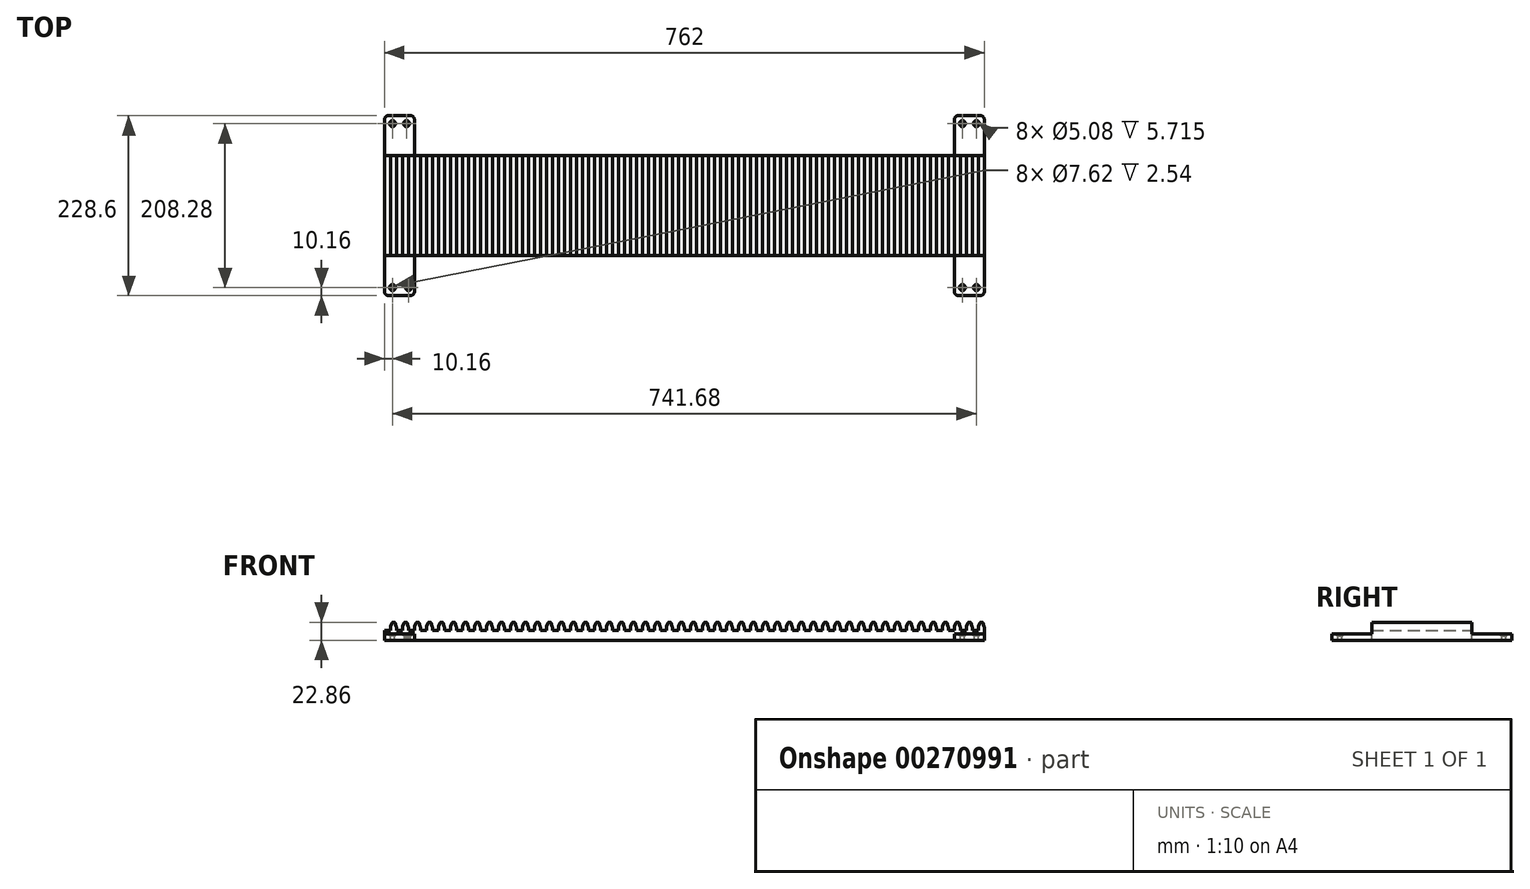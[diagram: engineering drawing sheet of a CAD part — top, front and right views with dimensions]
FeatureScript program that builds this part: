
annotation { "Feature Type Name" : "Feature", "Feature Type Description" : "" }
export const myFeature = defineFeature(function(context is Context, id is Id, definition is map)
    precondition{}
    {
        {
            var Q0;
            Q0=qCreatedBy(makeId("Front.planeOp"),FACE);
            var sketch = newSketch(context, id + "F0", { "sketchPlane" : qUnion([Q0])});
            skLineSegment(sketch, "E0.bottom", {"start": v(0, 0) * mm, "end": v(762, 0) * mm});
            skLineSegment(sketch, "E0.top", {"start": v(0, 12.7) * mm, "end": v(762, 12.7) * mm});
            skLineSegment(sketch, "E0.left", {"start": v(0, 0) * mm, "end": v(0, 12.7) * mm});
            skLineSegment(sketch, "E0.right", {"start": v(762, 0) * mm, "end": v(762, 12.7) * mm});
            skLineSegment(sketch, "E1", {"start": v(7.62, 12.7) * mm, "end": v(7.62, 15.54) * mm});
            skLineSegment(sketch, "E2", {"start": v(8, 17.71) * mm, "end": v(9.69, 22.34) * mm});
            skLineSegment(sketch, "E3", {"start": v(11.43, 25.84) * mm, "end": v(11.43, 12.7) * mm, "construction": true});
            skLineSegment(sketch, "E4", {"start": v(10.43, 22.86) * mm, "end": v(11.43, 22.86) * mm});
            skLineSegment(sketch, "E5.MirrorCS", {"start": v(12.43, 22.86) * mm, "end": v(11.43, 22.86) * mm});
            skLineSegment(sketch, "E6.MirrorCS", {"start": v(14.86, 17.71) * mm, "end": v(13.17, 22.34) * mm});
            skLineSegment(sketch, "E7.MirrorCS", {"start": v(15.24, 12.7) * mm, "end": v(15.24, 15.54) * mm});
            skPoint(sketch, "E8.visualSharp", {"position": v(12.98, 22.86) * mm});
            skArc(sketch, "E8.filletArc", {"start": v(13.17, 22.34) * mm, "mid": v(12.88, 22.72) * mm, "end": v(12.43, 22.86) * mm});
            skPoint(sketch, "E9.visualSharp", {"position": v(9.88, 22.86) * mm});
            skArc(sketch, "E9.filletArc", {"start": v(10.43, 22.86) * mm, "mid": v(9.98, 22.72) * mm, "end": v(9.69, 22.34) * mm});
            skPoint(sketch, "E10.visualSharp", {"position": v(15.24, 16.66) * mm});
            skArc(sketch, "E10.filletArc", {"start": v(15.24, 15.54) * mm, "mid": v(15.14, 16.65) * mm, "end": v(14.86, 17.71) * mm});
            skPoint(sketch, "E11.visualSharp", {"position": v(7.62, 16.66) * mm});
            skArc(sketch, "E11.filletArc", {"start": v(8, 17.71) * mm, "mid": v(7.72, 16.65) * mm, "end": v(7.62, 15.54) * mm});
            skLineSegment(sketch, "E12.1.0.0", {"start": v(22.86, 12.7) * mm, "end": v(22.86, 15.54) * mm});
            skArc(sketch, "E12.1.0.1", {"start": v(23.24, 17.71) * mm, "mid": v(22.96, 16.65) * mm, "end": v(22.86, 15.54) * mm});
            skLineSegment(sketch, "E12.1.0.2", {"start": v(23.24, 17.71) * mm, "end": v(24.93, 22.34) * mm});
            skPoint(sketch, "E12.1.0.3", {"position": v(25.12, 22.86) * mm});
            skArc(sketch, "E12.1.0.4", {"start": v(25.67, 22.86) * mm, "mid": v(25.22, 22.72) * mm, "end": v(24.93, 22.34) * mm});
            skLineSegment(sketch, "E12.1.0.5", {"start": v(25.67, 22.86) * mm, "end": v(26.67, 22.86) * mm});
            skLineSegment(sketch, "E12.1.0.6", {"start": v(27.67, 22.86) * mm, "end": v(26.67, 22.86) * mm});
            skArc(sketch, "E12.1.0.7", {"start": v(28.41, 22.34) * mm, "mid": v(28.12, 22.72) * mm, "end": v(27.67, 22.86) * mm});
            skLineSegment(sketch, "E12.1.0.8", {"start": v(30.1, 17.71) * mm, "end": v(28.41, 22.34) * mm});
            skArc(sketch, "E12.1.0.9", {"start": v(30.48, 15.54) * mm, "mid": v(30.38, 16.65) * mm, "end": v(30.1, 17.71) * mm});
            skLineSegment(sketch, "E12.1.0.10", {"start": v(30.48, 12.7) * mm, "end": v(30.48, 15.54) * mm});
            skLineSegment(sketch, "E12.2.0.0", {"start": v(38.1, 12.7) * mm, "end": v(38.1, 15.54) * mm});
            skArc(sketch, "E12.2.0.1", {"start": v(38.48, 17.71) * mm, "mid": v(38.2, 16.65) * mm, "end": v(38.1, 15.54) * mm});
            skLineSegment(sketch, "E12.2.0.2", {"start": v(38.48, 17.71) * mm, "end": v(40.17, 22.34) * mm});
            skPoint(sketch, "E12.2.0.3", {"position": v(40.36, 22.86) * mm});
            skArc(sketch, "E12.2.0.4", {"start": v(40.91, 22.86) * mm, "mid": v(40.46, 22.72) * mm, "end": v(40.17, 22.34) * mm});
            skLineSegment(sketch, "E12.2.0.5", {"start": v(40.91, 22.86) * mm, "end": v(41.91, 22.86) * mm});
            skLineSegment(sketch, "E12.2.0.6", {"start": v(42.9, 22.86) * mm, "end": v(41.91, 22.86) * mm});
            skArc(sketch, "E12.2.0.7", {"start": v(43.65, 22.34) * mm, "mid": v(43.36, 22.72) * mm, "end": v(42.9, 22.86) * mm});
            skLineSegment(sketch, "E12.2.0.8", {"start": v(45.34, 17.71) * mm, "end": v(43.65, 22.34) * mm});
            skArc(sketch, "E12.2.0.9", {"start": v(45.72, 15.54) * mm, "mid": v(45.62, 16.65) * mm, "end": v(45.34, 17.71) * mm});
            skLineSegment(sketch, "E12.2.0.10", {"start": v(45.72, 12.7) * mm, "end": v(45.72, 15.54) * mm});
            skLineSegment(sketch, "E12.3.0.0", {"start": v(53.34, 12.7) * mm, "end": v(53.34, 15.54) * mm});
            skArc(sketch, "E12.3.0.1", {"start": v(53.72, 17.71) * mm, "mid": v(53.44, 16.65) * mm, "end": v(53.34, 15.54) * mm});
            skLineSegment(sketch, "E12.3.0.2", {"start": v(53.72, 17.71) * mm, "end": v(55.4, 22.34) * mm});
            skPoint(sketch, "E12.3.0.3", {"position": v(55.6, 22.86) * mm});
            skArc(sketch, "E12.3.0.4", {"start": v(56.15, 22.86) * mm, "mid": v(55.7, 22.72) * mm, "end": v(55.4, 22.34) * mm});
            skLineSegment(sketch, "E12.3.0.5", {"start": v(56.15, 22.86) * mm, "end": v(57.15, 22.86) * mm});
            skLineSegment(sketch, "E12.3.0.6", {"start": v(58.15, 22.86) * mm, "end": v(57.15, 22.86) * mm});
            skArc(sketch, "E12.3.0.7", {"start": v(58.9, 22.34) * mm, "mid": v(58.6, 22.72) * mm, "end": v(58.15, 22.86) * mm});
            skLineSegment(sketch, "E12.3.0.8", {"start": v(60.58, 17.71) * mm, "end": v(58.9, 22.34) * mm});
            skArc(sketch, "E12.3.0.9", {"start": v(60.96, 15.54) * mm, "mid": v(60.86, 16.65) * mm, "end": v(60.58, 17.71) * mm});
            skLineSegment(sketch, "E12.3.0.10", {"start": v(60.96, 12.7) * mm, "end": v(60.96, 15.54) * mm});
            skLineSegment(sketch, "E12.4.0.0", {"start": v(68.58, 12.7) * mm, "end": v(68.58, 15.54) * mm});
            skArc(sketch, "E12.4.0.1", {"start": v(68.96, 17.71) * mm, "mid": v(68.68, 16.65) * mm, "end": v(68.58, 15.54) * mm});
            skLineSegment(sketch, "E12.4.0.2", {"start": v(68.96, 17.71) * mm, "end": v(70.65, 22.34) * mm});
            skPoint(sketch, "E12.4.0.3", {"position": v(70.84, 22.86) * mm});
            skArc(sketch, "E12.4.0.4", {"start": v(71.4, 22.86) * mm, "mid": v(70.94, 22.72) * mm, "end": v(70.65, 22.34) * mm});
            skLineSegment(sketch, "E12.4.0.5", {"start": v(71.4, 22.86) * mm, "end": v(72.4, 22.86) * mm});
            skLineSegment(sketch, "E12.4.0.6", {"start": v(73.39, 22.86) * mm, "end": v(72.4, 22.86) * mm});
            skArc(sketch, "E12.4.0.7", {"start": v(74.13, 22.34) * mm, "mid": v(73.84, 22.72) * mm, "end": v(73.39, 22.86) * mm});
            skLineSegment(sketch, "E12.4.0.8", {"start": v(75.82, 17.71) * mm, "end": v(74.13, 22.34) * mm});
            skArc(sketch, "E12.4.0.9", {"start": v(76.2, 15.54) * mm, "mid": v(76.1, 16.65) * mm, "end": v(75.82, 17.71) * mm});
            skLineSegment(sketch, "E12.4.0.10", {"start": v(76.2, 12.7) * mm, "end": v(76.2, 15.54) * mm});
            skLineSegment(sketch, "E12.5.0.0", {"start": v(83.82, 12.7) * mm, "end": v(83.82, 15.54) * mm});
            skArc(sketch, "E12.5.0.1", {"start": v(84.2, 17.71) * mm, "mid": v(83.92, 16.65) * mm, "end": v(83.82, 15.54) * mm});
            skLineSegment(sketch, "E12.5.0.2", {"start": v(84.2, 17.71) * mm, "end": v(85.89, 22.34) * mm});
            skPoint(sketch, "E12.5.0.3", {"position": v(86.08, 22.86) * mm});
            skArc(sketch, "E12.5.0.4", {"start": v(86.63, 22.86) * mm, "mid": v(86.18, 22.72) * mm, "end": v(85.89, 22.34) * mm});
            skLineSegment(sketch, "E12.5.0.5", {"start": v(86.63, 22.86) * mm, "end": v(87.63, 22.86) * mm});
            skLineSegment(sketch, "E12.5.0.6", {"start": v(88.63, 22.86) * mm, "end": v(87.63, 22.86) * mm});
            skArc(sketch, "E12.5.0.7", {"start": v(89.37, 22.34) * mm, "mid": v(89.08, 22.72) * mm, "end": v(88.63, 22.86) * mm});
            skLineSegment(sketch, "E12.5.0.8", {"start": v(91.06, 17.71) * mm, "end": v(89.37, 22.34) * mm});
            skArc(sketch, "E12.5.0.9", {"start": v(91.44, 15.54) * mm, "mid": v(91.34, 16.65) * mm, "end": v(91.06, 17.71) * mm});
            skLineSegment(sketch, "E12.5.0.10", {"start": v(91.44, 12.7) * mm, "end": v(91.44, 15.54) * mm});
            skLineSegment(sketch, "E12.6.0.0", {"start": v(99.06, 12.7) * mm, "end": v(99.06, 15.54) * mm});
            skArc(sketch, "E12.6.0.1", {"start": v(99.44, 17.71) * mm, "mid": v(99.16, 16.65) * mm, "end": v(99.06, 15.54) * mm});
            skLineSegment(sketch, "E12.6.0.2", {"start": v(99.44, 17.71) * mm, "end": v(101.13, 22.34) * mm});
            skPoint(sketch, "E12.6.0.3", {"position": v(101.32, 22.86) * mm});
            skArc(sketch, "E12.6.0.4", {"start": v(101.87, 22.86) * mm, "mid": v(101.42, 22.72) * mm, "end": v(101.13, 22.34) * mm});
            skLineSegment(sketch, "E12.6.0.5", {"start": v(101.87, 22.86) * mm, "end": v(102.87, 22.86) * mm});
            skLineSegment(sketch, "E12.6.0.6", {"start": v(103.87, 22.86) * mm, "end": v(102.87, 22.86) * mm});
            skArc(sketch, "E12.6.0.7", {"start": v(104.61, 22.34) * mm, "mid": v(104.32, 22.72) * mm, "end": v(103.87, 22.86) * mm});
            skLineSegment(sketch, "E12.6.0.8", {"start": v(106.3, 17.71) * mm, "end": v(104.61, 22.34) * mm});
            skArc(sketch, "E12.6.0.9", {"start": v(106.68, 15.54) * mm, "mid": v(106.58, 16.65) * mm, "end": v(106.3, 17.71) * mm});
            skLineSegment(sketch, "E12.6.0.10", {"start": v(106.68, 12.7) * mm, "end": v(106.68, 15.54) * mm});
            skLineSegment(sketch, "E12.7.0.0", {"start": v(114.3, 12.7) * mm, "end": v(114.3, 15.54) * mm});
            skArc(sketch, "E12.7.0.1", {"start": v(114.68, 17.71) * mm, "mid": v(114.4, 16.65) * mm, "end": v(114.3, 15.54) * mm});
            skLineSegment(sketch, "E12.7.0.2", {"start": v(114.68, 17.71) * mm, "end": v(116.37, 22.34) * mm});
            skPoint(sketch, "E12.7.0.3", {"position": v(116.56, 22.86) * mm});
            skArc(sketch, "E12.7.0.4", {"start": v(117.11, 22.86) * mm, "mid": v(116.66, 22.72) * mm, "end": v(116.37, 22.34) * mm});
            skLineSegment(sketch, "E12.7.0.5", {"start": v(117.11, 22.86) * mm, "end": v(118.11, 22.86) * mm});
            skLineSegment(sketch, "E12.7.0.6", {"start": v(119.1, 22.86) * mm, "end": v(118.11, 22.86) * mm});
            skArc(sketch, "E12.7.0.7", {"start": v(119.85, 22.34) * mm, "mid": v(119.56, 22.72) * mm, "end": v(119.1, 22.86) * mm});
            skLineSegment(sketch, "E12.7.0.8", {"start": v(121.54, 17.71) * mm, "end": v(119.85, 22.34) * mm});
            skArc(sketch, "E12.7.0.9", {"start": v(121.92, 15.54) * mm, "mid": v(121.82, 16.65) * mm, "end": v(121.54, 17.71) * mm});
            skLineSegment(sketch, "E12.7.0.10", {"start": v(121.92, 12.7) * mm, "end": v(121.92, 15.54) * mm});
            skLineSegment(sketch, "E12.8.0.0", {"start": v(129.54, 12.7) * mm, "end": v(129.54, 15.54) * mm});
            skArc(sketch, "E12.8.0.1", {"start": v(129.92, 17.71) * mm, "mid": v(129.64, 16.65) * mm, "end": v(129.54, 15.54) * mm});
            skLineSegment(sketch, "E12.8.0.2", {"start": v(129.92, 17.71) * mm, "end": v(131.6, 22.34) * mm});
            skPoint(sketch, "E12.8.0.3", {"position": v(131.8, 22.86) * mm});
            skArc(sketch, "E12.8.0.4", {"start": v(132.35, 22.86) * mm, "mid": v(131.9, 22.72) * mm, "end": v(131.6, 22.34) * mm});
            skLineSegment(sketch, "E12.8.0.5", {"start": v(132.35, 22.86) * mm, "end": v(133.35, 22.86) * mm});
            skLineSegment(sketch, "E12.8.0.6", {"start": v(134.35, 22.86) * mm, "end": v(133.35, 22.86) * mm});
            skArc(sketch, "E12.8.0.7", {"start": v(135.1, 22.34) * mm, "mid": v(134.8, 22.72) * mm, "end": v(134.35, 22.86) * mm});
            skLineSegment(sketch, "E12.8.0.8", {"start": v(136.78, 17.71) * mm, "end": v(135.1, 22.34) * mm});
            skArc(sketch, "E12.8.0.9", {"start": v(137.16, 15.54) * mm, "mid": v(137.06, 16.65) * mm, "end": v(136.78, 17.71) * mm});
            skLineSegment(sketch, "E12.8.0.10", {"start": v(137.16, 12.7) * mm, "end": v(137.16, 15.54) * mm});
            skLineSegment(sketch, "E12.9.0.0", {"start": v(144.78, 12.7) * mm, "end": v(144.78, 15.54) * mm});
            skArc(sketch, "E12.9.0.1", {"start": v(145.16, 17.71) * mm, "mid": v(144.88, 16.65) * mm, "end": v(144.78, 15.54) * mm});
            skLineSegment(sketch, "E12.9.0.2", {"start": v(145.16, 17.71) * mm, "end": v(146.85, 22.34) * mm});
            skPoint(sketch, "E12.9.0.3", {"position": v(147.04, 22.86) * mm});
            skArc(sketch, "E12.9.0.4", {"start": v(147.6, 22.86) * mm, "mid": v(147.14, 22.72) * mm, "end": v(146.85, 22.34) * mm});
            skLineSegment(sketch, "E12.9.0.5", {"start": v(147.6, 22.86) * mm, "end": v(148.6, 22.86) * mm});
            skLineSegment(sketch, "E12.9.0.6", {"start": v(149.59, 22.86) * mm, "end": v(148.6, 22.86) * mm});
            skArc(sketch, "E12.9.0.7", {"start": v(150.33, 22.34) * mm, "mid": v(150.04, 22.72) * mm, "end": v(149.59, 22.86) * mm});
            skLineSegment(sketch, "E12.9.0.8", {"start": v(152.02, 17.71) * mm, "end": v(150.33, 22.34) * mm});
            skArc(sketch, "E12.9.0.9", {"start": v(152.4, 15.54) * mm, "mid": v(152.3, 16.65) * mm, "end": v(152.02, 17.71) * mm});
            skLineSegment(sketch, "E12.9.0.10", {"start": v(152.4, 12.7) * mm, "end": v(152.4, 15.54) * mm});
            skLineSegment(sketch, "E12.10.0.0", {"start": v(160.02, 12.7) * mm, "end": v(160.02, 15.54) * mm});
            skArc(sketch, "E12.10.0.1", {"start": v(160.4, 17.71) * mm, "mid": v(160.12, 16.65) * mm, "end": v(160.02, 15.54) * mm});
            skLineSegment(sketch, "E12.10.0.2", {"start": v(160.4, 17.71) * mm, "end": v(162.09, 22.34) * mm});
            skPoint(sketch, "E12.10.0.3", {"position": v(162.28, 22.86) * mm});
            skArc(sketch, "E12.10.0.4", {"start": v(162.83, 22.86) * mm, "mid": v(162.38, 22.72) * mm, "end": v(162.09, 22.34) * mm});
            skLineSegment(sketch, "E12.10.0.5", {"start": v(162.83, 22.86) * mm, "end": v(163.83, 22.86) * mm});
            skLineSegment(sketch, "E12.10.0.6", {"start": v(164.83, 22.86) * mm, "end": v(163.83, 22.86) * mm});
            skArc(sketch, "E12.10.0.7", {"start": v(165.57, 22.34) * mm, "mid": v(165.28, 22.72) * mm, "end": v(164.83, 22.86) * mm});
            skLineSegment(sketch, "E12.10.0.8", {"start": v(167.26, 17.71) * mm, "end": v(165.57, 22.34) * mm});
            skArc(sketch, "E12.10.0.9", {"start": v(167.64, 15.54) * mm, "mid": v(167.54, 16.65) * mm, "end": v(167.26, 17.71) * mm});
            skLineSegment(sketch, "E12.10.0.10", {"start": v(167.64, 12.7) * mm, "end": v(167.64, 15.54) * mm});
            skLineSegment(sketch, "E12.11.0.0", {"start": v(175.26, 12.7) * mm, "end": v(175.26, 15.54) * mm});
            skArc(sketch, "E12.11.0.1", {"start": v(175.64, 17.71) * mm, "mid": v(175.36, 16.65) * mm, "end": v(175.26, 15.54) * mm});
            skLineSegment(sketch, "E12.11.0.2", {"start": v(175.64, 17.71) * mm, "end": v(177.33, 22.34) * mm});
            skPoint(sketch, "E12.11.0.3", {"position": v(177.52, 22.86) * mm});
            skArc(sketch, "E12.11.0.4", {"start": v(178.07, 22.86) * mm, "mid": v(177.62, 22.72) * mm, "end": v(177.33, 22.34) * mm});
            skLineSegment(sketch, "E12.11.0.5", {"start": v(178.07, 22.86) * mm, "end": v(179.07, 22.86) * mm});
            skLineSegment(sketch, "E12.11.0.6", {"start": v(180.07, 22.86) * mm, "end": v(179.07, 22.86) * mm});
            skArc(sketch, "E12.11.0.7", {"start": v(180.81, 22.34) * mm, "mid": v(180.52, 22.72) * mm, "end": v(180.07, 22.86) * mm});
            skLineSegment(sketch, "E12.11.0.8", {"start": v(182.5, 17.71) * mm, "end": v(180.81, 22.34) * mm});
            skArc(sketch, "E12.11.0.9", {"start": v(182.88, 15.54) * mm, "mid": v(182.78, 16.65) * mm, "end": v(182.5, 17.71) * mm});
            skLineSegment(sketch, "E12.11.0.10", {"start": v(182.88, 12.7) * mm, "end": v(182.88, 15.54) * mm});
            skLineSegment(sketch, "E12.12.0.0", {"start": v(190.5, 12.7) * mm, "end": v(190.5, 15.54) * mm});
            skArc(sketch, "E12.12.0.1", {"start": v(190.88, 17.71) * mm, "mid": v(190.6, 16.65) * mm, "end": v(190.5, 15.54) * mm});
            skLineSegment(sketch, "E12.12.0.2", {"start": v(190.88, 17.71) * mm, "end": v(192.57, 22.34) * mm});
            skPoint(sketch, "E12.12.0.3", {"position": v(192.76, 22.86) * mm});
            skArc(sketch, "E12.12.0.4", {"start": v(193.31, 22.86) * mm, "mid": v(192.86, 22.72) * mm, "end": v(192.57, 22.34) * mm});
            skLineSegment(sketch, "E12.12.0.5", {"start": v(193.31, 22.86) * mm, "end": v(194.31, 22.86) * mm});
            skLineSegment(sketch, "E12.12.0.6", {"start": v(195.3, 22.86) * mm, "end": v(194.31, 22.86) * mm});
            skArc(sketch, "E12.12.0.7", {"start": v(196.05, 22.34) * mm, "mid": v(195.76, 22.72) * mm, "end": v(195.3, 22.86) * mm});
            skLineSegment(sketch, "E12.12.0.8", {"start": v(197.74, 17.71) * mm, "end": v(196.05, 22.34) * mm});
            skArc(sketch, "E12.12.0.9", {"start": v(198.12, 15.54) * mm, "mid": v(198.02, 16.65) * mm, "end": v(197.74, 17.71) * mm});
            skLineSegment(sketch, "E12.12.0.10", {"start": v(198.12, 12.7) * mm, "end": v(198.12, 15.54) * mm});
            skLineSegment(sketch, "E12.13.0.0", {"start": v(205.74, 12.7) * mm, "end": v(205.74, 15.54) * mm});
            skArc(sketch, "E12.13.0.1", {"start": v(206.12, 17.71) * mm, "mid": v(205.84, 16.65) * mm, "end": v(205.74, 15.54) * mm});
            skLineSegment(sketch, "E12.13.0.2", {"start": v(206.12, 17.71) * mm, "end": v(207.8, 22.34) * mm});
            skPoint(sketch, "E12.13.0.3", {"position": v(208, 22.86) * mm});
            skArc(sketch, "E12.13.0.4", {"start": v(208.55, 22.86) * mm, "mid": v(208.1, 22.72) * mm, "end": v(207.8, 22.34) * mm});
            skLineSegment(sketch, "E12.13.0.5", {"start": v(208.55, 22.86) * mm, "end": v(209.55, 22.86) * mm});
            skLineSegment(sketch, "E12.13.0.6", {"start": v(210.55, 22.86) * mm, "end": v(209.55, 22.86) * mm});
            skArc(sketch, "E12.13.0.7", {"start": v(211.3, 22.34) * mm, "mid": v(211, 22.72) * mm, "end": v(210.55, 22.86) * mm});
            skLineSegment(sketch, "E12.13.0.8", {"start": v(212.98, 17.71) * mm, "end": v(211.3, 22.34) * mm});
            skArc(sketch, "E12.13.0.9", {"start": v(213.36, 15.54) * mm, "mid": v(213.26, 16.65) * mm, "end": v(212.98, 17.71) * mm});
            skLineSegment(sketch, "E12.13.0.10", {"start": v(213.36, 12.7) * mm, "end": v(213.36, 15.54) * mm});
            skLineSegment(sketch, "E12.14.0.0", {"start": v(220.98, 12.7) * mm, "end": v(220.98, 15.54) * mm});
            skArc(sketch, "E12.14.0.1", {"start": v(221.36, 17.71) * mm, "mid": v(221.08, 16.65) * mm, "end": v(220.98, 15.54) * mm});
            skLineSegment(sketch, "E12.14.0.2", {"start": v(221.36, 17.71) * mm, "end": v(223.05, 22.34) * mm});
            skPoint(sketch, "E12.14.0.3", {"position": v(223.24, 22.86) * mm});
            skArc(sketch, "E12.14.0.4", {"start": v(223.8, 22.86) * mm, "mid": v(223.34, 22.72) * mm, "end": v(223.05, 22.34) * mm});
            skLineSegment(sketch, "E12.14.0.5", {"start": v(223.8, 22.86) * mm, "end": v(224.8, 22.86) * mm});
            skLineSegment(sketch, "E12.14.0.6", {"start": v(225.79, 22.86) * mm, "end": v(224.8, 22.86) * mm});
            skArc(sketch, "E12.14.0.7", {"start": v(226.53, 22.34) * mm, "mid": v(226.24, 22.72) * mm, "end": v(225.79, 22.86) * mm});
            skLineSegment(sketch, "E12.14.0.8", {"start": v(228.22, 17.71) * mm, "end": v(226.53, 22.34) * mm});
            skArc(sketch, "E12.14.0.9", {"start": v(228.6, 15.54) * mm, "mid": v(228.5, 16.65) * mm, "end": v(228.22, 17.71) * mm});
            skLineSegment(sketch, "E12.14.0.10", {"start": v(228.6, 12.7) * mm, "end": v(228.6, 15.54) * mm});
            skLineSegment(sketch, "E12.15.0.0", {"start": v(236.22, 12.7) * mm, "end": v(236.22, 15.54) * mm});
            skArc(sketch, "E12.15.0.1", {"start": v(236.6, 17.71) * mm, "mid": v(236.32, 16.65) * mm, "end": v(236.22, 15.54) * mm});
            skLineSegment(sketch, "E12.15.0.2", {"start": v(236.6, 17.71) * mm, "end": v(238.29, 22.34) * mm});
            skPoint(sketch, "E12.15.0.3", {"position": v(238.48, 22.86) * mm});
            skArc(sketch, "E12.15.0.4", {"start": v(239.03, 22.86) * mm, "mid": v(238.58, 22.72) * mm, "end": v(238.29, 22.34) * mm});
            skLineSegment(sketch, "E12.15.0.5", {"start": v(239.03, 22.86) * mm, "end": v(240.03, 22.86) * mm});
            skLineSegment(sketch, "E12.15.0.6", {"start": v(241.03, 22.86) * mm, "end": v(240.03, 22.86) * mm});
            skArc(sketch, "E12.15.0.7", {"start": v(241.77, 22.34) * mm, "mid": v(241.48, 22.72) * mm, "end": v(241.03, 22.86) * mm});
            skLineSegment(sketch, "E12.15.0.8", {"start": v(243.46, 17.71) * mm, "end": v(241.77, 22.34) * mm});
            skArc(sketch, "E12.15.0.9", {"start": v(243.84, 15.54) * mm, "mid": v(243.74, 16.65) * mm, "end": v(243.46, 17.71) * mm});
            skLineSegment(sketch, "E12.15.0.10", {"start": v(243.84, 12.7) * mm, "end": v(243.84, 15.54) * mm});
            skLineSegment(sketch, "E12.16.0.0", {"start": v(251.46, 12.7) * mm, "end": v(251.46, 15.54) * mm});
            skArc(sketch, "E12.16.0.1", {"start": v(251.84, 17.71) * mm, "mid": v(251.56, 16.65) * mm, "end": v(251.46, 15.54) * mm});
            skLineSegment(sketch, "E12.16.0.2", {"start": v(251.84, 17.71) * mm, "end": v(253.53, 22.34) * mm});
            skPoint(sketch, "E12.16.0.3", {"position": v(253.72, 22.86) * mm});
            skArc(sketch, "E12.16.0.4", {"start": v(254.27, 22.86) * mm, "mid": v(253.82, 22.72) * mm, "end": v(253.53, 22.34) * mm});
            skLineSegment(sketch, "E12.16.0.5", {"start": v(254.27, 22.86) * mm, "end": v(255.27, 22.86) * mm});
            skLineSegment(sketch, "E12.16.0.6", {"start": v(256.27, 22.86) * mm, "end": v(255.27, 22.86) * mm});
            skArc(sketch, "E12.16.0.7", {"start": v(257.01, 22.34) * mm, "mid": v(256.72, 22.72) * mm, "end": v(256.27, 22.86) * mm});
            skLineSegment(sketch, "E12.16.0.8", {"start": v(258.7, 17.71) * mm, "end": v(257.01, 22.34) * mm});
            skArc(sketch, "E12.16.0.9", {"start": v(259.08, 15.54) * mm, "mid": v(258.98, 16.65) * mm, "end": v(258.7, 17.71) * mm});
            skLineSegment(sketch, "E12.16.0.10", {"start": v(259.08, 12.7) * mm, "end": v(259.08, 15.54) * mm});
            skLineSegment(sketch, "E12.17.0.0", {"start": v(266.7, 12.7) * mm, "end": v(266.7, 15.54) * mm});
            skArc(sketch, "E12.17.0.1", {"start": v(267.08, 17.71) * mm, "mid": v(266.8, 16.65) * mm, "end": v(266.7, 15.54) * mm});
            skLineSegment(sketch, "E12.17.0.2", {"start": v(267.08, 17.71) * mm, "end": v(268.77, 22.34) * mm});
            skPoint(sketch, "E12.17.0.3", {"position": v(268.96, 22.86) * mm});
            skArc(sketch, "E12.17.0.4", {"start": v(269.51, 22.86) * mm, "mid": v(269.06, 22.72) * mm, "end": v(268.77, 22.34) * mm});
            skLineSegment(sketch, "E12.17.0.5", {"start": v(269.51, 22.86) * mm, "end": v(270.51, 22.86) * mm});
            skLineSegment(sketch, "E12.17.0.6", {"start": v(271.5, 22.86) * mm, "end": v(270.51, 22.86) * mm});
            skArc(sketch, "E12.17.0.7", {"start": v(272.25, 22.34) * mm, "mid": v(271.96, 22.72) * mm, "end": v(271.5, 22.86) * mm});
            skLineSegment(sketch, "E12.17.0.8", {"start": v(273.94, 17.71) * mm, "end": v(272.25, 22.34) * mm});
            skArc(sketch, "E12.17.0.9", {"start": v(274.32, 15.54) * mm, "mid": v(274.22, 16.65) * mm, "end": v(273.94, 17.71) * mm});
            skLineSegment(sketch, "E12.17.0.10", {"start": v(274.32, 12.7) * mm, "end": v(274.32, 15.54) * mm});
            skLineSegment(sketch, "E12.18.0.0", {"start": v(281.94, 12.7) * mm, "end": v(281.94, 15.54) * mm});
            skArc(sketch, "E12.18.0.1", {"start": v(282.32, 17.71) * mm, "mid": v(282.04, 16.65) * mm, "end": v(281.94, 15.54) * mm});
            skLineSegment(sketch, "E12.18.0.2", {"start": v(282.32, 17.71) * mm, "end": v(284, 22.34) * mm});
            skPoint(sketch, "E12.18.0.3", {"position": v(284.2, 22.86) * mm});
            skArc(sketch, "E12.18.0.4", {"start": v(284.75, 22.86) * mm, "mid": v(284.3, 22.72) * mm, "end": v(284, 22.34) * mm});
            skLineSegment(sketch, "E12.18.0.5", {"start": v(284.75, 22.86) * mm, "end": v(285.75, 22.86) * mm});
            skLineSegment(sketch, "E12.18.0.6", {"start": v(286.75, 22.86) * mm, "end": v(285.75, 22.86) * mm});
            skArc(sketch, "E12.18.0.7", {"start": v(287.5, 22.34) * mm, "mid": v(287.2, 22.72) * mm, "end": v(286.75, 22.86) * mm});
            skLineSegment(sketch, "E12.18.0.8", {"start": v(289.18, 17.71) * mm, "end": v(287.5, 22.34) * mm});
            skArc(sketch, "E12.18.0.9", {"start": v(289.56, 15.54) * mm, "mid": v(289.46, 16.65) * mm, "end": v(289.18, 17.71) * mm});
            skLineSegment(sketch, "E12.18.0.10", {"start": v(289.56, 12.7) * mm, "end": v(289.56, 15.54) * mm});
            skLineSegment(sketch, "E12.19.0.0", {"start": v(297.18, 12.7) * mm, "end": v(297.18, 15.54) * mm});
            skArc(sketch, "E12.19.0.1", {"start": v(297.56, 17.71) * mm, "mid": v(297.28, 16.65) * mm, "end": v(297.18, 15.54) * mm});
            skLineSegment(sketch, "E12.19.0.2", {"start": v(297.56, 17.71) * mm, "end": v(299.25, 22.34) * mm});
            skPoint(sketch, "E12.19.0.3", {"position": v(299.44, 22.86) * mm});
            skArc(sketch, "E12.19.0.4", {"start": v(300, 22.86) * mm, "mid": v(299.54, 22.72) * mm, "end": v(299.25, 22.34) * mm});
            skLineSegment(sketch, "E12.19.0.5", {"start": v(300, 22.86) * mm, "end": v(301, 22.86) * mm});
            skLineSegment(sketch, "E12.19.0.6", {"start": v(301.99, 22.86) * mm, "end": v(301, 22.86) * mm});
            skArc(sketch, "E12.19.0.7", {"start": v(302.73, 22.34) * mm, "mid": v(302.44, 22.72) * mm, "end": v(301.99, 22.86) * mm});
            skLineSegment(sketch, "E12.19.0.8", {"start": v(304.42, 17.71) * mm, "end": v(302.73, 22.34) * mm});
            skArc(sketch, "E12.19.0.9", {"start": v(304.8, 15.54) * mm, "mid": v(304.7, 16.65) * mm, "end": v(304.42, 17.71) * mm});
            skLineSegment(sketch, "E12.19.0.10", {"start": v(304.8, 12.7) * mm, "end": v(304.8, 15.54) * mm});
            skLineSegment(sketch, "E12.20.0.0", {"start": v(312.42, 12.7) * mm, "end": v(312.42, 15.54) * mm});
            skArc(sketch, "E12.20.0.1", {"start": v(312.8, 17.71) * mm, "mid": v(312.52, 16.65) * mm, "end": v(312.42, 15.54) * mm});
            skLineSegment(sketch, "E12.20.0.2", {"start": v(312.8, 17.71) * mm, "end": v(314.49, 22.34) * mm});
            skPoint(sketch, "E12.20.0.3", {"position": v(314.68, 22.86) * mm});
            skArc(sketch, "E12.20.0.4", {"start": v(315.23, 22.86) * mm, "mid": v(314.78, 22.72) * mm, "end": v(314.49, 22.34) * mm});
            skLineSegment(sketch, "E12.20.0.5", {"start": v(315.23, 22.86) * mm, "end": v(316.23, 22.86) * mm});
            skLineSegment(sketch, "E12.20.0.6", {"start": v(317.23, 22.86) * mm, "end": v(316.23, 22.86) * mm});
            skArc(sketch, "E12.20.0.7", {"start": v(317.97, 22.34) * mm, "mid": v(317.68, 22.72) * mm, "end": v(317.23, 22.86) * mm});
            skLineSegment(sketch, "E12.20.0.8", {"start": v(319.66, 17.71) * mm, "end": v(317.97, 22.34) * mm});
            skArc(sketch, "E12.20.0.9", {"start": v(320.04, 15.54) * mm, "mid": v(319.94, 16.65) * mm, "end": v(319.66, 17.71) * mm});
            skLineSegment(sketch, "E12.20.0.10", {"start": v(320.04, 12.7) * mm, "end": v(320.04, 15.54) * mm});
            skLineSegment(sketch, "E12.21.0.0", {"start": v(327.66, 12.7) * mm, "end": v(327.66, 15.54) * mm});
            skArc(sketch, "E12.21.0.1", {"start": v(328.04, 17.71) * mm, "mid": v(327.76, 16.65) * mm, "end": v(327.66, 15.54) * mm});
            skLineSegment(sketch, "E12.21.0.2", {"start": v(328.04, 17.71) * mm, "end": v(329.73, 22.34) * mm});
            skPoint(sketch, "E12.21.0.3", {"position": v(329.92, 22.86) * mm});
            skArc(sketch, "E12.21.0.4", {"start": v(330.47, 22.86) * mm, "mid": v(330.02, 22.72) * mm, "end": v(329.73, 22.34) * mm});
            skLineSegment(sketch, "E12.21.0.5", {"start": v(330.47, 22.86) * mm, "end": v(331.47, 22.86) * mm});
            skLineSegment(sketch, "E12.21.0.6", {"start": v(332.47, 22.86) * mm, "end": v(331.47, 22.86) * mm});
            skArc(sketch, "E12.21.0.7", {"start": v(333.21, 22.34) * mm, "mid": v(332.92, 22.72) * mm, "end": v(332.47, 22.86) * mm});
            skLineSegment(sketch, "E12.21.0.8", {"start": v(334.9, 17.71) * mm, "end": v(333.21, 22.34) * mm});
            skArc(sketch, "E12.21.0.9", {"start": v(335.28, 15.54) * mm, "mid": v(335.18, 16.65) * mm, "end": v(334.9, 17.71) * mm});
            skLineSegment(sketch, "E12.21.0.10", {"start": v(335.28, 12.7) * mm, "end": v(335.28, 15.54) * mm});
            skLineSegment(sketch, "E12.22.0.0", {"start": v(342.9, 12.7) * mm, "end": v(342.9, 15.54) * mm});
            skArc(sketch, "E12.22.0.1", {"start": v(343.28, 17.71) * mm, "mid": v(343, 16.65) * mm, "end": v(342.9, 15.54) * mm});
            skLineSegment(sketch, "E12.22.0.2", {"start": v(343.28, 17.71) * mm, "end": v(344.97, 22.34) * mm});
            skPoint(sketch, "E12.22.0.3", {"position": v(345.16, 22.86) * mm});
            skArc(sketch, "E12.22.0.4", {"start": v(345.71, 22.86) * mm, "mid": v(345.26, 22.72) * mm, "end": v(344.97, 22.34) * mm});
            skLineSegment(sketch, "E12.22.0.5", {"start": v(345.71, 22.86) * mm, "end": v(346.71, 22.86) * mm});
            skLineSegment(sketch, "E12.22.0.6", {"start": v(347.7, 22.86) * mm, "end": v(346.71, 22.86) * mm});
            skArc(sketch, "E12.22.0.7", {"start": v(348.45, 22.34) * mm, "mid": v(348.16, 22.72) * mm, "end": v(347.7, 22.86) * mm});
            skLineSegment(sketch, "E12.22.0.8", {"start": v(350.14, 17.71) * mm, "end": v(348.45, 22.34) * mm});
            skArc(sketch, "E12.22.0.9", {"start": v(350.52, 15.54) * mm, "mid": v(350.42, 16.65) * mm, "end": v(350.14, 17.71) * mm});
            skLineSegment(sketch, "E12.22.0.10", {"start": v(350.52, 12.7) * mm, "end": v(350.52, 15.54) * mm});
            skLineSegment(sketch, "E12.23.0.0", {"start": v(358.14, 12.7) * mm, "end": v(358.14, 15.54) * mm});
            skArc(sketch, "E12.23.0.1", {"start": v(358.52, 17.71) * mm, "mid": v(358.24, 16.65) * mm, "end": v(358.14, 15.54) * mm});
            skLineSegment(sketch, "E12.23.0.2", {"start": v(358.52, 17.71) * mm, "end": v(360.2, 22.34) * mm});
            skPoint(sketch, "E12.23.0.3", {"position": v(360.4, 22.86) * mm});
            skArc(sketch, "E12.23.0.4", {"start": v(360.95, 22.86) * mm, "mid": v(360.5, 22.72) * mm, "end": v(360.2, 22.34) * mm});
            skLineSegment(sketch, "E12.23.0.5", {"start": v(360.95, 22.86) * mm, "end": v(361.95, 22.86) * mm});
            skLineSegment(sketch, "E12.23.0.6", {"start": v(362.95, 22.86) * mm, "end": v(361.95, 22.86) * mm});
            skArc(sketch, "E12.23.0.7", {"start": v(363.7, 22.34) * mm, "mid": v(363.4, 22.72) * mm, "end": v(362.95, 22.86) * mm});
            skLineSegment(sketch, "E12.23.0.8", {"start": v(365.38, 17.71) * mm, "end": v(363.7, 22.34) * mm});
            skArc(sketch, "E12.23.0.9", {"start": v(365.76, 15.54) * mm, "mid": v(365.66, 16.65) * mm, "end": v(365.38, 17.71) * mm});
            skLineSegment(sketch, "E12.23.0.10", {"start": v(365.76, 12.7) * mm, "end": v(365.76, 15.54) * mm});
            skLineSegment(sketch, "E12.24.0.0", {"start": v(373.38, 12.7) * mm, "end": v(373.38, 15.54) * mm});
            skArc(sketch, "E12.24.0.1", {"start": v(373.76, 17.71) * mm, "mid": v(373.48, 16.65) * mm, "end": v(373.38, 15.54) * mm});
            skLineSegment(sketch, "E12.24.0.2", {"start": v(373.76, 17.71) * mm, "end": v(375.45, 22.34) * mm});
            skPoint(sketch, "E12.24.0.3", {"position": v(375.64, 22.86) * mm});
            skArc(sketch, "E12.24.0.4", {"start": v(376.2, 22.86) * mm, "mid": v(375.74, 22.72) * mm, "end": v(375.45, 22.34) * mm});
            skLineSegment(sketch, "E12.24.0.5", {"start": v(376.2, 22.86) * mm, "end": v(377.2, 22.86) * mm});
            skLineSegment(sketch, "E12.24.0.6", {"start": v(378.19, 22.86) * mm, "end": v(377.2, 22.86) * mm});
            skArc(sketch, "E12.24.0.7", {"start": v(378.93, 22.34) * mm, "mid": v(378.64, 22.72) * mm, "end": v(378.19, 22.86) * mm});
            skLineSegment(sketch, "E12.24.0.8", {"start": v(380.62, 17.71) * mm, "end": v(378.93, 22.34) * mm});
            skArc(sketch, "E12.24.0.9", {"start": v(381, 15.54) * mm, "mid": v(380.9, 16.65) * mm, "end": v(380.62, 17.71) * mm});
            skLineSegment(sketch, "E12.24.0.10", {"start": v(381, 12.7) * mm, "end": v(381, 15.54) * mm});
            skLineSegment(sketch, "E12.25.0.0", {"start": v(388.62, 12.7) * mm, "end": v(388.62, 15.54) * mm});
            skArc(sketch, "E12.25.0.1", {"start": v(389, 17.71) * mm, "mid": v(388.72, 16.65) * mm, "end": v(388.62, 15.54) * mm});
            skLineSegment(sketch, "E12.25.0.2", {"start": v(389, 17.71) * mm, "end": v(390.69, 22.34) * mm});
            skPoint(sketch, "E12.25.0.3", {"position": v(390.88, 22.86) * mm});
            skArc(sketch, "E12.25.0.4", {"start": v(391.43, 22.86) * mm, "mid": v(390.98, 22.72) * mm, "end": v(390.69, 22.34) * mm});
            skLineSegment(sketch, "E12.25.0.5", {"start": v(391.43, 22.86) * mm, "end": v(392.43, 22.86) * mm});
            skLineSegment(sketch, "E12.25.0.6", {"start": v(393.43, 22.86) * mm, "end": v(392.43, 22.86) * mm});
            skArc(sketch, "E12.25.0.7", {"start": v(394.17, 22.34) * mm, "mid": v(393.88, 22.72) * mm, "end": v(393.43, 22.86) * mm});
            skLineSegment(sketch, "E12.25.0.8", {"start": v(395.86, 17.71) * mm, "end": v(394.17, 22.34) * mm});
            skArc(sketch, "E12.25.0.9", {"start": v(396.24, 15.54) * mm, "mid": v(396.14, 16.65) * mm, "end": v(395.86, 17.71) * mm});
            skLineSegment(sketch, "E12.25.0.10", {"start": v(396.24, 12.7) * mm, "end": v(396.24, 15.54) * mm});
            skLineSegment(sketch, "E12.26.0.0", {"start": v(403.86, 12.7) * mm, "end": v(403.86, 15.54) * mm});
            skArc(sketch, "E12.26.0.1", {"start": v(404.24, 17.71) * mm, "mid": v(403.96, 16.65) * mm, "end": v(403.86, 15.54) * mm});
            skLineSegment(sketch, "E12.26.0.2", {"start": v(404.24, 17.71) * mm, "end": v(405.93, 22.34) * mm});
            skPoint(sketch, "E12.26.0.3", {"position": v(406.12, 22.86) * mm});
            skArc(sketch, "E12.26.0.4", {"start": v(406.67, 22.86) * mm, "mid": v(406.22, 22.72) * mm, "end": v(405.93, 22.34) * mm});
            skLineSegment(sketch, "E12.26.0.5", {"start": v(406.67, 22.86) * mm, "end": v(407.67, 22.86) * mm});
            skLineSegment(sketch, "E12.26.0.6", {"start": v(408.67, 22.86) * mm, "end": v(407.67, 22.86) * mm});
            skArc(sketch, "E12.26.0.7", {"start": v(409.41, 22.34) * mm, "mid": v(409.12, 22.72) * mm, "end": v(408.67, 22.86) * mm});
            skLineSegment(sketch, "E12.26.0.8", {"start": v(411.1, 17.71) * mm, "end": v(409.41, 22.34) * mm});
            skArc(sketch, "E12.26.0.9", {"start": v(411.48, 15.54) * mm, "mid": v(411.38, 16.65) * mm, "end": v(411.1, 17.71) * mm});
            skLineSegment(sketch, "E12.26.0.10", {"start": v(411.48, 12.7) * mm, "end": v(411.48, 15.54) * mm});
            skLineSegment(sketch, "E12.27.0.0", {"start": v(419.1, 12.7) * mm, "end": v(419.1, 15.54) * mm});
            skArc(sketch, "E12.27.0.1", {"start": v(419.48, 17.71) * mm, "mid": v(419.2, 16.65) * mm, "end": v(419.1, 15.54) * mm});
            skLineSegment(sketch, "E12.27.0.2", {"start": v(419.48, 17.71) * mm, "end": v(421.17, 22.34) * mm});
            skPoint(sketch, "E12.27.0.3", {"position": v(421.36, 22.86) * mm});
            skArc(sketch, "E12.27.0.4", {"start": v(421.91, 22.86) * mm, "mid": v(421.46, 22.72) * mm, "end": v(421.17, 22.34) * mm});
            skLineSegment(sketch, "E12.27.0.5", {"start": v(421.91, 22.86) * mm, "end": v(422.91, 22.86) * mm});
            skLineSegment(sketch, "E12.27.0.6", {"start": v(423.9, 22.86) * mm, "end": v(422.91, 22.86) * mm});
            skArc(sketch, "E12.27.0.7", {"start": v(424.65, 22.34) * mm, "mid": v(424.36, 22.72) * mm, "end": v(423.9, 22.86) * mm});
            skLineSegment(sketch, "E12.27.0.8", {"start": v(426.34, 17.71) * mm, "end": v(424.65, 22.34) * mm});
            skArc(sketch, "E12.27.0.9", {"start": v(426.72, 15.54) * mm, "mid": v(426.62, 16.65) * mm, "end": v(426.34, 17.71) * mm});
            skLineSegment(sketch, "E12.27.0.10", {"start": v(426.72, 12.7) * mm, "end": v(426.72, 15.54) * mm});
            skLineSegment(sketch, "E12.28.0.0", {"start": v(434.34, 12.7) * mm, "end": v(434.34, 15.54) * mm});
            skArc(sketch, "E12.28.0.1", {"start": v(434.72, 17.71) * mm, "mid": v(434.44, 16.65) * mm, "end": v(434.34, 15.54) * mm});
            skLineSegment(sketch, "E12.28.0.2", {"start": v(434.72, 17.71) * mm, "end": v(436.4, 22.34) * mm});
            skPoint(sketch, "E12.28.0.3", {"position": v(436.6, 22.86) * mm});
            skArc(sketch, "E12.28.0.4", {"start": v(437.15, 22.86) * mm, "mid": v(436.7, 22.72) * mm, "end": v(436.4, 22.34) * mm});
            skLineSegment(sketch, "E12.28.0.5", {"start": v(437.15, 22.86) * mm, "end": v(438.15, 22.86) * mm});
            skLineSegment(sketch, "E12.28.0.6", {"start": v(439.15, 22.86) * mm, "end": v(438.15, 22.86) * mm});
            skArc(sketch, "E12.28.0.7", {"start": v(439.9, 22.34) * mm, "mid": v(439.6, 22.72) * mm, "end": v(439.15, 22.86) * mm});
            skLineSegment(sketch, "E12.28.0.8", {"start": v(441.58, 17.71) * mm, "end": v(439.9, 22.34) * mm});
            skArc(sketch, "E12.28.0.9", {"start": v(441.96, 15.54) * mm, "mid": v(441.86, 16.65) * mm, "end": v(441.58, 17.71) * mm});
            skLineSegment(sketch, "E12.28.0.10", {"start": v(441.96, 12.7) * mm, "end": v(441.96, 15.54) * mm});
            skLineSegment(sketch, "E12.29.0.0", {"start": v(449.58, 12.7) * mm, "end": v(449.58, 15.54) * mm});
            skArc(sketch, "E12.29.0.1", {"start": v(449.96, 17.71) * mm, "mid": v(449.68, 16.65) * mm, "end": v(449.58, 15.54) * mm});
            skLineSegment(sketch, "E12.29.0.2", {"start": v(449.96, 17.71) * mm, "end": v(451.65, 22.34) * mm});
            skPoint(sketch, "E12.29.0.3", {"position": v(451.84, 22.86) * mm});
            skArc(sketch, "E12.29.0.4", {"start": v(452.4, 22.86) * mm, "mid": v(451.94, 22.72) * mm, "end": v(451.65, 22.34) * mm});
            skLineSegment(sketch, "E12.29.0.5", {"start": v(452.4, 22.86) * mm, "end": v(453.4, 22.86) * mm});
            skLineSegment(sketch, "E12.29.0.6", {"start": v(454.39, 22.86) * mm, "end": v(453.4, 22.86) * mm});
            skArc(sketch, "E12.29.0.7", {"start": v(455.13, 22.34) * mm, "mid": v(454.84, 22.72) * mm, "end": v(454.39, 22.86) * mm});
            skLineSegment(sketch, "E12.29.0.8", {"start": v(456.82, 17.71) * mm, "end": v(455.13, 22.34) * mm});
            skArc(sketch, "E12.29.0.9", {"start": v(457.2, 15.54) * mm, "mid": v(457.1, 16.65) * mm, "end": v(456.82, 17.71) * mm});
            skLineSegment(sketch, "E12.29.0.10", {"start": v(457.2, 12.7) * mm, "end": v(457.2, 15.54) * mm});
            skLineSegment(sketch, "E12.30.0.0", {"start": v(464.82, 12.7) * mm, "end": v(464.82, 15.54) * mm});
            skArc(sketch, "E12.30.0.1", {"start": v(465.2, 17.71) * mm, "mid": v(464.92, 16.65) * mm, "end": v(464.82, 15.54) * mm});
            skLineSegment(sketch, "E12.30.0.2", {"start": v(465.2, 17.71) * mm, "end": v(466.89, 22.34) * mm});
            skPoint(sketch, "E12.30.0.3", {"position": v(467.08, 22.86) * mm});
            skArc(sketch, "E12.30.0.4", {"start": v(467.63, 22.86) * mm, "mid": v(467.18, 22.72) * mm, "end": v(466.89, 22.34) * mm});
            skLineSegment(sketch, "E12.30.0.5", {"start": v(467.63, 22.86) * mm, "end": v(468.63, 22.86) * mm});
            skLineSegment(sketch, "E12.30.0.6", {"start": v(469.63, 22.86) * mm, "end": v(468.63, 22.86) * mm});
            skArc(sketch, "E12.30.0.7", {"start": v(470.37, 22.34) * mm, "mid": v(470.08, 22.72) * mm, "end": v(469.63, 22.86) * mm});
            skLineSegment(sketch, "E12.30.0.8", {"start": v(472.06, 17.71) * mm, "end": v(470.37, 22.34) * mm});
            skArc(sketch, "E12.30.0.9", {"start": v(472.44, 15.54) * mm, "mid": v(472.34, 16.65) * mm, "end": v(472.06, 17.71) * mm});
            skLineSegment(sketch, "E12.30.0.10", {"start": v(472.44, 12.7) * mm, "end": v(472.44, 15.54) * mm});
            skLineSegment(sketch, "E12.31.0.0", {"start": v(480.06, 12.7) * mm, "end": v(480.06, 15.54) * mm});
            skArc(sketch, "E12.31.0.1", {"start": v(480.44, 17.71) * mm, "mid": v(480.16, 16.65) * mm, "end": v(480.06, 15.54) * mm});
            skLineSegment(sketch, "E12.31.0.2", {"start": v(480.44, 17.71) * mm, "end": v(482.13, 22.34) * mm});
            skPoint(sketch, "E12.31.0.3", {"position": v(482.32, 22.86) * mm});
            skArc(sketch, "E12.31.0.4", {"start": v(482.87, 22.86) * mm, "mid": v(482.42, 22.72) * mm, "end": v(482.13, 22.34) * mm});
            skLineSegment(sketch, "E12.31.0.5", {"start": v(482.87, 22.86) * mm, "end": v(483.87, 22.86) * mm});
            skLineSegment(sketch, "E12.31.0.6", {"start": v(484.87, 22.86) * mm, "end": v(483.87, 22.86) * mm});
            skArc(sketch, "E12.31.0.7", {"start": v(485.61, 22.34) * mm, "mid": v(485.32, 22.72) * mm, "end": v(484.87, 22.86) * mm});
            skLineSegment(sketch, "E12.31.0.8", {"start": v(487.3, 17.71) * mm, "end": v(485.61, 22.34) * mm});
            skArc(sketch, "E12.31.0.9", {"start": v(487.68, 15.54) * mm, "mid": v(487.58, 16.65) * mm, "end": v(487.3, 17.71) * mm});
            skLineSegment(sketch, "E12.31.0.10", {"start": v(487.68, 12.7) * mm, "end": v(487.68, 15.54) * mm});
            skLineSegment(sketch, "E12.32.0.0", {"start": v(495.3, 12.7) * mm, "end": v(495.3, 15.54) * mm});
            skArc(sketch, "E12.32.0.1", {"start": v(495.68, 17.71) * mm, "mid": v(495.4, 16.65) * mm, "end": v(495.3, 15.54) * mm});
            skLineSegment(sketch, "E12.32.0.2", {"start": v(495.68, 17.71) * mm, "end": v(497.37, 22.34) * mm});
            skPoint(sketch, "E12.32.0.3", {"position": v(497.56, 22.86) * mm});
            skArc(sketch, "E12.32.0.4", {"start": v(498.11, 22.86) * mm, "mid": v(497.66, 22.72) * mm, "end": v(497.37, 22.34) * mm});
            skLineSegment(sketch, "E12.32.0.5", {"start": v(498.11, 22.86) * mm, "end": v(499.1, 22.86) * mm});
            skLineSegment(sketch, "E12.32.0.6", {"start": v(500.1, 22.86) * mm, "end": v(499.1, 22.86) * mm});
            skArc(sketch, "E12.32.0.7", {"start": v(500.85, 22.34) * mm, "mid": v(500.56, 22.72) * mm, "end": v(500.1, 22.86) * mm});
            skLineSegment(sketch, "E12.32.0.8", {"start": v(502.54, 17.71) * mm, "end": v(500.85, 22.34) * mm});
            skArc(sketch, "E12.32.0.9", {"start": v(502.92, 15.54) * mm, "mid": v(502.82, 16.65) * mm, "end": v(502.54, 17.71) * mm});
            skLineSegment(sketch, "E12.32.0.10", {"start": v(502.92, 12.7) * mm, "end": v(502.92, 15.54) * mm});
            skLineSegment(sketch, "E12.33.0.0", {"start": v(510.54, 12.7) * mm, "end": v(510.54, 15.54) * mm});
            skArc(sketch, "E12.33.0.1", {"start": v(510.92, 17.71) * mm, "mid": v(510.64, 16.65) * mm, "end": v(510.54, 15.54) * mm});
            skLineSegment(sketch, "E12.33.0.2", {"start": v(510.92, 17.71) * mm, "end": v(512.6, 22.34) * mm});
            skPoint(sketch, "E12.33.0.3", {"position": v(512.8, 22.86) * mm});
            skArc(sketch, "E12.33.0.4", {"start": v(513.35, 22.86) * mm, "mid": v(512.9, 22.72) * mm, "end": v(512.6, 22.34) * mm});
            skLineSegment(sketch, "E12.33.0.5", {"start": v(513.35, 22.86) * mm, "end": v(514.35, 22.86) * mm});
            skLineSegment(sketch, "E12.33.0.6", {"start": v(515.35, 22.86) * mm, "end": v(514.35, 22.86) * mm});
            skArc(sketch, "E12.33.0.7", {"start": v(516.1, 22.34) * mm, "mid": v(515.8, 22.72) * mm, "end": v(515.35, 22.86) * mm});
            skLineSegment(sketch, "E12.33.0.8", {"start": v(517.78, 17.71) * mm, "end": v(516.1, 22.34) * mm});
            skArc(sketch, "E12.33.0.9", {"start": v(518.16, 15.54) * mm, "mid": v(518.06, 16.65) * mm, "end": v(517.78, 17.71) * mm});
            skLineSegment(sketch, "E12.33.0.10", {"start": v(518.16, 12.7) * mm, "end": v(518.16, 15.54) * mm});
            skLineSegment(sketch, "E12.34.0.0", {"start": v(525.78, 12.7) * mm, "end": v(525.78, 15.54) * mm});
            skArc(sketch, "E12.34.0.1", {"start": v(526.16, 17.71) * mm, "mid": v(525.88, 16.65) * mm, "end": v(525.78, 15.54) * mm});
            skLineSegment(sketch, "E12.34.0.2", {"start": v(526.16, 17.71) * mm, "end": v(527.85, 22.34) * mm});
            skPoint(sketch, "E12.34.0.3", {"position": v(528.04, 22.86) * mm});
            skArc(sketch, "E12.34.0.4", {"start": v(528.6, 22.86) * mm, "mid": v(528.14, 22.72) * mm, "end": v(527.85, 22.34) * mm});
            skLineSegment(sketch, "E12.34.0.5", {"start": v(528.6, 22.86) * mm, "end": v(529.6, 22.86) * mm});
            skLineSegment(sketch, "E12.34.0.6", {"start": v(530.59, 22.86) * mm, "end": v(529.6, 22.86) * mm});
            skArc(sketch, "E12.34.0.7", {"start": v(531.33, 22.34) * mm, "mid": v(531.04, 22.72) * mm, "end": v(530.59, 22.86) * mm});
            skLineSegment(sketch, "E12.34.0.8", {"start": v(533.02, 17.71) * mm, "end": v(531.33, 22.34) * mm});
            skArc(sketch, "E12.34.0.9", {"start": v(533.4, 15.54) * mm, "mid": v(533.3, 16.65) * mm, "end": v(533.02, 17.71) * mm});
            skLineSegment(sketch, "E12.34.0.10", {"start": v(533.4, 12.7) * mm, "end": v(533.4, 15.54) * mm});
            skLineSegment(sketch, "E12.35.0.0", {"start": v(541.02, 12.7) * mm, "end": v(541.02, 15.54) * mm});
            skArc(sketch, "E12.35.0.1", {"start": v(541.4, 17.71) * mm, "mid": v(541.12, 16.65) * mm, "end": v(541.02, 15.54) * mm});
            skLineSegment(sketch, "E12.35.0.2", {"start": v(541.4, 17.71) * mm, "end": v(543.09, 22.34) * mm});
            skPoint(sketch, "E12.35.0.3", {"position": v(543.28, 22.86) * mm});
            skArc(sketch, "E12.35.0.4", {"start": v(543.83, 22.86) * mm, "mid": v(543.38, 22.72) * mm, "end": v(543.09, 22.34) * mm});
            skLineSegment(sketch, "E12.35.0.5", {"start": v(543.83, 22.86) * mm, "end": v(544.83, 22.86) * mm});
            skLineSegment(sketch, "E12.35.0.6", {"start": v(545.83, 22.86) * mm, "end": v(544.83, 22.86) * mm});
            skArc(sketch, "E12.35.0.7", {"start": v(546.57, 22.34) * mm, "mid": v(546.28, 22.72) * mm, "end": v(545.83, 22.86) * mm});
            skLineSegment(sketch, "E12.35.0.8", {"start": v(548.26, 17.71) * mm, "end": v(546.57, 22.34) * mm});
            skArc(sketch, "E12.35.0.9", {"start": v(548.64, 15.54) * mm, "mid": v(548.54, 16.65) * mm, "end": v(548.26, 17.71) * mm});
            skLineSegment(sketch, "E12.35.0.10", {"start": v(548.64, 12.7) * mm, "end": v(548.64, 15.54) * mm});
            skLineSegment(sketch, "E12.36.0.0", {"start": v(556.26, 12.7) * mm, "end": v(556.26, 15.54) * mm});
            skArc(sketch, "E12.36.0.1", {"start": v(556.64, 17.71) * mm, "mid": v(556.36, 16.65) * mm, "end": v(556.26, 15.54) * mm});
            skLineSegment(sketch, "E12.36.0.2", {"start": v(556.64, 17.71) * mm, "end": v(558.33, 22.34) * mm});
            skPoint(sketch, "E12.36.0.3", {"position": v(558.52, 22.86) * mm});
            skArc(sketch, "E12.36.0.4", {"start": v(559.07, 22.86) * mm, "mid": v(558.62, 22.72) * mm, "end": v(558.33, 22.34) * mm});
            skLineSegment(sketch, "E12.36.0.5", {"start": v(559.07, 22.86) * mm, "end": v(560.07, 22.86) * mm});
            skLineSegment(sketch, "E12.36.0.6", {"start": v(561.07, 22.86) * mm, "end": v(560.07, 22.86) * mm});
            skArc(sketch, "E12.36.0.7", {"start": v(561.81, 22.34) * mm, "mid": v(561.52, 22.72) * mm, "end": v(561.07, 22.86) * mm});
            skLineSegment(sketch, "E12.36.0.8", {"start": v(563.5, 17.71) * mm, "end": v(561.81, 22.34) * mm});
            skArc(sketch, "E12.36.0.9", {"start": v(563.88, 15.54) * mm, "mid": v(563.78, 16.65) * mm, "end": v(563.5, 17.71) * mm});
            skLineSegment(sketch, "E12.36.0.10", {"start": v(563.88, 12.7) * mm, "end": v(563.88, 15.54) * mm});
            skLineSegment(sketch, "E12.37.0.0", {"start": v(571.5, 12.7) * mm, "end": v(571.5, 15.54) * mm});
            skArc(sketch, "E12.37.0.1", {"start": v(571.88, 17.71) * mm, "mid": v(571.6, 16.65) * mm, "end": v(571.5, 15.54) * mm});
            skLineSegment(sketch, "E12.37.0.2", {"start": v(571.88, 17.71) * mm, "end": v(573.57, 22.34) * mm});
            skPoint(sketch, "E12.37.0.3", {"position": v(573.76, 22.86) * mm});
            skArc(sketch, "E12.37.0.4", {"start": v(574.31, 22.86) * mm, "mid": v(573.86, 22.72) * mm, "end": v(573.57, 22.34) * mm});
            skLineSegment(sketch, "E12.37.0.5", {"start": v(574.31, 22.86) * mm, "end": v(575.3, 22.86) * mm});
            skLineSegment(sketch, "E12.37.0.6", {"start": v(576.3, 22.86) * mm, "end": v(575.3, 22.86) * mm});
            skArc(sketch, "E12.37.0.7", {"start": v(577.05, 22.34) * mm, "mid": v(576.76, 22.72) * mm, "end": v(576.3, 22.86) * mm});
            skLineSegment(sketch, "E12.37.0.8", {"start": v(578.74, 17.71) * mm, "end": v(577.05, 22.34) * mm});
            skArc(sketch, "E12.37.0.9", {"start": v(579.12, 15.54) * mm, "mid": v(579.02, 16.65) * mm, "end": v(578.74, 17.71) * mm});
            skLineSegment(sketch, "E12.37.0.10", {"start": v(579.12, 12.7) * mm, "end": v(579.12, 15.54) * mm});
            skLineSegment(sketch, "E12.38.0.0", {"start": v(586.74, 12.7) * mm, "end": v(586.74, 15.54) * mm});
            skArc(sketch, "E12.38.0.1", {"start": v(587.12, 17.71) * mm, "mid": v(586.84, 16.65) * mm, "end": v(586.74, 15.54) * mm});
            skLineSegment(sketch, "E12.38.0.2", {"start": v(587.12, 17.71) * mm, "end": v(588.8, 22.34) * mm});
            skPoint(sketch, "E12.38.0.3", {"position": v(589, 22.86) * mm});
            skArc(sketch, "E12.38.0.4", {"start": v(589.55, 22.86) * mm, "mid": v(589.1, 22.72) * mm, "end": v(588.8, 22.34) * mm});
            skLineSegment(sketch, "E12.38.0.5", {"start": v(589.55, 22.86) * mm, "end": v(590.55, 22.86) * mm});
            skLineSegment(sketch, "E12.38.0.6", {"start": v(591.55, 22.86) * mm, "end": v(590.55, 22.86) * mm});
            skArc(sketch, "E12.38.0.7", {"start": v(592.3, 22.34) * mm, "mid": v(592, 22.72) * mm, "end": v(591.55, 22.86) * mm});
            skLineSegment(sketch, "E12.38.0.8", {"start": v(593.98, 17.71) * mm, "end": v(592.3, 22.34) * mm});
            skArc(sketch, "E12.38.0.9", {"start": v(594.36, 15.54) * mm, "mid": v(594.26, 16.65) * mm, "end": v(593.98, 17.71) * mm});
            skLineSegment(sketch, "E12.38.0.10", {"start": v(594.36, 12.7) * mm, "end": v(594.36, 15.54) * mm});
            skLineSegment(sketch, "E12.39.0.0", {"start": v(601.98, 12.7) * mm, "end": v(601.98, 15.54) * mm});
            skArc(sketch, "E12.39.0.1", {"start": v(602.36, 17.71) * mm, "mid": v(602.08, 16.65) * mm, "end": v(601.98, 15.54) * mm});
            skLineSegment(sketch, "E12.39.0.2", {"start": v(602.36, 17.71) * mm, "end": v(604.05, 22.34) * mm});
            skPoint(sketch, "E12.39.0.3", {"position": v(604.24, 22.86) * mm});
            skArc(sketch, "E12.39.0.4", {"start": v(604.8, 22.86) * mm, "mid": v(604.34, 22.72) * mm, "end": v(604.05, 22.34) * mm});
            skLineSegment(sketch, "E12.39.0.5", {"start": v(604.8, 22.86) * mm, "end": v(605.8, 22.86) * mm});
            skLineSegment(sketch, "E12.39.0.6", {"start": v(606.79, 22.86) * mm, "end": v(605.8, 22.86) * mm});
            skArc(sketch, "E12.39.0.7", {"start": v(607.53, 22.34) * mm, "mid": v(607.24, 22.72) * mm, "end": v(606.79, 22.86) * mm});
            skLineSegment(sketch, "E12.39.0.8", {"start": v(609.22, 17.71) * mm, "end": v(607.53, 22.34) * mm});
            skArc(sketch, "E12.39.0.9", {"start": v(609.6, 15.54) * mm, "mid": v(609.5, 16.65) * mm, "end": v(609.22, 17.71) * mm});
            skLineSegment(sketch, "E12.39.0.10", {"start": v(609.6, 12.7) * mm, "end": v(609.6, 15.54) * mm});
            skLineSegment(sketch, "E12.40.0.0", {"start": v(617.22, 12.7) * mm, "end": v(617.22, 15.54) * mm});
            skArc(sketch, "E12.40.0.1", {"start": v(617.6, 17.71) * mm, "mid": v(617.32, 16.65) * mm, "end": v(617.22, 15.54) * mm});
            skLineSegment(sketch, "E12.40.0.2", {"start": v(617.6, 17.71) * mm, "end": v(619.29, 22.34) * mm});
            skPoint(sketch, "E12.40.0.3", {"position": v(619.48, 22.86) * mm});
            skArc(sketch, "E12.40.0.4", {"start": v(620.03, 22.86) * mm, "mid": v(619.58, 22.72) * mm, "end": v(619.29, 22.34) * mm});
            skLineSegment(sketch, "E12.40.0.5", {"start": v(620.03, 22.86) * mm, "end": v(621.03, 22.86) * mm});
            skLineSegment(sketch, "E12.40.0.6", {"start": v(622.03, 22.86) * mm, "end": v(621.03, 22.86) * mm});
            skArc(sketch, "E12.40.0.7", {"start": v(622.77, 22.34) * mm, "mid": v(622.48, 22.72) * mm, "end": v(622.03, 22.86) * mm});
            skLineSegment(sketch, "E12.40.0.8", {"start": v(624.46, 17.71) * mm, "end": v(622.77, 22.34) * mm});
            skArc(sketch, "E12.40.0.9", {"start": v(624.84, 15.54) * mm, "mid": v(624.74, 16.65) * mm, "end": v(624.46, 17.71) * mm});
            skLineSegment(sketch, "E12.40.0.10", {"start": v(624.84, 12.7) * mm, "end": v(624.84, 15.54) * mm});
            skLineSegment(sketch, "E12.41.0.0", {"start": v(632.46, 12.7) * mm, "end": v(632.46, 15.54) * mm});
            skArc(sketch, "E12.41.0.1", {"start": v(632.84, 17.71) * mm, "mid": v(632.56, 16.65) * mm, "end": v(632.46, 15.54) * mm});
            skLineSegment(sketch, "E12.41.0.2", {"start": v(632.84, 17.71) * mm, "end": v(634.53, 22.34) * mm});
            skPoint(sketch, "E12.41.0.3", {"position": v(634.72, 22.86) * mm});
            skArc(sketch, "E12.41.0.4", {"start": v(635.27, 22.86) * mm, "mid": v(634.82, 22.72) * mm, "end": v(634.53, 22.34) * mm});
            skLineSegment(sketch, "E12.41.0.5", {"start": v(635.27, 22.86) * mm, "end": v(636.27, 22.86) * mm});
            skLineSegment(sketch, "E12.41.0.6", {"start": v(637.27, 22.86) * mm, "end": v(636.27, 22.86) * mm});
            skArc(sketch, "E12.41.0.7", {"start": v(638.01, 22.34) * mm, "mid": v(637.72, 22.72) * mm, "end": v(637.27, 22.86) * mm});
            skLineSegment(sketch, "E12.41.0.8", {"start": v(639.7, 17.71) * mm, "end": v(638.01, 22.34) * mm});
            skArc(sketch, "E12.41.0.9", {"start": v(640.08, 15.54) * mm, "mid": v(639.98, 16.65) * mm, "end": v(639.7, 17.71) * mm});
            skLineSegment(sketch, "E12.41.0.10", {"start": v(640.08, 12.7) * mm, "end": v(640.08, 15.54) * mm});
            skLineSegment(sketch, "E12.42.0.0", {"start": v(647.7, 12.7) * mm, "end": v(647.7, 15.54) * mm});
            skArc(sketch, "E12.42.0.1", {"start": v(648.08, 17.71) * mm, "mid": v(647.8, 16.65) * mm, "end": v(647.7, 15.54) * mm});
            skLineSegment(sketch, "E12.42.0.2", {"start": v(648.08, 17.71) * mm, "end": v(649.77, 22.34) * mm});
            skPoint(sketch, "E12.42.0.3", {"position": v(649.96, 22.86) * mm});
            skArc(sketch, "E12.42.0.4", {"start": v(650.51, 22.86) * mm, "mid": v(650.06, 22.72) * mm, "end": v(649.77, 22.34) * mm});
            skLineSegment(sketch, "E12.42.0.5", {"start": v(650.51, 22.86) * mm, "end": v(651.5, 22.86) * mm});
            skLineSegment(sketch, "E12.42.0.6", {"start": v(652.5, 22.86) * mm, "end": v(651.5, 22.86) * mm});
            skArc(sketch, "E12.42.0.7", {"start": v(653.25, 22.34) * mm, "mid": v(652.96, 22.72) * mm, "end": v(652.5, 22.86) * mm});
            skLineSegment(sketch, "E12.42.0.8", {"start": v(654.94, 17.71) * mm, "end": v(653.25, 22.34) * mm});
            skArc(sketch, "E12.42.0.9", {"start": v(655.32, 15.54) * mm, "mid": v(655.22, 16.65) * mm, "end": v(654.94, 17.71) * mm});
            skLineSegment(sketch, "E12.42.0.10", {"start": v(655.32, 12.7) * mm, "end": v(655.32, 15.54) * mm});
            skLineSegment(sketch, "E12.43.0.0", {"start": v(662.94, 12.7) * mm, "end": v(662.94, 15.54) * mm});
            skArc(sketch, "E12.43.0.1", {"start": v(663.32, 17.71) * mm, "mid": v(663.04, 16.65) * mm, "end": v(662.94, 15.54) * mm});
            skLineSegment(sketch, "E12.43.0.2", {"start": v(663.32, 17.71) * mm, "end": v(665, 22.34) * mm});
            skPoint(sketch, "E12.43.0.3", {"position": v(665.2, 22.86) * mm});
            skArc(sketch, "E12.43.0.4", {"start": v(665.75, 22.86) * mm, "mid": v(665.3, 22.72) * mm, "end": v(665, 22.34) * mm});
            skLineSegment(sketch, "E12.43.0.5", {"start": v(665.75, 22.86) * mm, "end": v(666.75, 22.86) * mm});
            skLineSegment(sketch, "E12.43.0.6", {"start": v(667.75, 22.86) * mm, "end": v(666.75, 22.86) * mm});
            skArc(sketch, "E12.43.0.7", {"start": v(668.5, 22.34) * mm, "mid": v(668.2, 22.72) * mm, "end": v(667.75, 22.86) * mm});
            skLineSegment(sketch, "E12.43.0.8", {"start": v(670.18, 17.71) * mm, "end": v(668.5, 22.34) * mm});
            skArc(sketch, "E12.43.0.9", {"start": v(670.56, 15.54) * mm, "mid": v(670.46, 16.65) * mm, "end": v(670.18, 17.71) * mm});
            skLineSegment(sketch, "E12.43.0.10", {"start": v(670.56, 12.7) * mm, "end": v(670.56, 15.54) * mm});
            skLineSegment(sketch, "E12.44.0.0", {"start": v(678.18, 12.7) * mm, "end": v(678.18, 15.54) * mm});
            skArc(sketch, "E12.44.0.1", {"start": v(678.56, 17.71) * mm, "mid": v(678.28, 16.65) * mm, "end": v(678.18, 15.54) * mm});
            skLineSegment(sketch, "E12.44.0.2", {"start": v(678.56, 17.71) * mm, "end": v(680.25, 22.34) * mm});
            skPoint(sketch, "E12.44.0.3", {"position": v(680.44, 22.86) * mm});
            skArc(sketch, "E12.44.0.4", {"start": v(681, 22.86) * mm, "mid": v(680.54, 22.72) * mm, "end": v(680.25, 22.34) * mm});
            skLineSegment(sketch, "E12.44.0.5", {"start": v(681, 22.86) * mm, "end": v(682, 22.86) * mm});
            skLineSegment(sketch, "E12.44.0.6", {"start": v(682.99, 22.86) * mm, "end": v(682, 22.86) * mm});
            skArc(sketch, "E12.44.0.7", {"start": v(683.73, 22.34) * mm, "mid": v(683.44, 22.72) * mm, "end": v(682.99, 22.86) * mm});
            skLineSegment(sketch, "E12.44.0.8", {"start": v(685.42, 17.71) * mm, "end": v(683.73, 22.34) * mm});
            skArc(sketch, "E12.44.0.9", {"start": v(685.8, 15.54) * mm, "mid": v(685.7, 16.65) * mm, "end": v(685.42, 17.71) * mm});
            skLineSegment(sketch, "E12.44.0.10", {"start": v(685.8, 12.7) * mm, "end": v(685.8, 15.54) * mm});
            skLineSegment(sketch, "E12.45.0.0", {"start": v(693.42, 12.7) * mm, "end": v(693.42, 15.54) * mm});
            skArc(sketch, "E12.45.0.1", {"start": v(693.8, 17.71) * mm, "mid": v(693.52, 16.65) * mm, "end": v(693.42, 15.54) * mm});
            skLineSegment(sketch, "E12.45.0.2", {"start": v(693.8, 17.71) * mm, "end": v(695.49, 22.34) * mm});
            skPoint(sketch, "E12.45.0.3", {"position": v(695.68, 22.86) * mm});
            skArc(sketch, "E12.45.0.4", {"start": v(696.23, 22.86) * mm, "mid": v(695.78, 22.72) * mm, "end": v(695.49, 22.34) * mm});
            skLineSegment(sketch, "E12.45.0.5", {"start": v(696.23, 22.86) * mm, "end": v(697.23, 22.86) * mm});
            skLineSegment(sketch, "E12.45.0.6", {"start": v(698.23, 22.86) * mm, "end": v(697.23, 22.86) * mm});
            skArc(sketch, "E12.45.0.7", {"start": v(698.97, 22.34) * mm, "mid": v(698.68, 22.72) * mm, "end": v(698.23, 22.86) * mm});
            skLineSegment(sketch, "E12.45.0.8", {"start": v(700.66, 17.71) * mm, "end": v(698.97, 22.34) * mm});
            skArc(sketch, "E12.45.0.9", {"start": v(701.04, 15.54) * mm, "mid": v(700.94, 16.65) * mm, "end": v(700.66, 17.71) * mm});
            skLineSegment(sketch, "E12.45.0.10", {"start": v(701.04, 12.7) * mm, "end": v(701.04, 15.54) * mm});
            skLineSegment(sketch, "E12.46.0.0", {"start": v(708.66, 12.7) * mm, "end": v(708.66, 15.54) * mm});
            skArc(sketch, "E12.46.0.1", {"start": v(709.04, 17.71) * mm, "mid": v(708.76, 16.65) * mm, "end": v(708.66, 15.54) * mm});
            skLineSegment(sketch, "E12.46.0.2", {"start": v(709.04, 17.71) * mm, "end": v(710.73, 22.34) * mm});
            skPoint(sketch, "E12.46.0.3", {"position": v(710.92, 22.86) * mm});
            skArc(sketch, "E12.46.0.4", {"start": v(711.47, 22.86) * mm, "mid": v(711.02, 22.72) * mm, "end": v(710.73, 22.34) * mm});
            skLineSegment(sketch, "E12.46.0.5", {"start": v(711.47, 22.86) * mm, "end": v(712.47, 22.86) * mm});
            skLineSegment(sketch, "E12.46.0.6", {"start": v(713.47, 22.86) * mm, "end": v(712.47, 22.86) * mm});
            skArc(sketch, "E12.46.0.7", {"start": v(714.21, 22.34) * mm, "mid": v(713.92, 22.72) * mm, "end": v(713.47, 22.86) * mm});
            skLineSegment(sketch, "E12.46.0.8", {"start": v(715.9, 17.71) * mm, "end": v(714.21, 22.34) * mm});
            skArc(sketch, "E12.46.0.9", {"start": v(716.28, 15.54) * mm, "mid": v(716.18, 16.65) * mm, "end": v(715.9, 17.71) * mm});
            skLineSegment(sketch, "E12.46.0.10", {"start": v(716.28, 12.7) * mm, "end": v(716.28, 15.54) * mm});
            skLineSegment(sketch, "E12.47.0.0", {"start": v(723.9, 12.7) * mm, "end": v(723.9, 15.54) * mm});
            skArc(sketch, "E12.47.0.1", {"start": v(724.28, 17.71) * mm, "mid": v(724, 16.65) * mm, "end": v(723.9, 15.54) * mm});
            skLineSegment(sketch, "E12.47.0.2", {"start": v(724.28, 17.71) * mm, "end": v(725.97, 22.34) * mm});
            skPoint(sketch, "E12.47.0.3", {"position": v(726.16, 22.86) * mm});
            skArc(sketch, "E12.47.0.4", {"start": v(726.71, 22.86) * mm, "mid": v(726.26, 22.72) * mm, "end": v(725.97, 22.34) * mm});
            skLineSegment(sketch, "E12.47.0.5", {"start": v(726.71, 22.86) * mm, "end": v(727.7, 22.86) * mm});
            skLineSegment(sketch, "E12.47.0.6", {"start": v(728.7, 22.86) * mm, "end": v(727.7, 22.86) * mm});
            skArc(sketch, "E12.47.0.7", {"start": v(729.45, 22.34) * mm, "mid": v(729.16, 22.72) * mm, "end": v(728.7, 22.86) * mm});
            skLineSegment(sketch, "E12.47.0.8", {"start": v(731.14, 17.71) * mm, "end": v(729.45, 22.34) * mm});
            skArc(sketch, "E12.47.0.9", {"start": v(731.52, 15.54) * mm, "mid": v(731.42, 16.65) * mm, "end": v(731.14, 17.71) * mm});
            skLineSegment(sketch, "E12.47.0.10", {"start": v(731.52, 12.7) * mm, "end": v(731.52, 15.54) * mm});
            skLineSegment(sketch, "E12.48.0.0", {"start": v(739.14, 12.7) * mm, "end": v(739.14, 15.54) * mm});
            skArc(sketch, "E12.48.0.1", {"start": v(739.52, 17.71) * mm, "mid": v(739.24, 16.65) * mm, "end": v(739.14, 15.54) * mm});
            skLineSegment(sketch, "E12.48.0.2", {"start": v(739.52, 17.71) * mm, "end": v(741.2, 22.34) * mm});
            skPoint(sketch, "E12.48.0.3", {"position": v(741.4, 22.86) * mm});
            skArc(sketch, "E12.48.0.4", {"start": v(741.95, 22.86) * mm, "mid": v(741.5, 22.72) * mm, "end": v(741.2, 22.34) * mm});
            skLineSegment(sketch, "E12.48.0.5", {"start": v(741.95, 22.86) * mm, "end": v(742.95, 22.86) * mm});
            skLineSegment(sketch, "E12.48.0.6", {"start": v(743.95, 22.86) * mm, "end": v(742.95, 22.86) * mm});
            skArc(sketch, "E12.48.0.7", {"start": v(744.7, 22.34) * mm, "mid": v(744.4, 22.72) * mm, "end": v(743.95, 22.86) * mm});
            skLineSegment(sketch, "E12.48.0.8", {"start": v(746.38, 17.71) * mm, "end": v(744.7, 22.34) * mm});
            skArc(sketch, "E12.48.0.9", {"start": v(746.76, 15.54) * mm, "mid": v(746.66, 16.65) * mm, "end": v(746.38, 17.71) * mm});
            skLineSegment(sketch, "E12.48.0.10", {"start": v(746.76, 12.7) * mm, "end": v(746.76, 15.54) * mm});
            skLineSegment(sketch, "E12.49.0.0", {"start": v(754.38, 12.7) * mm, "end": v(754.38, 15.54) * mm});
            skArc(sketch, "E12.49.0.1", {"start": v(754.76, 17.71) * mm, "mid": v(754.48, 16.65) * mm, "end": v(754.38, 15.54) * mm});
            skLineSegment(sketch, "E12.49.0.2", {"start": v(754.76, 17.71) * mm, "end": v(756.45, 22.34) * mm});
            skPoint(sketch, "E12.49.0.3", {"position": v(756.64, 22.86) * mm});
            skArc(sketch, "E12.49.0.4", {"start": v(757.2, 22.86) * mm, "mid": v(756.74, 22.72) * mm, "end": v(756.45, 22.34) * mm});
            skLineSegment(sketch, "E12.49.0.5", {"start": v(757.2, 22.86) * mm, "end": v(758.19, 22.86) * mm});
            skLineSegment(sketch, "E12.49.0.6", {"start": v(759.19, 22.86) * mm, "end": v(758.19, 22.86) * mm});
            skArc(sketch, "E12.49.0.7", {"start": v(759.93, 22.34) * mm, "mid": v(759.64, 22.72) * mm, "end": v(759.19, 22.86) * mm});
            skLineSegment(sketch, "E12.49.0.8", {"start": v(761.62, 17.71) * mm, "end": v(759.93, 22.34) * mm});
            skArc(sketch, "E12.49.0.9", {"start": v(762, 15.54) * mm, "mid": v(761.9, 16.65) * mm, "end": v(761.62, 17.71) * mm});
            skLineSegment(sketch, "E12.49.0.10", {"start": v(762, 12.7) * mm, "end": v(762, 15.54) * mm});
            skLineSegment(sketch, "E12.direction1", {"start": v(7.62, 12.7) * mm, "end": v(22.86, 12.7) * mm, "construction": true});
            skSolve(sketch);
        }
        {
            var Q0;
            Q0 = qSketchRegion(id + "F0", true);
            var Q1;
            Q1=makeQuery(id+"F0.imprint","IMPRINT",FACE,{"disambiguationData":[TD([[makeQuery(id+"F0.imprint","IMPRINT",EDGE,{"derivedFrom":sQuery(id+"F0.wireOp",EDGE,"E0.bottom")}),1.0]])]});
            extrude(context, id + "F1", {"entities" : qUnion([Q0, Q1]), "depth" : 127 * mm});
        }
        {
            var Q0;
            Q0=makeQuery(id+"F1.opExtrude","CAP_FACE",FACE,{"disambiguationData":[OSD([sQuery(id+"F0.wireOp",EDGE,"E0.bottom"),sQuery(id+"F0.wireOp",EDGE,"E0.top"),sQuery(id+"F0.wireOp",EDGE,"E0.left"),sQuery(id+"F0.wireOp",EDGE,"E0.right"),sQuery(id+"F0.wireOp",EDGE,"E1"),sQuery(id+"F0.wireOp",EDGE,"E2"),sQuery(id+"F0.wireOp",EDGE,"E4"),sQuery(id+"F0.wireOp",EDGE,"E5.MirrorCS"),sQuery(id+"F0.wireOp",EDGE,"E6.MirrorCS"),sQuery(id+"F0.wireOp",EDGE,"E7.MirrorCS"),sQuery(id+"F0.wireOp",EDGE,"E8.filletArc"),sQuery(id+"F0.wireOp",EDGE,"E9.filletArc"),sQuery(id+"F0.wireOp",EDGE,"E10.filletArc"),sQuery(id+"F0.wireOp",EDGE,"E11.filletArc"),sQuery(id+"F0.wireOp",EDGE,"E12.1.0.0"),sQuery(id+"F0.wireOp",EDGE,"E12.1.0.1"),sQuery(id+"F0.wireOp",EDGE,"E12.1.0.2"),sQuery(id+"F0.wireOp",EDGE,"E12.1.0.4"),sQuery(id+"F0.wireOp",EDGE,"E12.1.0.5"),sQuery(id+"F0.wireOp",EDGE,"E12.1.0.6"),sQuery(id+"F0.wireOp",EDGE,"E12.1.0.7"),sQuery(id+"F0.wireOp",EDGE,"E12.1.0.8"),sQuery(id+"F0.wireOp",EDGE,"E12.1.0.9"),sQuery(id+"F0.wireOp",EDGE,"E12.1.0.10"),sQuery(id+"F0.wireOp",EDGE,"E12.2.0.0"),sQuery(id+"F0.wireOp",EDGE,"E12.2.0.1"),sQuery(id+"F0.wireOp",EDGE,"E12.2.0.2"),sQuery(id+"F0.wireOp",EDGE,"E12.2.0.4"),sQuery(id+"F0.wireOp",EDGE,"E12.2.0.5"),sQuery(id+"F0.wireOp",EDGE,"E12.2.0.6"),sQuery(id+"F0.wireOp",EDGE,"E12.2.0.7"),sQuery(id+"F0.wireOp",EDGE,"E12.2.0.8"),sQuery(id+"F0.wireOp",EDGE,"E12.2.0.9"),sQuery(id+"F0.wireOp",EDGE,"E12.2.0.10"),sQuery(id+"F0.wireOp",EDGE,"E12.3.0.0"),sQuery(id+"F0.wireOp",EDGE,"E12.3.0.1"),sQuery(id+"F0.wireOp",EDGE,"E12.3.0.2"),sQuery(id+"F0.wireOp",EDGE,"E12.3.0.4"),sQuery(id+"F0.wireOp",EDGE,"E12.3.0.5"),sQuery(id+"F0.wireOp",EDGE,"E12.3.0.6"),sQuery(id+"F0.wireOp",EDGE,"E12.3.0.7"),sQuery(id+"F0.wireOp",EDGE,"E12.3.0.8"),sQuery(id+"F0.wireOp",EDGE,"E12.3.0.9"),sQuery(id+"F0.wireOp",EDGE,"E12.3.0.10"),sQuery(id+"F0.wireOp",EDGE,"E12.4.0.0"),sQuery(id+"F0.wireOp",EDGE,"E12.4.0.1"),sQuery(id+"F0.wireOp",EDGE,"E12.4.0.2"),sQuery(id+"F0.wireOp",EDGE,"E12.4.0.4"),sQuery(id+"F0.wireOp",EDGE,"E12.4.0.5"),sQuery(id+"F0.wireOp",EDGE,"E12.4.0.6"),sQuery(id+"F0.wireOp",EDGE,"E12.4.0.7"),sQuery(id+"F0.wireOp",EDGE,"E12.4.0.8"),sQuery(id+"F0.wireOp",EDGE,"E12.4.0.9"),sQuery(id+"F0.wireOp",EDGE,"E12.4.0.10"),sQuery(id+"F0.wireOp",EDGE,"E12.5.0.0"),sQuery(id+"F0.wireOp",EDGE,"E12.5.0.1"),sQuery(id+"F0.wireOp",EDGE,"E12.5.0.2"),sQuery(id+"F0.wireOp",EDGE,"E12.5.0.4"),sQuery(id+"F0.wireOp",EDGE,"E12.5.0.5"),sQuery(id+"F0.wireOp",EDGE,"E12.5.0.6"),sQuery(id+"F0.wireOp",EDGE,"E12.5.0.7"),sQuery(id+"F0.wireOp",EDGE,"E12.5.0.8"),sQuery(id+"F0.wireOp",EDGE,"E12.5.0.9"),sQuery(id+"F0.wireOp",EDGE,"E12.5.0.10"),sQuery(id+"F0.wireOp",EDGE,"E12.6.0.0"),sQuery(id+"F0.wireOp",EDGE,"E12.6.0.1"),sQuery(id+"F0.wireOp",EDGE,"E12.6.0.2"),sQuery(id+"F0.wireOp",EDGE,"E12.6.0.4"),sQuery(id+"F0.wireOp",EDGE,"E12.6.0.5"),sQuery(id+"F0.wireOp",EDGE,"E12.6.0.6"),sQuery(id+"F0.wireOp",EDGE,"E12.6.0.7"),sQuery(id+"F0.wireOp",EDGE,"E12.6.0.8"),sQuery(id+"F0.wireOp",EDGE,"E12.6.0.9"),sQuery(id+"F0.wireOp",EDGE,"E12.6.0.10"),sQuery(id+"F0.wireOp",EDGE,"E12.7.0.0"),sQuery(id+"F0.wireOp",EDGE,"E12.7.0.1"),sQuery(id+"F0.wireOp",EDGE,"E12.7.0.2"),sQuery(id+"F0.wireOp",EDGE,"E12.7.0.4"),sQuery(id+"F0.wireOp",EDGE,"E12.7.0.5"),sQuery(id+"F0.wireOp",EDGE,"E12.7.0.6"),sQuery(id+"F0.wireOp",EDGE,"E12.7.0.7"),sQuery(id+"F0.wireOp",EDGE,"E12.7.0.8"),sQuery(id+"F0.wireOp",EDGE,"E12.7.0.9"),sQuery(id+"F0.wireOp",EDGE,"E12.7.0.10"),sQuery(id+"F0.wireOp",EDGE,"E12.8.0.0"),sQuery(id+"F0.wireOp",EDGE,"E12.8.0.1"),sQuery(id+"F0.wireOp",EDGE,"E12.8.0.2"),sQuery(id+"F0.wireOp",EDGE,"E12.8.0.4"),sQuery(id+"F0.wireOp",EDGE,"E12.8.0.5"),sQuery(id+"F0.wireOp",EDGE,"E12.8.0.6"),sQuery(id+"F0.wireOp",EDGE,"E12.8.0.7"),sQuery(id+"F0.wireOp",EDGE,"E12.8.0.8"),sQuery(id+"F0.wireOp",EDGE,"E12.8.0.9"),sQuery(id+"F0.wireOp",EDGE,"E12.8.0.10"),sQuery(id+"F0.wireOp",EDGE,"E12.9.0.0"),sQuery(id+"F0.wireOp",EDGE,"E12.9.0.1"),sQuery(id+"F0.wireOp",EDGE,"E12.9.0.2"),sQuery(id+"F0.wireOp",EDGE,"E12.9.0.4"),sQuery(id+"F0.wireOp",EDGE,"E12.9.0.5"),sQuery(id+"F0.wireOp",EDGE,"E12.9.0.6"),sQuery(id+"F0.wireOp",EDGE,"E12.9.0.7"),sQuery(id+"F0.wireOp",EDGE,"E12.9.0.8"),sQuery(id+"F0.wireOp",EDGE,"E12.9.0.9"),sQuery(id+"F0.wireOp",EDGE,"E12.9.0.10"),sQuery(id+"F0.wireOp",EDGE,"E12.10.0.0"),sQuery(id+"F0.wireOp",EDGE,"E12.10.0.1"),sQuery(id+"F0.wireOp",EDGE,"E12.10.0.2"),sQuery(id+"F0.wireOp",EDGE,"E12.10.0.4"),sQuery(id+"F0.wireOp",EDGE,"E12.10.0.5"),sQuery(id+"F0.wireOp",EDGE,"E12.10.0.6"),sQuery(id+"F0.wireOp",EDGE,"E12.10.0.7"),sQuery(id+"F0.wireOp",EDGE,"E12.10.0.8"),sQuery(id+"F0.wireOp",EDGE,"E12.10.0.9"),sQuery(id+"F0.wireOp",EDGE,"E12.10.0.10"),sQuery(id+"F0.wireOp",EDGE,"E12.11.0.0"),sQuery(id+"F0.wireOp",EDGE,"E12.11.0.1"),sQuery(id+"F0.wireOp",EDGE,"E12.11.0.2"),sQuery(id+"F0.wireOp",EDGE,"E12.11.0.4"),sQuery(id+"F0.wireOp",EDGE,"E12.11.0.5"),sQuery(id+"F0.wireOp",EDGE,"E12.11.0.6"),sQuery(id+"F0.wireOp",EDGE,"E12.11.0.7"),sQuery(id+"F0.wireOp",EDGE,"E12.11.0.8"),sQuery(id+"F0.wireOp",EDGE,"E12.11.0.9"),sQuery(id+"F0.wireOp",EDGE,"E12.11.0.10"),sQuery(id+"F0.wireOp",EDGE,"E12.12.0.0"),sQuery(id+"F0.wireOp",EDGE,"E12.12.0.1"),sQuery(id+"F0.wireOp",EDGE,"E12.12.0.2"),sQuery(id+"F0.wireOp",EDGE,"E12.12.0.4"),sQuery(id+"F0.wireOp",EDGE,"E12.12.0.5"),sQuery(id+"F0.wireOp",EDGE,"E12.12.0.6"),sQuery(id+"F0.wireOp",EDGE,"E12.12.0.7"),sQuery(id+"F0.wireOp",EDGE,"E12.12.0.8"),sQuery(id+"F0.wireOp",EDGE,"E12.12.0.9"),sQuery(id+"F0.wireOp",EDGE,"E12.12.0.10"),sQuery(id+"F0.wireOp",EDGE,"E12.13.0.0"),sQuery(id+"F0.wireOp",EDGE,"E12.13.0.1"),sQuery(id+"F0.wireOp",EDGE,"E12.13.0.2"),sQuery(id+"F0.wireOp",EDGE,"E12.13.0.4"),sQuery(id+"F0.wireOp",EDGE,"E12.13.0.5"),sQuery(id+"F0.wireOp",EDGE,"E12.13.0.6"),sQuery(id+"F0.wireOp",EDGE,"E12.13.0.7"),sQuery(id+"F0.wireOp",EDGE,"E12.13.0.8"),sQuery(id+"F0.wireOp",EDGE,"E12.13.0.9"),sQuery(id+"F0.wireOp",EDGE,"E12.13.0.10"),sQuery(id+"F0.wireOp",EDGE,"E12.14.0.0"),sQuery(id+"F0.wireOp",EDGE,"E12.14.0.1"),sQuery(id+"F0.wireOp",EDGE,"E12.14.0.2"),sQuery(id+"F0.wireOp",EDGE,"E12.14.0.4"),sQuery(id+"F0.wireOp",EDGE,"E12.14.0.5"),sQuery(id+"F0.wireOp",EDGE,"E12.14.0.6"),sQuery(id+"F0.wireOp",EDGE,"E12.14.0.7"),sQuery(id+"F0.wireOp",EDGE,"E12.14.0.8"),sQuery(id+"F0.wireOp",EDGE,"E12.14.0.9"),sQuery(id+"F0.wireOp",EDGE,"E12.14.0.10"),sQuery(id+"F0.wireOp",EDGE,"E12.15.0.0"),sQuery(id+"F0.wireOp",EDGE,"E12.15.0.1"),sQuery(id+"F0.wireOp",EDGE,"E12.15.0.2"),sQuery(id+"F0.wireOp",EDGE,"E12.15.0.4"),sQuery(id+"F0.wireOp",EDGE,"E12.15.0.5"),sQuery(id+"F0.wireOp",EDGE,"E12.15.0.6"),sQuery(id+"F0.wireOp",EDGE,"E12.15.0.7"),sQuery(id+"F0.wireOp",EDGE,"E12.15.0.8"),sQuery(id+"F0.wireOp",EDGE,"E12.15.0.9"),sQuery(id+"F0.wireOp",EDGE,"E12.15.0.10"),sQuery(id+"F0.wireOp",EDGE,"E12.16.0.0"),sQuery(id+"F0.wireOp",EDGE,"E12.16.0.1"),sQuery(id+"F0.wireOp",EDGE,"E12.16.0.2"),sQuery(id+"F0.wireOp",EDGE,"E12.16.0.4"),sQuery(id+"F0.wireOp",EDGE,"E12.16.0.5"),sQuery(id+"F0.wireOp",EDGE,"E12.16.0.6"),sQuery(id+"F0.wireOp",EDGE,"E12.16.0.7"),sQuery(id+"F0.wireOp",EDGE,"E12.16.0.8"),sQuery(id+"F0.wireOp",EDGE,"E12.16.0.9"),sQuery(id+"F0.wireOp",EDGE,"E12.16.0.10"),sQuery(id+"F0.wireOp",EDGE,"E12.17.0.0"),sQuery(id+"F0.wireOp",EDGE,"E12.17.0.1"),sQuery(id+"F0.wireOp",EDGE,"E12.17.0.2"),sQuery(id+"F0.wireOp",EDGE,"E12.17.0.4"),sQuery(id+"F0.wireOp",EDGE,"E12.17.0.5"),sQuery(id+"F0.wireOp",EDGE,"E12.17.0.6"),sQuery(id+"F0.wireOp",EDGE,"E12.17.0.7"),sQuery(id+"F0.wireOp",EDGE,"E12.17.0.8"),sQuery(id+"F0.wireOp",EDGE,"E12.17.0.9"),sQuery(id+"F0.wireOp",EDGE,"E12.17.0.10"),sQuery(id+"F0.wireOp",EDGE,"E12.18.0.0"),sQuery(id+"F0.wireOp",EDGE,"E12.18.0.1"),sQuery(id+"F0.wireOp",EDGE,"E12.18.0.2"),sQuery(id+"F0.wireOp",EDGE,"E12.18.0.4"),sQuery(id+"F0.wireOp",EDGE,"E12.18.0.5"),sQuery(id+"F0.wireOp",EDGE,"E12.18.0.6"),sQuery(id+"F0.wireOp",EDGE,"E12.18.0.7"),sQuery(id+"F0.wireOp",EDGE,"E12.18.0.8"),sQuery(id+"F0.wireOp",EDGE,"E12.18.0.9"),sQuery(id+"F0.wireOp",EDGE,"E12.18.0.10"),sQuery(id+"F0.wireOp",EDGE,"E12.19.0.0"),sQuery(id+"F0.wireOp",EDGE,"E12.19.0.1"),sQuery(id+"F0.wireOp",EDGE,"E12.19.0.2"),sQuery(id+"F0.wireOp",EDGE,"E12.19.0.4"),sQuery(id+"F0.wireOp",EDGE,"E12.19.0.5"),sQuery(id+"F0.wireOp",EDGE,"E12.19.0.6"),sQuery(id+"F0.wireOp",EDGE,"E12.19.0.7"),sQuery(id+"F0.wireOp",EDGE,"E12.19.0.8"),sQuery(id+"F0.wireOp",EDGE,"E12.19.0.9"),sQuery(id+"F0.wireOp",EDGE,"E12.19.0.10"),sQuery(id+"F0.wireOp",EDGE,"E12.20.0.0"),sQuery(id+"F0.wireOp",EDGE,"E12.20.0.1"),sQuery(id+"F0.wireOp",EDGE,"E12.20.0.2"),sQuery(id+"F0.wireOp",EDGE,"E12.20.0.4"),sQuery(id+"F0.wireOp",EDGE,"E12.20.0.5"),sQuery(id+"F0.wireOp",EDGE,"E12.20.0.6"),sQuery(id+"F0.wireOp",EDGE,"E12.20.0.7"),sQuery(id+"F0.wireOp",EDGE,"E12.20.0.8"),sQuery(id+"F0.wireOp",EDGE,"E12.20.0.9"),sQuery(id+"F0.wireOp",EDGE,"E12.20.0.10"),sQuery(id+"F0.wireOp",EDGE,"E12.21.0.0"),sQuery(id+"F0.wireOp",EDGE,"E12.21.0.1"),sQuery(id+"F0.wireOp",EDGE,"E12.21.0.2"),sQuery(id+"F0.wireOp",EDGE,"E12.21.0.4"),sQuery(id+"F0.wireOp",EDGE,"E12.21.0.5"),sQuery(id+"F0.wireOp",EDGE,"E12.21.0.6"),sQuery(id+"F0.wireOp",EDGE,"E12.21.0.7"),sQuery(id+"F0.wireOp",EDGE,"E12.21.0.8"),sQuery(id+"F0.wireOp",EDGE,"E12.21.0.9"),sQuery(id+"F0.wireOp",EDGE,"E12.21.0.10"),sQuery(id+"F0.wireOp",EDGE,"E12.22.0.0"),sQuery(id+"F0.wireOp",EDGE,"E12.22.0.1"),sQuery(id+"F0.wireOp",EDGE,"E12.22.0.2"),sQuery(id+"F0.wireOp",EDGE,"E12.22.0.4"),sQuery(id+"F0.wireOp",EDGE,"E12.22.0.5"),sQuery(id+"F0.wireOp",EDGE,"E12.22.0.6"),sQuery(id+"F0.wireOp",EDGE,"E12.22.0.7"),sQuery(id+"F0.wireOp",EDGE,"E12.22.0.8"),sQuery(id+"F0.wireOp",EDGE,"E12.22.0.9"),sQuery(id+"F0.wireOp",EDGE,"E12.22.0.10"),sQuery(id+"F0.wireOp",EDGE,"E12.23.0.0"),sQuery(id+"F0.wireOp",EDGE,"E12.23.0.1"),sQuery(id+"F0.wireOp",EDGE,"E12.23.0.2"),sQuery(id+"F0.wireOp",EDGE,"E12.23.0.4"),sQuery(id+"F0.wireOp",EDGE,"E12.23.0.5"),sQuery(id+"F0.wireOp",EDGE,"E12.23.0.6"),sQuery(id+"F0.wireOp",EDGE,"E12.23.0.7"),sQuery(id+"F0.wireOp",EDGE,"E12.23.0.8"),sQuery(id+"F0.wireOp",EDGE,"E12.23.0.9"),sQuery(id+"F0.wireOp",EDGE,"E12.23.0.10"),sQuery(id+"F0.wireOp",EDGE,"E12.24.0.0"),sQuery(id+"F0.wireOp",EDGE,"E12.24.0.1"),sQuery(id+"F0.wireOp",EDGE,"E12.24.0.2"),sQuery(id+"F0.wireOp",EDGE,"E12.24.0.4"),sQuery(id+"F0.wireOp",EDGE,"E12.24.0.5"),sQuery(id+"F0.wireOp",EDGE,"E12.24.0.6"),sQuery(id+"F0.wireOp",EDGE,"E12.24.0.7"),sQuery(id+"F0.wireOp",EDGE,"E12.24.0.8"),sQuery(id+"F0.wireOp",EDGE,"E12.24.0.9"),sQuery(id+"F0.wireOp",EDGE,"E12.24.0.10"),sQuery(id+"F0.wireOp",EDGE,"E12.25.0.0"),sQuery(id+"F0.wireOp",EDGE,"E12.25.0.1"),sQuery(id+"F0.wireOp",EDGE,"E12.25.0.2"),sQuery(id+"F0.wireOp",EDGE,"E12.25.0.4"),sQuery(id+"F0.wireOp",EDGE,"E12.25.0.5"),sQuery(id+"F0.wireOp",EDGE,"E12.25.0.6"),sQuery(id+"F0.wireOp",EDGE,"E12.25.0.7"),sQuery(id+"F0.wireOp",EDGE,"E12.25.0.8"),sQuery(id+"F0.wireOp",EDGE,"E12.25.0.9"),sQuery(id+"F0.wireOp",EDGE,"E12.25.0.10"),sQuery(id+"F0.wireOp",EDGE,"E12.26.0.0"),sQuery(id+"F0.wireOp",EDGE,"E12.26.0.1"),sQuery(id+"F0.wireOp",EDGE,"E12.26.0.2"),sQuery(id+"F0.wireOp",EDGE,"E12.26.0.4"),sQuery(id+"F0.wireOp",EDGE,"E12.26.0.5"),sQuery(id+"F0.wireOp",EDGE,"E12.26.0.6"),sQuery(id+"F0.wireOp",EDGE,"E12.26.0.7"),sQuery(id+"F0.wireOp",EDGE,"E12.26.0.8"),sQuery(id+"F0.wireOp",EDGE,"E12.26.0.9"),sQuery(id+"F0.wireOp",EDGE,"E12.26.0.10"),sQuery(id+"F0.wireOp",EDGE,"E12.27.0.0"),sQuery(id+"F0.wireOp",EDGE,"E12.27.0.1"),sQuery(id+"F0.wireOp",EDGE,"E12.27.0.2"),sQuery(id+"F0.wireOp",EDGE,"E12.27.0.4"),sQuery(id+"F0.wireOp",EDGE,"E12.27.0.5"),sQuery(id+"F0.wireOp",EDGE,"E12.27.0.6"),sQuery(id+"F0.wireOp",EDGE,"E12.27.0.7"),sQuery(id+"F0.wireOp",EDGE,"E12.27.0.8"),sQuery(id+"F0.wireOp",EDGE,"E12.27.0.9"),sQuery(id+"F0.wireOp",EDGE,"E12.27.0.10"),sQuery(id+"F0.wireOp",EDGE,"E12.28.0.0"),sQuery(id+"F0.wireOp",EDGE,"E12.28.0.1"),sQuery(id+"F0.wireOp",EDGE,"E12.28.0.2"),sQuery(id+"F0.wireOp",EDGE,"E12.28.0.4"),sQuery(id+"F0.wireOp",EDGE,"E12.28.0.5"),sQuery(id+"F0.wireOp",EDGE,"E12.28.0.6"),sQuery(id+"F0.wireOp",EDGE,"E12.28.0.7"),sQuery(id+"F0.wireOp",EDGE,"E12.28.0.8"),sQuery(id+"F0.wireOp",EDGE,"E12.28.0.9"),sQuery(id+"F0.wireOp",EDGE,"E12.28.0.10"),sQuery(id+"F0.wireOp",EDGE,"E12.29.0.0"),sQuery(id+"F0.wireOp",EDGE,"E12.29.0.1"),sQuery(id+"F0.wireOp",EDGE,"E12.29.0.2"),sQuery(id+"F0.wireOp",EDGE,"E12.29.0.4"),sQuery(id+"F0.wireOp",EDGE,"E12.29.0.5"),sQuery(id+"F0.wireOp",EDGE,"E12.29.0.6"),sQuery(id+"F0.wireOp",EDGE,"E12.29.0.7"),sQuery(id+"F0.wireOp",EDGE,"E12.29.0.8"),sQuery(id+"F0.wireOp",EDGE,"E12.29.0.9"),sQuery(id+"F0.wireOp",EDGE,"E12.29.0.10"),sQuery(id+"F0.wireOp",EDGE,"E12.30.0.0"),sQuery(id+"F0.wireOp",EDGE,"E12.30.0.1"),sQuery(id+"F0.wireOp",EDGE,"E12.30.0.2"),sQuery(id+"F0.wireOp",EDGE,"E12.30.0.4"),sQuery(id+"F0.wireOp",EDGE,"E12.30.0.5"),sQuery(id+"F0.wireOp",EDGE,"E12.30.0.6"),sQuery(id+"F0.wireOp",EDGE,"E12.30.0.7"),sQuery(id+"F0.wireOp",EDGE,"E12.30.0.8"),sQuery(id+"F0.wireOp",EDGE,"E12.30.0.9"),sQuery(id+"F0.wireOp",EDGE,"E12.30.0.10"),sQuery(id+"F0.wireOp",EDGE,"E12.31.0.0"),sQuery(id+"F0.wireOp",EDGE,"E12.31.0.1"),sQuery(id+"F0.wireOp",EDGE,"E12.31.0.2"),sQuery(id+"F0.wireOp",EDGE,"E12.31.0.4"),sQuery(id+"F0.wireOp",EDGE,"E12.31.0.5"),sQuery(id+"F0.wireOp",EDGE,"E12.31.0.6"),sQuery(id+"F0.wireOp",EDGE,"E12.31.0.7"),sQuery(id+"F0.wireOp",EDGE,"E12.31.0.8"),sQuery(id+"F0.wireOp",EDGE,"E12.31.0.9"),sQuery(id+"F0.wireOp",EDGE,"E12.31.0.10"),sQuery(id+"F0.wireOp",EDGE,"E12.32.0.0"),sQuery(id+"F0.wireOp",EDGE,"E12.32.0.1"),sQuery(id+"F0.wireOp",EDGE,"E12.32.0.2"),sQuery(id+"F0.wireOp",EDGE,"E12.32.0.4"),sQuery(id+"F0.wireOp",EDGE,"E12.32.0.5"),sQuery(id+"F0.wireOp",EDGE,"E12.32.0.6"),sQuery(id+"F0.wireOp",EDGE,"E12.32.0.7"),sQuery(id+"F0.wireOp",EDGE,"E12.32.0.8"),sQuery(id+"F0.wireOp",EDGE,"E12.32.0.9"),sQuery(id+"F0.wireOp",EDGE,"E12.32.0.10"),sQuery(id+"F0.wireOp",EDGE,"E12.33.0.0"),sQuery(id+"F0.wireOp",EDGE,"E12.33.0.1"),sQuery(id+"F0.wireOp",EDGE,"E12.33.0.2"),sQuery(id+"F0.wireOp",EDGE,"E12.33.0.4"),sQuery(id+"F0.wireOp",EDGE,"E12.33.0.5"),sQuery(id+"F0.wireOp",EDGE,"E12.33.0.6"),sQuery(id+"F0.wireOp",EDGE,"E12.33.0.7"),sQuery(id+"F0.wireOp",EDGE,"E12.33.0.8"),sQuery(id+"F0.wireOp",EDGE,"E12.33.0.9"),sQuery(id+"F0.wireOp",EDGE,"E12.33.0.10"),sQuery(id+"F0.wireOp",EDGE,"E12.34.0.0"),sQuery(id+"F0.wireOp",EDGE,"E12.34.0.1"),sQuery(id+"F0.wireOp",EDGE,"E12.34.0.2"),sQuery(id+"F0.wireOp",EDGE,"E12.34.0.4"),sQuery(id+"F0.wireOp",EDGE,"E12.34.0.5"),sQuery(id+"F0.wireOp",EDGE,"E12.34.0.6"),sQuery(id+"F0.wireOp",EDGE,"E12.34.0.7"),sQuery(id+"F0.wireOp",EDGE,"E12.34.0.8"),sQuery(id+"F0.wireOp",EDGE,"E12.34.0.9"),sQuery(id+"F0.wireOp",EDGE,"E12.34.0.10"),sQuery(id+"F0.wireOp",EDGE,"E12.35.0.0"),sQuery(id+"F0.wireOp",EDGE,"E12.35.0.1"),sQuery(id+"F0.wireOp",EDGE,"E12.35.0.2"),sQuery(id+"F0.wireOp",EDGE,"E12.35.0.4"),sQuery(id+"F0.wireOp",EDGE,"E12.35.0.5"),sQuery(id+"F0.wireOp",EDGE,"E12.35.0.6"),sQuery(id+"F0.wireOp",EDGE,"E12.35.0.7"),sQuery(id+"F0.wireOp",EDGE,"E12.35.0.8"),sQuery(id+"F0.wireOp",EDGE,"E12.35.0.9"),sQuery(id+"F0.wireOp",EDGE,"E12.35.0.10"),sQuery(id+"F0.wireOp",EDGE,"E12.36.0.0"),sQuery(id+"F0.wireOp",EDGE,"E12.36.0.1"),sQuery(id+"F0.wireOp",EDGE,"E12.36.0.2"),sQuery(id+"F0.wireOp",EDGE,"E12.36.0.4"),sQuery(id+"F0.wireOp",EDGE,"E12.36.0.5"),sQuery(id+"F0.wireOp",EDGE,"E12.36.0.6"),sQuery(id+"F0.wireOp",EDGE,"E12.36.0.7"),sQuery(id+"F0.wireOp",EDGE,"E12.36.0.8"),sQuery(id+"F0.wireOp",EDGE,"E12.36.0.9"),sQuery(id+"F0.wireOp",EDGE,"E12.36.0.10"),sQuery(id+"F0.wireOp",EDGE,"E12.37.0.0"),sQuery(id+"F0.wireOp",EDGE,"E12.37.0.1"),sQuery(id+"F0.wireOp",EDGE,"E12.37.0.2"),sQuery(id+"F0.wireOp",EDGE,"E12.37.0.4"),sQuery(id+"F0.wireOp",EDGE,"E12.37.0.5"),sQuery(id+"F0.wireOp",EDGE,"E12.37.0.6"),sQuery(id+"F0.wireOp",EDGE,"E12.37.0.7"),sQuery(id+"F0.wireOp",EDGE,"E12.37.0.8"),sQuery(id+"F0.wireOp",EDGE,"E12.37.0.9"),sQuery(id+"F0.wireOp",EDGE,"E12.37.0.10"),sQuery(id+"F0.wireOp",EDGE,"E12.38.0.0"),sQuery(id+"F0.wireOp",EDGE,"E12.38.0.1"),sQuery(id+"F0.wireOp",EDGE,"E12.38.0.2"),sQuery(id+"F0.wireOp",EDGE,"E12.38.0.4"),sQuery(id+"F0.wireOp",EDGE,"E12.38.0.5"),sQuery(id+"F0.wireOp",EDGE,"E12.38.0.6"),sQuery(id+"F0.wireOp",EDGE,"E12.38.0.7"),sQuery(id+"F0.wireOp",EDGE,"E12.38.0.8"),sQuery(id+"F0.wireOp",EDGE,"E12.38.0.9"),sQuery(id+"F0.wireOp",EDGE,"E12.38.0.10"),sQuery(id+"F0.wireOp",EDGE,"E12.39.0.0"),sQuery(id+"F0.wireOp",EDGE,"E12.39.0.1"),sQuery(id+"F0.wireOp",EDGE,"E12.39.0.2"),sQuery(id+"F0.wireOp",EDGE,"E12.39.0.4"),sQuery(id+"F0.wireOp",EDGE,"E12.39.0.5"),sQuery(id+"F0.wireOp",EDGE,"E12.39.0.6"),sQuery(id+"F0.wireOp",EDGE,"E12.39.0.7"),sQuery(id+"F0.wireOp",EDGE,"E12.39.0.8"),sQuery(id+"F0.wireOp",EDGE,"E12.39.0.9"),sQuery(id+"F0.wireOp",EDGE,"E12.39.0.10"),sQuery(id+"F0.wireOp",EDGE,"E12.40.0.0"),sQuery(id+"F0.wireOp",EDGE,"E12.40.0.1"),sQuery(id+"F0.wireOp",EDGE,"E12.40.0.2"),sQuery(id+"F0.wireOp",EDGE,"E12.40.0.4"),sQuery(id+"F0.wireOp",EDGE,"E12.40.0.5"),sQuery(id+"F0.wireOp",EDGE,"E12.40.0.6"),sQuery(id+"F0.wireOp",EDGE,"E12.40.0.7"),sQuery(id+"F0.wireOp",EDGE,"E12.40.0.8"),sQuery(id+"F0.wireOp",EDGE,"E12.40.0.9"),sQuery(id+"F0.wireOp",EDGE,"E12.40.0.10"),sQuery(id+"F0.wireOp",EDGE,"E12.41.0.0"),sQuery(id+"F0.wireOp",EDGE,"E12.41.0.1"),sQuery(id+"F0.wireOp",EDGE,"E12.41.0.2"),sQuery(id+"F0.wireOp",EDGE,"E12.41.0.4"),sQuery(id+"F0.wireOp",EDGE,"E12.41.0.5"),sQuery(id+"F0.wireOp",EDGE,"E12.41.0.6"),sQuery(id+"F0.wireOp",EDGE,"E12.41.0.7"),sQuery(id+"F0.wireOp",EDGE,"E12.41.0.8"),sQuery(id+"F0.wireOp",EDGE,"E12.41.0.9"),sQuery(id+"F0.wireOp",EDGE,"E12.41.0.10"),sQuery(id+"F0.wireOp",EDGE,"E12.42.0.0"),sQuery(id+"F0.wireOp",EDGE,"E12.42.0.1"),sQuery(id+"F0.wireOp",EDGE,"E12.42.0.2"),sQuery(id+"F0.wireOp",EDGE,"E12.42.0.4"),sQuery(id+"F0.wireOp",EDGE,"E12.42.0.5"),sQuery(id+"F0.wireOp",EDGE,"E12.42.0.6"),sQuery(id+"F0.wireOp",EDGE,"E12.42.0.7"),sQuery(id+"F0.wireOp",EDGE,"E12.42.0.8"),sQuery(id+"F0.wireOp",EDGE,"E12.42.0.9"),sQuery(id+"F0.wireOp",EDGE,"E12.42.0.10"),sQuery(id+"F0.wireOp",EDGE,"E12.43.0.0"),sQuery(id+"F0.wireOp",EDGE,"E12.43.0.1"),sQuery(id+"F0.wireOp",EDGE,"E12.43.0.2"),sQuery(id+"F0.wireOp",EDGE,"E12.43.0.4"),sQuery(id+"F0.wireOp",EDGE,"E12.43.0.5"),sQuery(id+"F0.wireOp",EDGE,"E12.43.0.6"),sQuery(id+"F0.wireOp",EDGE,"E12.43.0.7"),sQuery(id+"F0.wireOp",EDGE,"E12.43.0.8"),sQuery(id+"F0.wireOp",EDGE,"E12.43.0.9"),sQuery(id+"F0.wireOp",EDGE,"E12.43.0.10"),sQuery(id+"F0.wireOp",EDGE,"E12.44.0.0"),sQuery(id+"F0.wireOp",EDGE,"E12.44.0.1"),sQuery(id+"F0.wireOp",EDGE,"E12.44.0.2"),sQuery(id+"F0.wireOp",EDGE,"E12.44.0.4"),sQuery(id+"F0.wireOp",EDGE,"E12.44.0.5"),sQuery(id+"F0.wireOp",EDGE,"E12.44.0.6"),sQuery(id+"F0.wireOp",EDGE,"E12.44.0.7"),sQuery(id+"F0.wireOp",EDGE,"E12.44.0.8"),sQuery(id+"F0.wireOp",EDGE,"E12.44.0.9"),sQuery(id+"F0.wireOp",EDGE,"E12.44.0.10"),sQuery(id+"F0.wireOp",EDGE,"E12.45.0.0"),sQuery(id+"F0.wireOp",EDGE,"E12.45.0.1"),sQuery(id+"F0.wireOp",EDGE,"E12.45.0.2"),sQuery(id+"F0.wireOp",EDGE,"E12.45.0.4"),sQuery(id+"F0.wireOp",EDGE,"E12.45.0.5"),sQuery(id+"F0.wireOp",EDGE,"E12.45.0.6"),sQuery(id+"F0.wireOp",EDGE,"E12.45.0.7"),sQuery(id+"F0.wireOp",EDGE,"E12.45.0.8"),sQuery(id+"F0.wireOp",EDGE,"E12.45.0.9"),sQuery(id+"F0.wireOp",EDGE,"E12.45.0.10"),sQuery(id+"F0.wireOp",EDGE,"E12.46.0.0"),sQuery(id+"F0.wireOp",EDGE,"E12.46.0.1"),sQuery(id+"F0.wireOp",EDGE,"E12.46.0.2"),sQuery(id+"F0.wireOp",EDGE,"E12.46.0.4"),sQuery(id+"F0.wireOp",EDGE,"E12.46.0.5"),sQuery(id+"F0.wireOp",EDGE,"E12.46.0.6"),sQuery(id+"F0.wireOp",EDGE,"E12.46.0.7"),sQuery(id+"F0.wireOp",EDGE,"E12.46.0.8"),sQuery(id+"F0.wireOp",EDGE,"E12.46.0.9"),sQuery(id+"F0.wireOp",EDGE,"E12.46.0.10"),sQuery(id+"F0.wireOp",EDGE,"E12.47.0.0"),sQuery(id+"F0.wireOp",EDGE,"E12.47.0.1"),sQuery(id+"F0.wireOp",EDGE,"E12.47.0.2"),sQuery(id+"F0.wireOp",EDGE,"E12.47.0.4"),sQuery(id+"F0.wireOp",EDGE,"E12.47.0.5"),sQuery(id+"F0.wireOp",EDGE,"E12.47.0.6"),sQuery(id+"F0.wireOp",EDGE,"E12.47.0.7"),sQuery(id+"F0.wireOp",EDGE,"E12.47.0.8"),sQuery(id+"F0.wireOp",EDGE,"E12.47.0.9"),sQuery(id+"F0.wireOp",EDGE,"E12.47.0.10"),sQuery(id+"F0.wireOp",EDGE,"E12.48.0.0"),sQuery(id+"F0.wireOp",EDGE,"E12.48.0.1"),sQuery(id+"F0.wireOp",EDGE,"E12.48.0.2"),sQuery(id+"F0.wireOp",EDGE,"E12.48.0.4"),sQuery(id+"F0.wireOp",EDGE,"E12.48.0.5"),sQuery(id+"F0.wireOp",EDGE,"E12.48.0.6"),sQuery(id+"F0.wireOp",EDGE,"E12.48.0.7"),sQuery(id+"F0.wireOp",EDGE,"E12.48.0.8"),sQuery(id+"F0.wireOp",EDGE,"E12.48.0.9"),sQuery(id+"F0.wireOp",EDGE,"E12.48.0.10"),sQuery(id+"F0.wireOp",EDGE,"E12.49.0.0"),sQuery(id+"F0.wireOp",EDGE,"E12.49.0.1"),sQuery(id+"F0.wireOp",EDGE,"E12.49.0.2"),sQuery(id+"F0.wireOp",EDGE,"E12.49.0.4"),sQuery(id+"F0.wireOp",EDGE,"E12.49.0.5"),sQuery(id+"F0.wireOp",EDGE,"E12.49.0.6"),sQuery(id+"F0.wireOp",EDGE,"E12.49.0.7"),sQuery(id+"F0.wireOp",EDGE,"E12.49.0.8"),sQuery(id+"F0.wireOp",EDGE,"E12.49.0.9"),sQuery(id+"F0.wireOp",EDGE,"E12.49.0.10")])],"isStart":false});
            var sketch = newSketch(context, id + "F2", { "sketchPlane" : qUnion([Q0])});
            skPoint(sketch, "E13.oppositeSnap0", {"position": v(0, 6.35) * mm});
            skLineSegment(sketch, "E14.bottom", {"start": v(0, 0) * mm, "end": v(38.1, 0) * mm});
            skLineSegment(sketch, "E14.top", {"start": v(0, 8.25) * mm, "end": v(38.1, 8.25) * mm});
            skLineSegment(sketch, "E14.left", {"start": v(0, 0) * mm, "end": v(0, 8.25) * mm});
            skLineSegment(sketch, "E14.right", {"start": v(38.1, 0) * mm, "end": v(38.1, 8.25) * mm});
            skSolve(sketch);
        }
        {
            var Q0;
            Q0 = qSketchRegion(id + "F2", true);
            extrude(context, id + "F3", {"entities" : qUnion([Q0]), "operationType" : NewBodyOperationType.ADD, "depth" : 50.8 * mm});
        }
        {
            var Q0;
            Q0=makeQuery(id+"F3.opExtrude","SWEPT_FACE",FACE,{"disambiguationData":[OSD([sQuery(id+"F2.wireOp",EDGE,"E14.top")])]});
            var sketch = newSketch(context, id + "F4", { "sketchPlane" : qUnion([Q0])});
            skCircle(sketch, "E15", {"center": v(10.16, -167.64) * mm, "radius": 2.54 * mm});
            skCircle(sketch, "E16", {"center": v(30.48, -167.64) * mm, "radius": 2.54 * mm});
            skSolve(sketch);
        }
        {
            var Q0;
            Q0 = qSketchRegion(id + "F4", true);
            extrude(context, id + "F5", {"entities" : qUnion([Q0]), "operationType" : NewBodyOperationType.REMOVE, "endBound" : BoundingType.THROUGH_ALL, "oppositeDirection" : true, "depth" : 25.4 * mm});
        }
        {
            var Q0;
            Q0=makeQuery(id+"F3.opExtrude","SWEPT_FACE",FACE,{"disambiguationData":[OSD([sQuery(id+"F2.wireOp",EDGE,"E14.top")])]});
            var sketch = newSketch(context, id + "F6", { "sketchPlane" : qUnion([Q0])});
            skCircle(sketch, "E17", {"center": v(10.16, -167.64) * mm, "radius": 3.81 * mm});
            skCircle(sketch, "E18", {"center": v(30.48, -167.64) * mm, "radius": 3.81 * mm});
            skSolve(sketch);
        }
        {
            var Q0;
            Q0 = qSketchRegion(id + "F6", true);
            extrude(context, id + "F7", {"entities" : qUnion([Q0]), "operationType" : NewBodyOperationType.REMOVE, "oppositeDirection" : true, "depth" : 2.54 * mm});
        }
        {
            var Q0;
            Q0=makeQuery(id+"F3.opExtrude","CAP_EDGE",EDGE,{"disambiguationData":[OSD([sQuery(id+"F2.wireOp",EDGE,"E14.left")])],"isStart":false});
            var Q1;
            Q1=makeQuery(id+"F3.opExtrude","CAP_EDGE",EDGE,{"disambiguationData":[OSD([sQuery(id+"F2.wireOp",EDGE,"E14.right")])],"isStart":false});
            fillet(context, id + "F8", {"entities" : qUnion([Q0, Q1]), "radius" : 5.08 * mm, "tangentPropagation" : true, "allowEdgeOverflow" : false});
        }
        {
            var Q0;
            Q0=makeQuery(id+"F1.opExtrude","CAP_FACE",FACE,{"disambiguationData":[OSD([sQuery(id+"F0.wireOp",EDGE,"E0.bottom"),sQuery(id+"F0.wireOp",EDGE,"E0.top"),sQuery(id+"F0.wireOp",EDGE,"E0.left"),sQuery(id+"F0.wireOp",EDGE,"E0.right"),sQuery(id+"F0.wireOp",EDGE,"E1"),sQuery(id+"F0.wireOp",EDGE,"E2"),sQuery(id+"F0.wireOp",EDGE,"E4"),sQuery(id+"F0.wireOp",EDGE,"E5.MirrorCS"),sQuery(id+"F0.wireOp",EDGE,"E6.MirrorCS"),sQuery(id+"F0.wireOp",EDGE,"E7.MirrorCS"),sQuery(id+"F0.wireOp",EDGE,"E8.filletArc"),sQuery(id+"F0.wireOp",EDGE,"E9.filletArc"),sQuery(id+"F0.wireOp",EDGE,"E10.filletArc"),sQuery(id+"F0.wireOp",EDGE,"E11.filletArc"),sQuery(id+"F0.wireOp",EDGE,"E12.1.0.0"),sQuery(id+"F0.wireOp",EDGE,"E12.1.0.1"),sQuery(id+"F0.wireOp",EDGE,"E12.1.0.2"),sQuery(id+"F0.wireOp",EDGE,"E12.1.0.4"),sQuery(id+"F0.wireOp",EDGE,"E12.1.0.5"),sQuery(id+"F0.wireOp",EDGE,"E12.1.0.6"),sQuery(id+"F0.wireOp",EDGE,"E12.1.0.7"),sQuery(id+"F0.wireOp",EDGE,"E12.1.0.8"),sQuery(id+"F0.wireOp",EDGE,"E12.1.0.9"),sQuery(id+"F0.wireOp",EDGE,"E12.1.0.10"),sQuery(id+"F0.wireOp",EDGE,"E12.2.0.0"),sQuery(id+"F0.wireOp",EDGE,"E12.2.0.1"),sQuery(id+"F0.wireOp",EDGE,"E12.2.0.2"),sQuery(id+"F0.wireOp",EDGE,"E12.2.0.4"),sQuery(id+"F0.wireOp",EDGE,"E12.2.0.5"),sQuery(id+"F0.wireOp",EDGE,"E12.2.0.6"),sQuery(id+"F0.wireOp",EDGE,"E12.2.0.7"),sQuery(id+"F0.wireOp",EDGE,"E12.2.0.8"),sQuery(id+"F0.wireOp",EDGE,"E12.2.0.9"),sQuery(id+"F0.wireOp",EDGE,"E12.2.0.10"),sQuery(id+"F0.wireOp",EDGE,"E12.3.0.0"),sQuery(id+"F0.wireOp",EDGE,"E12.3.0.1"),sQuery(id+"F0.wireOp",EDGE,"E12.3.0.2"),sQuery(id+"F0.wireOp",EDGE,"E12.3.0.4"),sQuery(id+"F0.wireOp",EDGE,"E12.3.0.5"),sQuery(id+"F0.wireOp",EDGE,"E12.3.0.6"),sQuery(id+"F0.wireOp",EDGE,"E12.3.0.7"),sQuery(id+"F0.wireOp",EDGE,"E12.3.0.8"),sQuery(id+"F0.wireOp",EDGE,"E12.3.0.9"),sQuery(id+"F0.wireOp",EDGE,"E12.3.0.10"),sQuery(id+"F0.wireOp",EDGE,"E12.4.0.0"),sQuery(id+"F0.wireOp",EDGE,"E12.4.0.1"),sQuery(id+"F0.wireOp",EDGE,"E12.4.0.2"),sQuery(id+"F0.wireOp",EDGE,"E12.4.0.4"),sQuery(id+"F0.wireOp",EDGE,"E12.4.0.5"),sQuery(id+"F0.wireOp",EDGE,"E12.4.0.6"),sQuery(id+"F0.wireOp",EDGE,"E12.4.0.7"),sQuery(id+"F0.wireOp",EDGE,"E12.4.0.8"),sQuery(id+"F0.wireOp",EDGE,"E12.4.0.9"),sQuery(id+"F0.wireOp",EDGE,"E12.4.0.10"),sQuery(id+"F0.wireOp",EDGE,"E12.5.0.0"),sQuery(id+"F0.wireOp",EDGE,"E12.5.0.1"),sQuery(id+"F0.wireOp",EDGE,"E12.5.0.2"),sQuery(id+"F0.wireOp",EDGE,"E12.5.0.4"),sQuery(id+"F0.wireOp",EDGE,"E12.5.0.5"),sQuery(id+"F0.wireOp",EDGE,"E12.5.0.6"),sQuery(id+"F0.wireOp",EDGE,"E12.5.0.7"),sQuery(id+"F0.wireOp",EDGE,"E12.5.0.8"),sQuery(id+"F0.wireOp",EDGE,"E12.5.0.9"),sQuery(id+"F0.wireOp",EDGE,"E12.5.0.10"),sQuery(id+"F0.wireOp",EDGE,"E12.6.0.0"),sQuery(id+"F0.wireOp",EDGE,"E12.6.0.1"),sQuery(id+"F0.wireOp",EDGE,"E12.6.0.2"),sQuery(id+"F0.wireOp",EDGE,"E12.6.0.4"),sQuery(id+"F0.wireOp",EDGE,"E12.6.0.5"),sQuery(id+"F0.wireOp",EDGE,"E12.6.0.6"),sQuery(id+"F0.wireOp",EDGE,"E12.6.0.7"),sQuery(id+"F0.wireOp",EDGE,"E12.6.0.8"),sQuery(id+"F0.wireOp",EDGE,"E12.6.0.9"),sQuery(id+"F0.wireOp",EDGE,"E12.6.0.10"),sQuery(id+"F0.wireOp",EDGE,"E12.7.0.0"),sQuery(id+"F0.wireOp",EDGE,"E12.7.0.1"),sQuery(id+"F0.wireOp",EDGE,"E12.7.0.2"),sQuery(id+"F0.wireOp",EDGE,"E12.7.0.4"),sQuery(id+"F0.wireOp",EDGE,"E12.7.0.5"),sQuery(id+"F0.wireOp",EDGE,"E12.7.0.6"),sQuery(id+"F0.wireOp",EDGE,"E12.7.0.7"),sQuery(id+"F0.wireOp",EDGE,"E12.7.0.8"),sQuery(id+"F0.wireOp",EDGE,"E12.7.0.9"),sQuery(id+"F0.wireOp",EDGE,"E12.7.0.10"),sQuery(id+"F0.wireOp",EDGE,"E12.8.0.0"),sQuery(id+"F0.wireOp",EDGE,"E12.8.0.1"),sQuery(id+"F0.wireOp",EDGE,"E12.8.0.2"),sQuery(id+"F0.wireOp",EDGE,"E12.8.0.4"),sQuery(id+"F0.wireOp",EDGE,"E12.8.0.5"),sQuery(id+"F0.wireOp",EDGE,"E12.8.0.6"),sQuery(id+"F0.wireOp",EDGE,"E12.8.0.7"),sQuery(id+"F0.wireOp",EDGE,"E12.8.0.8"),sQuery(id+"F0.wireOp",EDGE,"E12.8.0.9"),sQuery(id+"F0.wireOp",EDGE,"E12.8.0.10"),sQuery(id+"F0.wireOp",EDGE,"E12.9.0.0"),sQuery(id+"F0.wireOp",EDGE,"E12.9.0.1"),sQuery(id+"F0.wireOp",EDGE,"E12.9.0.2"),sQuery(id+"F0.wireOp",EDGE,"E12.9.0.4"),sQuery(id+"F0.wireOp",EDGE,"E12.9.0.5"),sQuery(id+"F0.wireOp",EDGE,"E12.9.0.6"),sQuery(id+"F0.wireOp",EDGE,"E12.9.0.7"),sQuery(id+"F0.wireOp",EDGE,"E12.9.0.8"),sQuery(id+"F0.wireOp",EDGE,"E12.9.0.9"),sQuery(id+"F0.wireOp",EDGE,"E12.9.0.10"),sQuery(id+"F0.wireOp",EDGE,"E12.10.0.0"),sQuery(id+"F0.wireOp",EDGE,"E12.10.0.1"),sQuery(id+"F0.wireOp",EDGE,"E12.10.0.2"),sQuery(id+"F0.wireOp",EDGE,"E12.10.0.4"),sQuery(id+"F0.wireOp",EDGE,"E12.10.0.5"),sQuery(id+"F0.wireOp",EDGE,"E12.10.0.6"),sQuery(id+"F0.wireOp",EDGE,"E12.10.0.7"),sQuery(id+"F0.wireOp",EDGE,"E12.10.0.8"),sQuery(id+"F0.wireOp",EDGE,"E12.10.0.9"),sQuery(id+"F0.wireOp",EDGE,"E12.10.0.10"),sQuery(id+"F0.wireOp",EDGE,"E12.11.0.0"),sQuery(id+"F0.wireOp",EDGE,"E12.11.0.1"),sQuery(id+"F0.wireOp",EDGE,"E12.11.0.2"),sQuery(id+"F0.wireOp",EDGE,"E12.11.0.4"),sQuery(id+"F0.wireOp",EDGE,"E12.11.0.5"),sQuery(id+"F0.wireOp",EDGE,"E12.11.0.6"),sQuery(id+"F0.wireOp",EDGE,"E12.11.0.7"),sQuery(id+"F0.wireOp",EDGE,"E12.11.0.8"),sQuery(id+"F0.wireOp",EDGE,"E12.11.0.9"),sQuery(id+"F0.wireOp",EDGE,"E12.11.0.10"),sQuery(id+"F0.wireOp",EDGE,"E12.12.0.0"),sQuery(id+"F0.wireOp",EDGE,"E12.12.0.1"),sQuery(id+"F0.wireOp",EDGE,"E12.12.0.2"),sQuery(id+"F0.wireOp",EDGE,"E12.12.0.4"),sQuery(id+"F0.wireOp",EDGE,"E12.12.0.5"),sQuery(id+"F0.wireOp",EDGE,"E12.12.0.6"),sQuery(id+"F0.wireOp",EDGE,"E12.12.0.7"),sQuery(id+"F0.wireOp",EDGE,"E12.12.0.8"),sQuery(id+"F0.wireOp",EDGE,"E12.12.0.9"),sQuery(id+"F0.wireOp",EDGE,"E12.12.0.10"),sQuery(id+"F0.wireOp",EDGE,"E12.13.0.0"),sQuery(id+"F0.wireOp",EDGE,"E12.13.0.1"),sQuery(id+"F0.wireOp",EDGE,"E12.13.0.2"),sQuery(id+"F0.wireOp",EDGE,"E12.13.0.4"),sQuery(id+"F0.wireOp",EDGE,"E12.13.0.5"),sQuery(id+"F0.wireOp",EDGE,"E12.13.0.6"),sQuery(id+"F0.wireOp",EDGE,"E12.13.0.7"),sQuery(id+"F0.wireOp",EDGE,"E12.13.0.8"),sQuery(id+"F0.wireOp",EDGE,"E12.13.0.9"),sQuery(id+"F0.wireOp",EDGE,"E12.13.0.10"),sQuery(id+"F0.wireOp",EDGE,"E12.14.0.0"),sQuery(id+"F0.wireOp",EDGE,"E12.14.0.1"),sQuery(id+"F0.wireOp",EDGE,"E12.14.0.2"),sQuery(id+"F0.wireOp",EDGE,"E12.14.0.4"),sQuery(id+"F0.wireOp",EDGE,"E12.14.0.5"),sQuery(id+"F0.wireOp",EDGE,"E12.14.0.6"),sQuery(id+"F0.wireOp",EDGE,"E12.14.0.7"),sQuery(id+"F0.wireOp",EDGE,"E12.14.0.8"),sQuery(id+"F0.wireOp",EDGE,"E12.14.0.9"),sQuery(id+"F0.wireOp",EDGE,"E12.14.0.10"),sQuery(id+"F0.wireOp",EDGE,"E12.15.0.0"),sQuery(id+"F0.wireOp",EDGE,"E12.15.0.1"),sQuery(id+"F0.wireOp",EDGE,"E12.15.0.2"),sQuery(id+"F0.wireOp",EDGE,"E12.15.0.4"),sQuery(id+"F0.wireOp",EDGE,"E12.15.0.5"),sQuery(id+"F0.wireOp",EDGE,"E12.15.0.6"),sQuery(id+"F0.wireOp",EDGE,"E12.15.0.7"),sQuery(id+"F0.wireOp",EDGE,"E12.15.0.8"),sQuery(id+"F0.wireOp",EDGE,"E12.15.0.9"),sQuery(id+"F0.wireOp",EDGE,"E12.15.0.10"),sQuery(id+"F0.wireOp",EDGE,"E12.16.0.0"),sQuery(id+"F0.wireOp",EDGE,"E12.16.0.1"),sQuery(id+"F0.wireOp",EDGE,"E12.16.0.2"),sQuery(id+"F0.wireOp",EDGE,"E12.16.0.4"),sQuery(id+"F0.wireOp",EDGE,"E12.16.0.5"),sQuery(id+"F0.wireOp",EDGE,"E12.16.0.6"),sQuery(id+"F0.wireOp",EDGE,"E12.16.0.7"),sQuery(id+"F0.wireOp",EDGE,"E12.16.0.8"),sQuery(id+"F0.wireOp",EDGE,"E12.16.0.9"),sQuery(id+"F0.wireOp",EDGE,"E12.16.0.10"),sQuery(id+"F0.wireOp",EDGE,"E12.17.0.0"),sQuery(id+"F0.wireOp",EDGE,"E12.17.0.1"),sQuery(id+"F0.wireOp",EDGE,"E12.17.0.2"),sQuery(id+"F0.wireOp",EDGE,"E12.17.0.4"),sQuery(id+"F0.wireOp",EDGE,"E12.17.0.5"),sQuery(id+"F0.wireOp",EDGE,"E12.17.0.6"),sQuery(id+"F0.wireOp",EDGE,"E12.17.0.7"),sQuery(id+"F0.wireOp",EDGE,"E12.17.0.8"),sQuery(id+"F0.wireOp",EDGE,"E12.17.0.9"),sQuery(id+"F0.wireOp",EDGE,"E12.17.0.10"),sQuery(id+"F0.wireOp",EDGE,"E12.18.0.0"),sQuery(id+"F0.wireOp",EDGE,"E12.18.0.1"),sQuery(id+"F0.wireOp",EDGE,"E12.18.0.2"),sQuery(id+"F0.wireOp",EDGE,"E12.18.0.4"),sQuery(id+"F0.wireOp",EDGE,"E12.18.0.5"),sQuery(id+"F0.wireOp",EDGE,"E12.18.0.6"),sQuery(id+"F0.wireOp",EDGE,"E12.18.0.7"),sQuery(id+"F0.wireOp",EDGE,"E12.18.0.8"),sQuery(id+"F0.wireOp",EDGE,"E12.18.0.9"),sQuery(id+"F0.wireOp",EDGE,"E12.18.0.10"),sQuery(id+"F0.wireOp",EDGE,"E12.19.0.0"),sQuery(id+"F0.wireOp",EDGE,"E12.19.0.1"),sQuery(id+"F0.wireOp",EDGE,"E12.19.0.2"),sQuery(id+"F0.wireOp",EDGE,"E12.19.0.4"),sQuery(id+"F0.wireOp",EDGE,"E12.19.0.5"),sQuery(id+"F0.wireOp",EDGE,"E12.19.0.6"),sQuery(id+"F0.wireOp",EDGE,"E12.19.0.7"),sQuery(id+"F0.wireOp",EDGE,"E12.19.0.8"),sQuery(id+"F0.wireOp",EDGE,"E12.19.0.9"),sQuery(id+"F0.wireOp",EDGE,"E12.19.0.10"),sQuery(id+"F0.wireOp",EDGE,"E12.20.0.0"),sQuery(id+"F0.wireOp",EDGE,"E12.20.0.1"),sQuery(id+"F0.wireOp",EDGE,"E12.20.0.2"),sQuery(id+"F0.wireOp",EDGE,"E12.20.0.4"),sQuery(id+"F0.wireOp",EDGE,"E12.20.0.5"),sQuery(id+"F0.wireOp",EDGE,"E12.20.0.6"),sQuery(id+"F0.wireOp",EDGE,"E12.20.0.7"),sQuery(id+"F0.wireOp",EDGE,"E12.20.0.8"),sQuery(id+"F0.wireOp",EDGE,"E12.20.0.9"),sQuery(id+"F0.wireOp",EDGE,"E12.20.0.10"),sQuery(id+"F0.wireOp",EDGE,"E12.21.0.0"),sQuery(id+"F0.wireOp",EDGE,"E12.21.0.1"),sQuery(id+"F0.wireOp",EDGE,"E12.21.0.2"),sQuery(id+"F0.wireOp",EDGE,"E12.21.0.4"),sQuery(id+"F0.wireOp",EDGE,"E12.21.0.5"),sQuery(id+"F0.wireOp",EDGE,"E12.21.0.6"),sQuery(id+"F0.wireOp",EDGE,"E12.21.0.7"),sQuery(id+"F0.wireOp",EDGE,"E12.21.0.8"),sQuery(id+"F0.wireOp",EDGE,"E12.21.0.9"),sQuery(id+"F0.wireOp",EDGE,"E12.21.0.10"),sQuery(id+"F0.wireOp",EDGE,"E12.22.0.0"),sQuery(id+"F0.wireOp",EDGE,"E12.22.0.1"),sQuery(id+"F0.wireOp",EDGE,"E12.22.0.2"),sQuery(id+"F0.wireOp",EDGE,"E12.22.0.4"),sQuery(id+"F0.wireOp",EDGE,"E12.22.0.5"),sQuery(id+"F0.wireOp",EDGE,"E12.22.0.6"),sQuery(id+"F0.wireOp",EDGE,"E12.22.0.7"),sQuery(id+"F0.wireOp",EDGE,"E12.22.0.8"),sQuery(id+"F0.wireOp",EDGE,"E12.22.0.9"),sQuery(id+"F0.wireOp",EDGE,"E12.22.0.10"),sQuery(id+"F0.wireOp",EDGE,"E12.23.0.0"),sQuery(id+"F0.wireOp",EDGE,"E12.23.0.1"),sQuery(id+"F0.wireOp",EDGE,"E12.23.0.2"),sQuery(id+"F0.wireOp",EDGE,"E12.23.0.4"),sQuery(id+"F0.wireOp",EDGE,"E12.23.0.5"),sQuery(id+"F0.wireOp",EDGE,"E12.23.0.6"),sQuery(id+"F0.wireOp",EDGE,"E12.23.0.7"),sQuery(id+"F0.wireOp",EDGE,"E12.23.0.8"),sQuery(id+"F0.wireOp",EDGE,"E12.23.0.9"),sQuery(id+"F0.wireOp",EDGE,"E12.23.0.10"),sQuery(id+"F0.wireOp",EDGE,"E12.24.0.0"),sQuery(id+"F0.wireOp",EDGE,"E12.24.0.1"),sQuery(id+"F0.wireOp",EDGE,"E12.24.0.2"),sQuery(id+"F0.wireOp",EDGE,"E12.24.0.4"),sQuery(id+"F0.wireOp",EDGE,"E12.24.0.5"),sQuery(id+"F0.wireOp",EDGE,"E12.24.0.6"),sQuery(id+"F0.wireOp",EDGE,"E12.24.0.7"),sQuery(id+"F0.wireOp",EDGE,"E12.24.0.8"),sQuery(id+"F0.wireOp",EDGE,"E12.24.0.9"),sQuery(id+"F0.wireOp",EDGE,"E12.24.0.10"),sQuery(id+"F0.wireOp",EDGE,"E12.25.0.0"),sQuery(id+"F0.wireOp",EDGE,"E12.25.0.1"),sQuery(id+"F0.wireOp",EDGE,"E12.25.0.2"),sQuery(id+"F0.wireOp",EDGE,"E12.25.0.4"),sQuery(id+"F0.wireOp",EDGE,"E12.25.0.5"),sQuery(id+"F0.wireOp",EDGE,"E12.25.0.6"),sQuery(id+"F0.wireOp",EDGE,"E12.25.0.7"),sQuery(id+"F0.wireOp",EDGE,"E12.25.0.8"),sQuery(id+"F0.wireOp",EDGE,"E12.25.0.9"),sQuery(id+"F0.wireOp",EDGE,"E12.25.0.10"),sQuery(id+"F0.wireOp",EDGE,"E12.26.0.0"),sQuery(id+"F0.wireOp",EDGE,"E12.26.0.1"),sQuery(id+"F0.wireOp",EDGE,"E12.26.0.2"),sQuery(id+"F0.wireOp",EDGE,"E12.26.0.4"),sQuery(id+"F0.wireOp",EDGE,"E12.26.0.5"),sQuery(id+"F0.wireOp",EDGE,"E12.26.0.6"),sQuery(id+"F0.wireOp",EDGE,"E12.26.0.7"),sQuery(id+"F0.wireOp",EDGE,"E12.26.0.8"),sQuery(id+"F0.wireOp",EDGE,"E12.26.0.9"),sQuery(id+"F0.wireOp",EDGE,"E12.26.0.10"),sQuery(id+"F0.wireOp",EDGE,"E12.27.0.0"),sQuery(id+"F0.wireOp",EDGE,"E12.27.0.1"),sQuery(id+"F0.wireOp",EDGE,"E12.27.0.2"),sQuery(id+"F0.wireOp",EDGE,"E12.27.0.4"),sQuery(id+"F0.wireOp",EDGE,"E12.27.0.5"),sQuery(id+"F0.wireOp",EDGE,"E12.27.0.6"),sQuery(id+"F0.wireOp",EDGE,"E12.27.0.7"),sQuery(id+"F0.wireOp",EDGE,"E12.27.0.8"),sQuery(id+"F0.wireOp",EDGE,"E12.27.0.9"),sQuery(id+"F0.wireOp",EDGE,"E12.27.0.10"),sQuery(id+"F0.wireOp",EDGE,"E12.28.0.0"),sQuery(id+"F0.wireOp",EDGE,"E12.28.0.1"),sQuery(id+"F0.wireOp",EDGE,"E12.28.0.2"),sQuery(id+"F0.wireOp",EDGE,"E12.28.0.4"),sQuery(id+"F0.wireOp",EDGE,"E12.28.0.5"),sQuery(id+"F0.wireOp",EDGE,"E12.28.0.6"),sQuery(id+"F0.wireOp",EDGE,"E12.28.0.7"),sQuery(id+"F0.wireOp",EDGE,"E12.28.0.8"),sQuery(id+"F0.wireOp",EDGE,"E12.28.0.9"),sQuery(id+"F0.wireOp",EDGE,"E12.28.0.10"),sQuery(id+"F0.wireOp",EDGE,"E12.29.0.0"),sQuery(id+"F0.wireOp",EDGE,"E12.29.0.1"),sQuery(id+"F0.wireOp",EDGE,"E12.29.0.2"),sQuery(id+"F0.wireOp",EDGE,"E12.29.0.4"),sQuery(id+"F0.wireOp",EDGE,"E12.29.0.5"),sQuery(id+"F0.wireOp",EDGE,"E12.29.0.6"),sQuery(id+"F0.wireOp",EDGE,"E12.29.0.7"),sQuery(id+"F0.wireOp",EDGE,"E12.29.0.8"),sQuery(id+"F0.wireOp",EDGE,"E12.29.0.9"),sQuery(id+"F0.wireOp",EDGE,"E12.29.0.10"),sQuery(id+"F0.wireOp",EDGE,"E12.30.0.0"),sQuery(id+"F0.wireOp",EDGE,"E12.30.0.1"),sQuery(id+"F0.wireOp",EDGE,"E12.30.0.2"),sQuery(id+"F0.wireOp",EDGE,"E12.30.0.4"),sQuery(id+"F0.wireOp",EDGE,"E12.30.0.5"),sQuery(id+"F0.wireOp",EDGE,"E12.30.0.6"),sQuery(id+"F0.wireOp",EDGE,"E12.30.0.7"),sQuery(id+"F0.wireOp",EDGE,"E12.30.0.8"),sQuery(id+"F0.wireOp",EDGE,"E12.30.0.9"),sQuery(id+"F0.wireOp",EDGE,"E12.30.0.10"),sQuery(id+"F0.wireOp",EDGE,"E12.31.0.0"),sQuery(id+"F0.wireOp",EDGE,"E12.31.0.1"),sQuery(id+"F0.wireOp",EDGE,"E12.31.0.2"),sQuery(id+"F0.wireOp",EDGE,"E12.31.0.4"),sQuery(id+"F0.wireOp",EDGE,"E12.31.0.5"),sQuery(id+"F0.wireOp",EDGE,"E12.31.0.6"),sQuery(id+"F0.wireOp",EDGE,"E12.31.0.7"),sQuery(id+"F0.wireOp",EDGE,"E12.31.0.8"),sQuery(id+"F0.wireOp",EDGE,"E12.31.0.9"),sQuery(id+"F0.wireOp",EDGE,"E12.31.0.10"),sQuery(id+"F0.wireOp",EDGE,"E12.32.0.0"),sQuery(id+"F0.wireOp",EDGE,"E12.32.0.1"),sQuery(id+"F0.wireOp",EDGE,"E12.32.0.2"),sQuery(id+"F0.wireOp",EDGE,"E12.32.0.4"),sQuery(id+"F0.wireOp",EDGE,"E12.32.0.5"),sQuery(id+"F0.wireOp",EDGE,"E12.32.0.6"),sQuery(id+"F0.wireOp",EDGE,"E12.32.0.7"),sQuery(id+"F0.wireOp",EDGE,"E12.32.0.8"),sQuery(id+"F0.wireOp",EDGE,"E12.32.0.9"),sQuery(id+"F0.wireOp",EDGE,"E12.32.0.10"),sQuery(id+"F0.wireOp",EDGE,"E12.33.0.0"),sQuery(id+"F0.wireOp",EDGE,"E12.33.0.1"),sQuery(id+"F0.wireOp",EDGE,"E12.33.0.2"),sQuery(id+"F0.wireOp",EDGE,"E12.33.0.4"),sQuery(id+"F0.wireOp",EDGE,"E12.33.0.5"),sQuery(id+"F0.wireOp",EDGE,"E12.33.0.6"),sQuery(id+"F0.wireOp",EDGE,"E12.33.0.7"),sQuery(id+"F0.wireOp",EDGE,"E12.33.0.8"),sQuery(id+"F0.wireOp",EDGE,"E12.33.0.9"),sQuery(id+"F0.wireOp",EDGE,"E12.33.0.10"),sQuery(id+"F0.wireOp",EDGE,"E12.34.0.0"),sQuery(id+"F0.wireOp",EDGE,"E12.34.0.1"),sQuery(id+"F0.wireOp",EDGE,"E12.34.0.2"),sQuery(id+"F0.wireOp",EDGE,"E12.34.0.4"),sQuery(id+"F0.wireOp",EDGE,"E12.34.0.5"),sQuery(id+"F0.wireOp",EDGE,"E12.34.0.6"),sQuery(id+"F0.wireOp",EDGE,"E12.34.0.7"),sQuery(id+"F0.wireOp",EDGE,"E12.34.0.8"),sQuery(id+"F0.wireOp",EDGE,"E12.34.0.9"),sQuery(id+"F0.wireOp",EDGE,"E12.34.0.10"),sQuery(id+"F0.wireOp",EDGE,"E12.35.0.0"),sQuery(id+"F0.wireOp",EDGE,"E12.35.0.1"),sQuery(id+"F0.wireOp",EDGE,"E12.35.0.2"),sQuery(id+"F0.wireOp",EDGE,"E12.35.0.4"),sQuery(id+"F0.wireOp",EDGE,"E12.35.0.5"),sQuery(id+"F0.wireOp",EDGE,"E12.35.0.6"),sQuery(id+"F0.wireOp",EDGE,"E12.35.0.7"),sQuery(id+"F0.wireOp",EDGE,"E12.35.0.8"),sQuery(id+"F0.wireOp",EDGE,"E12.35.0.9"),sQuery(id+"F0.wireOp",EDGE,"E12.35.0.10"),sQuery(id+"F0.wireOp",EDGE,"E12.36.0.0"),sQuery(id+"F0.wireOp",EDGE,"E12.36.0.1"),sQuery(id+"F0.wireOp",EDGE,"E12.36.0.2"),sQuery(id+"F0.wireOp",EDGE,"E12.36.0.4"),sQuery(id+"F0.wireOp",EDGE,"E12.36.0.5"),sQuery(id+"F0.wireOp",EDGE,"E12.36.0.6"),sQuery(id+"F0.wireOp",EDGE,"E12.36.0.7"),sQuery(id+"F0.wireOp",EDGE,"E12.36.0.8"),sQuery(id+"F0.wireOp",EDGE,"E12.36.0.9"),sQuery(id+"F0.wireOp",EDGE,"E12.36.0.10"),sQuery(id+"F0.wireOp",EDGE,"E12.37.0.0"),sQuery(id+"F0.wireOp",EDGE,"E12.37.0.1"),sQuery(id+"F0.wireOp",EDGE,"E12.37.0.2"),sQuery(id+"F0.wireOp",EDGE,"E12.37.0.4"),sQuery(id+"F0.wireOp",EDGE,"E12.37.0.5"),sQuery(id+"F0.wireOp",EDGE,"E12.37.0.6"),sQuery(id+"F0.wireOp",EDGE,"E12.37.0.7"),sQuery(id+"F0.wireOp",EDGE,"E12.37.0.8"),sQuery(id+"F0.wireOp",EDGE,"E12.37.0.9"),sQuery(id+"F0.wireOp",EDGE,"E12.37.0.10"),sQuery(id+"F0.wireOp",EDGE,"E12.38.0.0"),sQuery(id+"F0.wireOp",EDGE,"E12.38.0.1"),sQuery(id+"F0.wireOp",EDGE,"E12.38.0.2"),sQuery(id+"F0.wireOp",EDGE,"E12.38.0.4"),sQuery(id+"F0.wireOp",EDGE,"E12.38.0.5"),sQuery(id+"F0.wireOp",EDGE,"E12.38.0.6"),sQuery(id+"F0.wireOp",EDGE,"E12.38.0.7"),sQuery(id+"F0.wireOp",EDGE,"E12.38.0.8"),sQuery(id+"F0.wireOp",EDGE,"E12.38.0.9"),sQuery(id+"F0.wireOp",EDGE,"E12.38.0.10"),sQuery(id+"F0.wireOp",EDGE,"E12.39.0.0"),sQuery(id+"F0.wireOp",EDGE,"E12.39.0.1"),sQuery(id+"F0.wireOp",EDGE,"E12.39.0.2"),sQuery(id+"F0.wireOp",EDGE,"E12.39.0.4"),sQuery(id+"F0.wireOp",EDGE,"E12.39.0.5"),sQuery(id+"F0.wireOp",EDGE,"E12.39.0.6"),sQuery(id+"F0.wireOp",EDGE,"E12.39.0.7"),sQuery(id+"F0.wireOp",EDGE,"E12.39.0.8"),sQuery(id+"F0.wireOp",EDGE,"E12.39.0.9"),sQuery(id+"F0.wireOp",EDGE,"E12.39.0.10"),sQuery(id+"F0.wireOp",EDGE,"E12.40.0.0"),sQuery(id+"F0.wireOp",EDGE,"E12.40.0.1"),sQuery(id+"F0.wireOp",EDGE,"E12.40.0.2"),sQuery(id+"F0.wireOp",EDGE,"E12.40.0.4"),sQuery(id+"F0.wireOp",EDGE,"E12.40.0.5"),sQuery(id+"F0.wireOp",EDGE,"E12.40.0.6"),sQuery(id+"F0.wireOp",EDGE,"E12.40.0.7"),sQuery(id+"F0.wireOp",EDGE,"E12.40.0.8"),sQuery(id+"F0.wireOp",EDGE,"E12.40.0.9"),sQuery(id+"F0.wireOp",EDGE,"E12.40.0.10"),sQuery(id+"F0.wireOp",EDGE,"E12.41.0.0"),sQuery(id+"F0.wireOp",EDGE,"E12.41.0.1"),sQuery(id+"F0.wireOp",EDGE,"E12.41.0.2"),sQuery(id+"F0.wireOp",EDGE,"E12.41.0.4"),sQuery(id+"F0.wireOp",EDGE,"E12.41.0.5"),sQuery(id+"F0.wireOp",EDGE,"E12.41.0.6"),sQuery(id+"F0.wireOp",EDGE,"E12.41.0.7"),sQuery(id+"F0.wireOp",EDGE,"E12.41.0.8"),sQuery(id+"F0.wireOp",EDGE,"E12.41.0.9"),sQuery(id+"F0.wireOp",EDGE,"E12.41.0.10"),sQuery(id+"F0.wireOp",EDGE,"E12.42.0.0"),sQuery(id+"F0.wireOp",EDGE,"E12.42.0.1"),sQuery(id+"F0.wireOp",EDGE,"E12.42.0.2"),sQuery(id+"F0.wireOp",EDGE,"E12.42.0.4"),sQuery(id+"F0.wireOp",EDGE,"E12.42.0.5"),sQuery(id+"F0.wireOp",EDGE,"E12.42.0.6"),sQuery(id+"F0.wireOp",EDGE,"E12.42.0.7"),sQuery(id+"F0.wireOp",EDGE,"E12.42.0.8"),sQuery(id+"F0.wireOp",EDGE,"E12.42.0.9"),sQuery(id+"F0.wireOp",EDGE,"E12.42.0.10"),sQuery(id+"F0.wireOp",EDGE,"E12.43.0.0"),sQuery(id+"F0.wireOp",EDGE,"E12.43.0.1"),sQuery(id+"F0.wireOp",EDGE,"E12.43.0.2"),sQuery(id+"F0.wireOp",EDGE,"E12.43.0.4"),sQuery(id+"F0.wireOp",EDGE,"E12.43.0.5"),sQuery(id+"F0.wireOp",EDGE,"E12.43.0.6"),sQuery(id+"F0.wireOp",EDGE,"E12.43.0.7"),sQuery(id+"F0.wireOp",EDGE,"E12.43.0.8"),sQuery(id+"F0.wireOp",EDGE,"E12.43.0.9"),sQuery(id+"F0.wireOp",EDGE,"E12.43.0.10"),sQuery(id+"F0.wireOp",EDGE,"E12.44.0.0"),sQuery(id+"F0.wireOp",EDGE,"E12.44.0.1"),sQuery(id+"F0.wireOp",EDGE,"E12.44.0.2"),sQuery(id+"F0.wireOp",EDGE,"E12.44.0.4"),sQuery(id+"F0.wireOp",EDGE,"E12.44.0.5"),sQuery(id+"F0.wireOp",EDGE,"E12.44.0.6"),sQuery(id+"F0.wireOp",EDGE,"E12.44.0.7"),sQuery(id+"F0.wireOp",EDGE,"E12.44.0.8"),sQuery(id+"F0.wireOp",EDGE,"E12.44.0.9"),sQuery(id+"F0.wireOp",EDGE,"E12.44.0.10"),sQuery(id+"F0.wireOp",EDGE,"E12.45.0.0"),sQuery(id+"F0.wireOp",EDGE,"E12.45.0.1"),sQuery(id+"F0.wireOp",EDGE,"E12.45.0.2"),sQuery(id+"F0.wireOp",EDGE,"E12.45.0.4"),sQuery(id+"F0.wireOp",EDGE,"E12.45.0.5"),sQuery(id+"F0.wireOp",EDGE,"E12.45.0.6"),sQuery(id+"F0.wireOp",EDGE,"E12.45.0.7"),sQuery(id+"F0.wireOp",EDGE,"E12.45.0.8"),sQuery(id+"F0.wireOp",EDGE,"E12.45.0.9"),sQuery(id+"F0.wireOp",EDGE,"E12.45.0.10"),sQuery(id+"F0.wireOp",EDGE,"E12.46.0.0"),sQuery(id+"F0.wireOp",EDGE,"E12.46.0.1"),sQuery(id+"F0.wireOp",EDGE,"E12.46.0.2"),sQuery(id+"F0.wireOp",EDGE,"E12.46.0.4"),sQuery(id+"F0.wireOp",EDGE,"E12.46.0.5"),sQuery(id+"F0.wireOp",EDGE,"E12.46.0.6"),sQuery(id+"F0.wireOp",EDGE,"E12.46.0.7"),sQuery(id+"F0.wireOp",EDGE,"E12.46.0.8"),sQuery(id+"F0.wireOp",EDGE,"E12.46.0.9"),sQuery(id+"F0.wireOp",EDGE,"E12.46.0.10"),sQuery(id+"F0.wireOp",EDGE,"E12.47.0.0"),sQuery(id+"F0.wireOp",EDGE,"E12.47.0.1"),sQuery(id+"F0.wireOp",EDGE,"E12.47.0.2"),sQuery(id+"F0.wireOp",EDGE,"E12.47.0.4"),sQuery(id+"F0.wireOp",EDGE,"E12.47.0.5"),sQuery(id+"F0.wireOp",EDGE,"E12.47.0.6"),sQuery(id+"F0.wireOp",EDGE,"E12.47.0.7"),sQuery(id+"F0.wireOp",EDGE,"E12.47.0.8"),sQuery(id+"F0.wireOp",EDGE,"E12.47.0.9"),sQuery(id+"F0.wireOp",EDGE,"E12.47.0.10"),sQuery(id+"F0.wireOp",EDGE,"E12.48.0.0"),sQuery(id+"F0.wireOp",EDGE,"E12.48.0.1"),sQuery(id+"F0.wireOp",EDGE,"E12.48.0.2"),sQuery(id+"F0.wireOp",EDGE,"E12.48.0.4"),sQuery(id+"F0.wireOp",EDGE,"E12.48.0.5"),sQuery(id+"F0.wireOp",EDGE,"E12.48.0.6"),sQuery(id+"F0.wireOp",EDGE,"E12.48.0.7"),sQuery(id+"F0.wireOp",EDGE,"E12.48.0.8"),sQuery(id+"F0.wireOp",EDGE,"E12.48.0.9"),sQuery(id+"F0.wireOp",EDGE,"E12.48.0.10"),sQuery(id+"F0.wireOp",EDGE,"E12.49.0.0"),sQuery(id+"F0.wireOp",EDGE,"E12.49.0.1"),sQuery(id+"F0.wireOp",EDGE,"E12.49.0.2"),sQuery(id+"F0.wireOp",EDGE,"E12.49.0.4"),sQuery(id+"F0.wireOp",EDGE,"E12.49.0.5"),sQuery(id+"F0.wireOp",EDGE,"E12.49.0.6"),sQuery(id+"F0.wireOp",EDGE,"E12.49.0.7"),sQuery(id+"F0.wireOp",EDGE,"E12.49.0.8"),sQuery(id+"F0.wireOp",EDGE,"E12.49.0.9"),sQuery(id+"F0.wireOp",EDGE,"E12.49.0.10")])],"isStart":true});
            var sketch = newSketch(context, id + "F9", { "sketchPlane" : qUnion([Q0])});
            skLineSegment(sketch, "E19.bottom", {"start": v(0, 0) * mm, "end": v(-38.1, 0) * mm});
            skLineSegment(sketch, "E19.top", {"start": v(0, 8.26) * mm, "end": v(-38.1, 8.26) * mm});
            skLineSegment(sketch, "E19.left", {"start": v(0, 0) * mm, "end": v(0, 8.26) * mm});
            skLineSegment(sketch, "E19.right", {"start": v(-38.1, 0) * mm, "end": v(-38.1, 8.26) * mm});
            skSolve(sketch);
        }
        {
            var Q0;
            Q0 = qSketchRegion(id + "F9", true);
            extrude(context, id + "F10", {"entities" : qUnion([Q0]), "operationType" : NewBodyOperationType.ADD, "depth" : 50.8 * mm});
        }
        {
            var Q0;
            Q0=makeQuery(id+"F10.opExtrude","SWEPT_FACE",FACE,{"disambiguationData":[OSD([sQuery(id+"F9.wireOp",EDGE,"E19.top")])]});
            var sketch = newSketch(context, id + "F11", { "sketchPlane" : qUnion([Q0])});
            skCircle(sketch, "E20", {"center": v(10.16, 40.64) * mm, "radius": 2.54 * mm});
            skCircle(sketch, "E21", {"center": v(27.94, 40.64) * mm, "radius": 2.54 * mm});
            skSolve(sketch);
        }
        {
            var Q0;
            Q0 = qSketchRegion(id + "F11", true);
            extrude(context, id + "F12", {"entities" : qUnion([Q0]), "operationType" : NewBodyOperationType.REMOVE, "endBound" : BoundingType.THROUGH_ALL, "oppositeDirection" : true, "depth" : 25.4 * mm});
        }
        {
            var Q0;
            Q0=makeQuery(id+"F10.opExtrude","SWEPT_FACE",FACE,{"disambiguationData":[OSD([sQuery(id+"F9.wireOp",EDGE,"E19.top")])]});
            var sketch = newSketch(context, id + "F13", { "sketchPlane" : qUnion([Q0])});
            skCircle(sketch, "E22", {"center": v(10.16, 40.64) * mm, "radius": 3.81 * mm});
            skCircle(sketch, "E23", {"center": v(27.94, 40.64) * mm, "radius": 3.81 * mm});
            skSolve(sketch);
        }
        {
            var Q0;
            Q0 = qSketchRegion(id + "F13", true);
            extrude(context, id + "F14", {"entities" : qUnion([Q0]), "operationType" : NewBodyOperationType.REMOVE, "oppositeDirection" : true, "depth" : 2.54 * mm});
        }
        {
            var Q0;
            Q0=makeQuery(id+"F10.opExtrude","CAP_EDGE",EDGE,{"disambiguationData":[OSD([sQuery(id+"F9.wireOp",EDGE,"E19.right")])],"isStart":false});
            var Q1;
            Q1=makeQuery(id+"F10.opExtrude","CAP_EDGE",EDGE,{"disambiguationData":[OSD([sQuery(id+"F9.wireOp",EDGE,"E19.left")])],"isStart":false});
            fillet(context, id + "F15", {"entities" : qUnion([Q0, Q1]), "radius" : 5.08 * mm, "tangentPropagation" : true, "allowEdgeOverflow" : false});
        }
        {
            var Q0;
            Q0=makeQuery(id+"F1.opExtrude","CAP_FACE",FACE,{"disambiguationData":[OSD([sQuery(id+"F0.wireOp",EDGE,"E0.bottom"),sQuery(id+"F0.wireOp",EDGE,"E0.top"),sQuery(id+"F0.wireOp",EDGE,"E0.left"),sQuery(id+"F0.wireOp",EDGE,"E0.right"),sQuery(id+"F0.wireOp",EDGE,"E1"),sQuery(id+"F0.wireOp",EDGE,"E2"),sQuery(id+"F0.wireOp",EDGE,"E4"),sQuery(id+"F0.wireOp",EDGE,"E5.MirrorCS"),sQuery(id+"F0.wireOp",EDGE,"E6.MirrorCS"),sQuery(id+"F0.wireOp",EDGE,"E7.MirrorCS"),sQuery(id+"F0.wireOp",EDGE,"E8.filletArc"),sQuery(id+"F0.wireOp",EDGE,"E9.filletArc"),sQuery(id+"F0.wireOp",EDGE,"E10.filletArc"),sQuery(id+"F0.wireOp",EDGE,"E11.filletArc"),sQuery(id+"F0.wireOp",EDGE,"E12.1.0.0"),sQuery(id+"F0.wireOp",EDGE,"E12.1.0.1"),sQuery(id+"F0.wireOp",EDGE,"E12.1.0.2"),sQuery(id+"F0.wireOp",EDGE,"E12.1.0.4"),sQuery(id+"F0.wireOp",EDGE,"E12.1.0.5"),sQuery(id+"F0.wireOp",EDGE,"E12.1.0.6"),sQuery(id+"F0.wireOp",EDGE,"E12.1.0.7"),sQuery(id+"F0.wireOp",EDGE,"E12.1.0.8"),sQuery(id+"F0.wireOp",EDGE,"E12.1.0.9"),sQuery(id+"F0.wireOp",EDGE,"E12.1.0.10"),sQuery(id+"F0.wireOp",EDGE,"E12.2.0.0"),sQuery(id+"F0.wireOp",EDGE,"E12.2.0.1"),sQuery(id+"F0.wireOp",EDGE,"E12.2.0.2"),sQuery(id+"F0.wireOp",EDGE,"E12.2.0.4"),sQuery(id+"F0.wireOp",EDGE,"E12.2.0.5"),sQuery(id+"F0.wireOp",EDGE,"E12.2.0.6"),sQuery(id+"F0.wireOp",EDGE,"E12.2.0.7"),sQuery(id+"F0.wireOp",EDGE,"E12.2.0.8"),sQuery(id+"F0.wireOp",EDGE,"E12.2.0.9"),sQuery(id+"F0.wireOp",EDGE,"E12.2.0.10"),sQuery(id+"F0.wireOp",EDGE,"E12.3.0.0"),sQuery(id+"F0.wireOp",EDGE,"E12.3.0.1"),sQuery(id+"F0.wireOp",EDGE,"E12.3.0.2"),sQuery(id+"F0.wireOp",EDGE,"E12.3.0.4"),sQuery(id+"F0.wireOp",EDGE,"E12.3.0.5"),sQuery(id+"F0.wireOp",EDGE,"E12.3.0.6"),sQuery(id+"F0.wireOp",EDGE,"E12.3.0.7"),sQuery(id+"F0.wireOp",EDGE,"E12.3.0.8"),sQuery(id+"F0.wireOp",EDGE,"E12.3.0.9"),sQuery(id+"F0.wireOp",EDGE,"E12.3.0.10"),sQuery(id+"F0.wireOp",EDGE,"E12.4.0.0"),sQuery(id+"F0.wireOp",EDGE,"E12.4.0.1"),sQuery(id+"F0.wireOp",EDGE,"E12.4.0.2"),sQuery(id+"F0.wireOp",EDGE,"E12.4.0.4"),sQuery(id+"F0.wireOp",EDGE,"E12.4.0.5"),sQuery(id+"F0.wireOp",EDGE,"E12.4.0.6"),sQuery(id+"F0.wireOp",EDGE,"E12.4.0.7"),sQuery(id+"F0.wireOp",EDGE,"E12.4.0.8"),sQuery(id+"F0.wireOp",EDGE,"E12.4.0.9"),sQuery(id+"F0.wireOp",EDGE,"E12.4.0.10"),sQuery(id+"F0.wireOp",EDGE,"E12.5.0.0"),sQuery(id+"F0.wireOp",EDGE,"E12.5.0.1"),sQuery(id+"F0.wireOp",EDGE,"E12.5.0.2"),sQuery(id+"F0.wireOp",EDGE,"E12.5.0.4"),sQuery(id+"F0.wireOp",EDGE,"E12.5.0.5"),sQuery(id+"F0.wireOp",EDGE,"E12.5.0.6"),sQuery(id+"F0.wireOp",EDGE,"E12.5.0.7"),sQuery(id+"F0.wireOp",EDGE,"E12.5.0.8"),sQuery(id+"F0.wireOp",EDGE,"E12.5.0.9"),sQuery(id+"F0.wireOp",EDGE,"E12.5.0.10"),sQuery(id+"F0.wireOp",EDGE,"E12.6.0.0"),sQuery(id+"F0.wireOp",EDGE,"E12.6.0.1"),sQuery(id+"F0.wireOp",EDGE,"E12.6.0.2"),sQuery(id+"F0.wireOp",EDGE,"E12.6.0.4"),sQuery(id+"F0.wireOp",EDGE,"E12.6.0.5"),sQuery(id+"F0.wireOp",EDGE,"E12.6.0.6"),sQuery(id+"F0.wireOp",EDGE,"E12.6.0.7"),sQuery(id+"F0.wireOp",EDGE,"E12.6.0.8"),sQuery(id+"F0.wireOp",EDGE,"E12.6.0.9"),sQuery(id+"F0.wireOp",EDGE,"E12.6.0.10"),sQuery(id+"F0.wireOp",EDGE,"E12.7.0.0"),sQuery(id+"F0.wireOp",EDGE,"E12.7.0.1"),sQuery(id+"F0.wireOp",EDGE,"E12.7.0.2"),sQuery(id+"F0.wireOp",EDGE,"E12.7.0.4"),sQuery(id+"F0.wireOp",EDGE,"E12.7.0.5"),sQuery(id+"F0.wireOp",EDGE,"E12.7.0.6"),sQuery(id+"F0.wireOp",EDGE,"E12.7.0.7"),sQuery(id+"F0.wireOp",EDGE,"E12.7.0.8"),sQuery(id+"F0.wireOp",EDGE,"E12.7.0.9"),sQuery(id+"F0.wireOp",EDGE,"E12.7.0.10"),sQuery(id+"F0.wireOp",EDGE,"E12.8.0.0"),sQuery(id+"F0.wireOp",EDGE,"E12.8.0.1"),sQuery(id+"F0.wireOp",EDGE,"E12.8.0.2"),sQuery(id+"F0.wireOp",EDGE,"E12.8.0.4"),sQuery(id+"F0.wireOp",EDGE,"E12.8.0.5"),sQuery(id+"F0.wireOp",EDGE,"E12.8.0.6"),sQuery(id+"F0.wireOp",EDGE,"E12.8.0.7"),sQuery(id+"F0.wireOp",EDGE,"E12.8.0.8"),sQuery(id+"F0.wireOp",EDGE,"E12.8.0.9"),sQuery(id+"F0.wireOp",EDGE,"E12.8.0.10"),sQuery(id+"F0.wireOp",EDGE,"E12.9.0.0"),sQuery(id+"F0.wireOp",EDGE,"E12.9.0.1"),sQuery(id+"F0.wireOp",EDGE,"E12.9.0.2"),sQuery(id+"F0.wireOp",EDGE,"E12.9.0.4"),sQuery(id+"F0.wireOp",EDGE,"E12.9.0.5"),sQuery(id+"F0.wireOp",EDGE,"E12.9.0.6"),sQuery(id+"F0.wireOp",EDGE,"E12.9.0.7"),sQuery(id+"F0.wireOp",EDGE,"E12.9.0.8"),sQuery(id+"F0.wireOp",EDGE,"E12.9.0.9"),sQuery(id+"F0.wireOp",EDGE,"E12.9.0.10"),sQuery(id+"F0.wireOp",EDGE,"E12.10.0.0"),sQuery(id+"F0.wireOp",EDGE,"E12.10.0.1"),sQuery(id+"F0.wireOp",EDGE,"E12.10.0.2"),sQuery(id+"F0.wireOp",EDGE,"E12.10.0.4"),sQuery(id+"F0.wireOp",EDGE,"E12.10.0.5"),sQuery(id+"F0.wireOp",EDGE,"E12.10.0.6"),sQuery(id+"F0.wireOp",EDGE,"E12.10.0.7"),sQuery(id+"F0.wireOp",EDGE,"E12.10.0.8"),sQuery(id+"F0.wireOp",EDGE,"E12.10.0.9"),sQuery(id+"F0.wireOp",EDGE,"E12.10.0.10"),sQuery(id+"F0.wireOp",EDGE,"E12.11.0.0"),sQuery(id+"F0.wireOp",EDGE,"E12.11.0.1"),sQuery(id+"F0.wireOp",EDGE,"E12.11.0.2"),sQuery(id+"F0.wireOp",EDGE,"E12.11.0.4"),sQuery(id+"F0.wireOp",EDGE,"E12.11.0.5"),sQuery(id+"F0.wireOp",EDGE,"E12.11.0.6"),sQuery(id+"F0.wireOp",EDGE,"E12.11.0.7"),sQuery(id+"F0.wireOp",EDGE,"E12.11.0.8"),sQuery(id+"F0.wireOp",EDGE,"E12.11.0.9"),sQuery(id+"F0.wireOp",EDGE,"E12.11.0.10"),sQuery(id+"F0.wireOp",EDGE,"E12.12.0.0"),sQuery(id+"F0.wireOp",EDGE,"E12.12.0.1"),sQuery(id+"F0.wireOp",EDGE,"E12.12.0.2"),sQuery(id+"F0.wireOp",EDGE,"E12.12.0.4"),sQuery(id+"F0.wireOp",EDGE,"E12.12.0.5"),sQuery(id+"F0.wireOp",EDGE,"E12.12.0.6"),sQuery(id+"F0.wireOp",EDGE,"E12.12.0.7"),sQuery(id+"F0.wireOp",EDGE,"E12.12.0.8"),sQuery(id+"F0.wireOp",EDGE,"E12.12.0.9"),sQuery(id+"F0.wireOp",EDGE,"E12.12.0.10"),sQuery(id+"F0.wireOp",EDGE,"E12.13.0.0"),sQuery(id+"F0.wireOp",EDGE,"E12.13.0.1"),sQuery(id+"F0.wireOp",EDGE,"E12.13.0.2"),sQuery(id+"F0.wireOp",EDGE,"E12.13.0.4"),sQuery(id+"F0.wireOp",EDGE,"E12.13.0.5"),sQuery(id+"F0.wireOp",EDGE,"E12.13.0.6"),sQuery(id+"F0.wireOp",EDGE,"E12.13.0.7"),sQuery(id+"F0.wireOp",EDGE,"E12.13.0.8"),sQuery(id+"F0.wireOp",EDGE,"E12.13.0.9"),sQuery(id+"F0.wireOp",EDGE,"E12.13.0.10"),sQuery(id+"F0.wireOp",EDGE,"E12.14.0.0"),sQuery(id+"F0.wireOp",EDGE,"E12.14.0.1"),sQuery(id+"F0.wireOp",EDGE,"E12.14.0.2"),sQuery(id+"F0.wireOp",EDGE,"E12.14.0.4"),sQuery(id+"F0.wireOp",EDGE,"E12.14.0.5"),sQuery(id+"F0.wireOp",EDGE,"E12.14.0.6"),sQuery(id+"F0.wireOp",EDGE,"E12.14.0.7"),sQuery(id+"F0.wireOp",EDGE,"E12.14.0.8"),sQuery(id+"F0.wireOp",EDGE,"E12.14.0.9"),sQuery(id+"F0.wireOp",EDGE,"E12.14.0.10"),sQuery(id+"F0.wireOp",EDGE,"E12.15.0.0"),sQuery(id+"F0.wireOp",EDGE,"E12.15.0.1"),sQuery(id+"F0.wireOp",EDGE,"E12.15.0.2"),sQuery(id+"F0.wireOp",EDGE,"E12.15.0.4"),sQuery(id+"F0.wireOp",EDGE,"E12.15.0.5"),sQuery(id+"F0.wireOp",EDGE,"E12.15.0.6"),sQuery(id+"F0.wireOp",EDGE,"E12.15.0.7"),sQuery(id+"F0.wireOp",EDGE,"E12.15.0.8"),sQuery(id+"F0.wireOp",EDGE,"E12.15.0.9"),sQuery(id+"F0.wireOp",EDGE,"E12.15.0.10"),sQuery(id+"F0.wireOp",EDGE,"E12.16.0.0"),sQuery(id+"F0.wireOp",EDGE,"E12.16.0.1"),sQuery(id+"F0.wireOp",EDGE,"E12.16.0.2"),sQuery(id+"F0.wireOp",EDGE,"E12.16.0.4"),sQuery(id+"F0.wireOp",EDGE,"E12.16.0.5"),sQuery(id+"F0.wireOp",EDGE,"E12.16.0.6"),sQuery(id+"F0.wireOp",EDGE,"E12.16.0.7"),sQuery(id+"F0.wireOp",EDGE,"E12.16.0.8"),sQuery(id+"F0.wireOp",EDGE,"E12.16.0.9"),sQuery(id+"F0.wireOp",EDGE,"E12.16.0.10"),sQuery(id+"F0.wireOp",EDGE,"E12.17.0.0"),sQuery(id+"F0.wireOp",EDGE,"E12.17.0.1"),sQuery(id+"F0.wireOp",EDGE,"E12.17.0.2"),sQuery(id+"F0.wireOp",EDGE,"E12.17.0.4"),sQuery(id+"F0.wireOp",EDGE,"E12.17.0.5"),sQuery(id+"F0.wireOp",EDGE,"E12.17.0.6"),sQuery(id+"F0.wireOp",EDGE,"E12.17.0.7"),sQuery(id+"F0.wireOp",EDGE,"E12.17.0.8"),sQuery(id+"F0.wireOp",EDGE,"E12.17.0.9"),sQuery(id+"F0.wireOp",EDGE,"E12.17.0.10"),sQuery(id+"F0.wireOp",EDGE,"E12.18.0.0"),sQuery(id+"F0.wireOp",EDGE,"E12.18.0.1"),sQuery(id+"F0.wireOp",EDGE,"E12.18.0.2"),sQuery(id+"F0.wireOp",EDGE,"E12.18.0.4"),sQuery(id+"F0.wireOp",EDGE,"E12.18.0.5"),sQuery(id+"F0.wireOp",EDGE,"E12.18.0.6"),sQuery(id+"F0.wireOp",EDGE,"E12.18.0.7"),sQuery(id+"F0.wireOp",EDGE,"E12.18.0.8"),sQuery(id+"F0.wireOp",EDGE,"E12.18.0.9"),sQuery(id+"F0.wireOp",EDGE,"E12.18.0.10"),sQuery(id+"F0.wireOp",EDGE,"E12.19.0.0"),sQuery(id+"F0.wireOp",EDGE,"E12.19.0.1"),sQuery(id+"F0.wireOp",EDGE,"E12.19.0.2"),sQuery(id+"F0.wireOp",EDGE,"E12.19.0.4"),sQuery(id+"F0.wireOp",EDGE,"E12.19.0.5"),sQuery(id+"F0.wireOp",EDGE,"E12.19.0.6"),sQuery(id+"F0.wireOp",EDGE,"E12.19.0.7"),sQuery(id+"F0.wireOp",EDGE,"E12.19.0.8"),sQuery(id+"F0.wireOp",EDGE,"E12.19.0.9"),sQuery(id+"F0.wireOp",EDGE,"E12.19.0.10"),sQuery(id+"F0.wireOp",EDGE,"E12.20.0.0"),sQuery(id+"F0.wireOp",EDGE,"E12.20.0.1"),sQuery(id+"F0.wireOp",EDGE,"E12.20.0.2"),sQuery(id+"F0.wireOp",EDGE,"E12.20.0.4"),sQuery(id+"F0.wireOp",EDGE,"E12.20.0.5"),sQuery(id+"F0.wireOp",EDGE,"E12.20.0.6"),sQuery(id+"F0.wireOp",EDGE,"E12.20.0.7"),sQuery(id+"F0.wireOp",EDGE,"E12.20.0.8"),sQuery(id+"F0.wireOp",EDGE,"E12.20.0.9"),sQuery(id+"F0.wireOp",EDGE,"E12.20.0.10"),sQuery(id+"F0.wireOp",EDGE,"E12.21.0.0"),sQuery(id+"F0.wireOp",EDGE,"E12.21.0.1"),sQuery(id+"F0.wireOp",EDGE,"E12.21.0.2"),sQuery(id+"F0.wireOp",EDGE,"E12.21.0.4"),sQuery(id+"F0.wireOp",EDGE,"E12.21.0.5"),sQuery(id+"F0.wireOp",EDGE,"E12.21.0.6"),sQuery(id+"F0.wireOp",EDGE,"E12.21.0.7"),sQuery(id+"F0.wireOp",EDGE,"E12.21.0.8"),sQuery(id+"F0.wireOp",EDGE,"E12.21.0.9"),sQuery(id+"F0.wireOp",EDGE,"E12.21.0.10"),sQuery(id+"F0.wireOp",EDGE,"E12.22.0.0"),sQuery(id+"F0.wireOp",EDGE,"E12.22.0.1"),sQuery(id+"F0.wireOp",EDGE,"E12.22.0.2"),sQuery(id+"F0.wireOp",EDGE,"E12.22.0.4"),sQuery(id+"F0.wireOp",EDGE,"E12.22.0.5"),sQuery(id+"F0.wireOp",EDGE,"E12.22.0.6"),sQuery(id+"F0.wireOp",EDGE,"E12.22.0.7"),sQuery(id+"F0.wireOp",EDGE,"E12.22.0.8"),sQuery(id+"F0.wireOp",EDGE,"E12.22.0.9"),sQuery(id+"F0.wireOp",EDGE,"E12.22.0.10"),sQuery(id+"F0.wireOp",EDGE,"E12.23.0.0"),sQuery(id+"F0.wireOp",EDGE,"E12.23.0.1"),sQuery(id+"F0.wireOp",EDGE,"E12.23.0.2"),sQuery(id+"F0.wireOp",EDGE,"E12.23.0.4"),sQuery(id+"F0.wireOp",EDGE,"E12.23.0.5"),sQuery(id+"F0.wireOp",EDGE,"E12.23.0.6"),sQuery(id+"F0.wireOp",EDGE,"E12.23.0.7"),sQuery(id+"F0.wireOp",EDGE,"E12.23.0.8"),sQuery(id+"F0.wireOp",EDGE,"E12.23.0.9"),sQuery(id+"F0.wireOp",EDGE,"E12.23.0.10"),sQuery(id+"F0.wireOp",EDGE,"E12.24.0.0"),sQuery(id+"F0.wireOp",EDGE,"E12.24.0.1"),sQuery(id+"F0.wireOp",EDGE,"E12.24.0.2"),sQuery(id+"F0.wireOp",EDGE,"E12.24.0.4"),sQuery(id+"F0.wireOp",EDGE,"E12.24.0.5"),sQuery(id+"F0.wireOp",EDGE,"E12.24.0.6"),sQuery(id+"F0.wireOp",EDGE,"E12.24.0.7"),sQuery(id+"F0.wireOp",EDGE,"E12.24.0.8"),sQuery(id+"F0.wireOp",EDGE,"E12.24.0.9"),sQuery(id+"F0.wireOp",EDGE,"E12.24.0.10"),sQuery(id+"F0.wireOp",EDGE,"E12.25.0.0"),sQuery(id+"F0.wireOp",EDGE,"E12.25.0.1"),sQuery(id+"F0.wireOp",EDGE,"E12.25.0.2"),sQuery(id+"F0.wireOp",EDGE,"E12.25.0.4"),sQuery(id+"F0.wireOp",EDGE,"E12.25.0.5"),sQuery(id+"F0.wireOp",EDGE,"E12.25.0.6"),sQuery(id+"F0.wireOp",EDGE,"E12.25.0.7"),sQuery(id+"F0.wireOp",EDGE,"E12.25.0.8"),sQuery(id+"F0.wireOp",EDGE,"E12.25.0.9"),sQuery(id+"F0.wireOp",EDGE,"E12.25.0.10"),sQuery(id+"F0.wireOp",EDGE,"E12.26.0.0"),sQuery(id+"F0.wireOp",EDGE,"E12.26.0.1"),sQuery(id+"F0.wireOp",EDGE,"E12.26.0.2"),sQuery(id+"F0.wireOp",EDGE,"E12.26.0.4"),sQuery(id+"F0.wireOp",EDGE,"E12.26.0.5"),sQuery(id+"F0.wireOp",EDGE,"E12.26.0.6"),sQuery(id+"F0.wireOp",EDGE,"E12.26.0.7"),sQuery(id+"F0.wireOp",EDGE,"E12.26.0.8"),sQuery(id+"F0.wireOp",EDGE,"E12.26.0.9"),sQuery(id+"F0.wireOp",EDGE,"E12.26.0.10"),sQuery(id+"F0.wireOp",EDGE,"E12.27.0.0"),sQuery(id+"F0.wireOp",EDGE,"E12.27.0.1"),sQuery(id+"F0.wireOp",EDGE,"E12.27.0.2"),sQuery(id+"F0.wireOp",EDGE,"E12.27.0.4"),sQuery(id+"F0.wireOp",EDGE,"E12.27.0.5"),sQuery(id+"F0.wireOp",EDGE,"E12.27.0.6"),sQuery(id+"F0.wireOp",EDGE,"E12.27.0.7"),sQuery(id+"F0.wireOp",EDGE,"E12.27.0.8"),sQuery(id+"F0.wireOp",EDGE,"E12.27.0.9"),sQuery(id+"F0.wireOp",EDGE,"E12.27.0.10"),sQuery(id+"F0.wireOp",EDGE,"E12.28.0.0"),sQuery(id+"F0.wireOp",EDGE,"E12.28.0.1"),sQuery(id+"F0.wireOp",EDGE,"E12.28.0.2"),sQuery(id+"F0.wireOp",EDGE,"E12.28.0.4"),sQuery(id+"F0.wireOp",EDGE,"E12.28.0.5"),sQuery(id+"F0.wireOp",EDGE,"E12.28.0.6"),sQuery(id+"F0.wireOp",EDGE,"E12.28.0.7"),sQuery(id+"F0.wireOp",EDGE,"E12.28.0.8"),sQuery(id+"F0.wireOp",EDGE,"E12.28.0.9"),sQuery(id+"F0.wireOp",EDGE,"E12.28.0.10"),sQuery(id+"F0.wireOp",EDGE,"E12.29.0.0"),sQuery(id+"F0.wireOp",EDGE,"E12.29.0.1"),sQuery(id+"F0.wireOp",EDGE,"E12.29.0.2"),sQuery(id+"F0.wireOp",EDGE,"E12.29.0.4"),sQuery(id+"F0.wireOp",EDGE,"E12.29.0.5"),sQuery(id+"F0.wireOp",EDGE,"E12.29.0.6"),sQuery(id+"F0.wireOp",EDGE,"E12.29.0.7"),sQuery(id+"F0.wireOp",EDGE,"E12.29.0.8"),sQuery(id+"F0.wireOp",EDGE,"E12.29.0.9"),sQuery(id+"F0.wireOp",EDGE,"E12.29.0.10"),sQuery(id+"F0.wireOp",EDGE,"E12.30.0.0"),sQuery(id+"F0.wireOp",EDGE,"E12.30.0.1"),sQuery(id+"F0.wireOp",EDGE,"E12.30.0.2"),sQuery(id+"F0.wireOp",EDGE,"E12.30.0.4"),sQuery(id+"F0.wireOp",EDGE,"E12.30.0.5"),sQuery(id+"F0.wireOp",EDGE,"E12.30.0.6"),sQuery(id+"F0.wireOp",EDGE,"E12.30.0.7"),sQuery(id+"F0.wireOp",EDGE,"E12.30.0.8"),sQuery(id+"F0.wireOp",EDGE,"E12.30.0.9"),sQuery(id+"F0.wireOp",EDGE,"E12.30.0.10"),sQuery(id+"F0.wireOp",EDGE,"E12.31.0.0"),sQuery(id+"F0.wireOp",EDGE,"E12.31.0.1"),sQuery(id+"F0.wireOp",EDGE,"E12.31.0.2"),sQuery(id+"F0.wireOp",EDGE,"E12.31.0.4"),sQuery(id+"F0.wireOp",EDGE,"E12.31.0.5"),sQuery(id+"F0.wireOp",EDGE,"E12.31.0.6"),sQuery(id+"F0.wireOp",EDGE,"E12.31.0.7"),sQuery(id+"F0.wireOp",EDGE,"E12.31.0.8"),sQuery(id+"F0.wireOp",EDGE,"E12.31.0.9"),sQuery(id+"F0.wireOp",EDGE,"E12.31.0.10"),sQuery(id+"F0.wireOp",EDGE,"E12.32.0.0"),sQuery(id+"F0.wireOp",EDGE,"E12.32.0.1"),sQuery(id+"F0.wireOp",EDGE,"E12.32.0.2"),sQuery(id+"F0.wireOp",EDGE,"E12.32.0.4"),sQuery(id+"F0.wireOp",EDGE,"E12.32.0.5"),sQuery(id+"F0.wireOp",EDGE,"E12.32.0.6"),sQuery(id+"F0.wireOp",EDGE,"E12.32.0.7"),sQuery(id+"F0.wireOp",EDGE,"E12.32.0.8"),sQuery(id+"F0.wireOp",EDGE,"E12.32.0.9"),sQuery(id+"F0.wireOp",EDGE,"E12.32.0.10"),sQuery(id+"F0.wireOp",EDGE,"E12.33.0.0"),sQuery(id+"F0.wireOp",EDGE,"E12.33.0.1"),sQuery(id+"F0.wireOp",EDGE,"E12.33.0.2"),sQuery(id+"F0.wireOp",EDGE,"E12.33.0.4"),sQuery(id+"F0.wireOp",EDGE,"E12.33.0.5"),sQuery(id+"F0.wireOp",EDGE,"E12.33.0.6"),sQuery(id+"F0.wireOp",EDGE,"E12.33.0.7"),sQuery(id+"F0.wireOp",EDGE,"E12.33.0.8"),sQuery(id+"F0.wireOp",EDGE,"E12.33.0.9"),sQuery(id+"F0.wireOp",EDGE,"E12.33.0.10"),sQuery(id+"F0.wireOp",EDGE,"E12.34.0.0"),sQuery(id+"F0.wireOp",EDGE,"E12.34.0.1"),sQuery(id+"F0.wireOp",EDGE,"E12.34.0.2"),sQuery(id+"F0.wireOp",EDGE,"E12.34.0.4"),sQuery(id+"F0.wireOp",EDGE,"E12.34.0.5"),sQuery(id+"F0.wireOp",EDGE,"E12.34.0.6"),sQuery(id+"F0.wireOp",EDGE,"E12.34.0.7"),sQuery(id+"F0.wireOp",EDGE,"E12.34.0.8"),sQuery(id+"F0.wireOp",EDGE,"E12.34.0.9"),sQuery(id+"F0.wireOp",EDGE,"E12.34.0.10"),sQuery(id+"F0.wireOp",EDGE,"E12.35.0.0"),sQuery(id+"F0.wireOp",EDGE,"E12.35.0.1"),sQuery(id+"F0.wireOp",EDGE,"E12.35.0.2"),sQuery(id+"F0.wireOp",EDGE,"E12.35.0.4"),sQuery(id+"F0.wireOp",EDGE,"E12.35.0.5"),sQuery(id+"F0.wireOp",EDGE,"E12.35.0.6"),sQuery(id+"F0.wireOp",EDGE,"E12.35.0.7"),sQuery(id+"F0.wireOp",EDGE,"E12.35.0.8"),sQuery(id+"F0.wireOp",EDGE,"E12.35.0.9"),sQuery(id+"F0.wireOp",EDGE,"E12.35.0.10"),sQuery(id+"F0.wireOp",EDGE,"E12.36.0.0"),sQuery(id+"F0.wireOp",EDGE,"E12.36.0.1"),sQuery(id+"F0.wireOp",EDGE,"E12.36.0.2"),sQuery(id+"F0.wireOp",EDGE,"E12.36.0.4"),sQuery(id+"F0.wireOp",EDGE,"E12.36.0.5"),sQuery(id+"F0.wireOp",EDGE,"E12.36.0.6"),sQuery(id+"F0.wireOp",EDGE,"E12.36.0.7"),sQuery(id+"F0.wireOp",EDGE,"E12.36.0.8"),sQuery(id+"F0.wireOp",EDGE,"E12.36.0.9"),sQuery(id+"F0.wireOp",EDGE,"E12.36.0.10"),sQuery(id+"F0.wireOp",EDGE,"E12.37.0.0"),sQuery(id+"F0.wireOp",EDGE,"E12.37.0.1"),sQuery(id+"F0.wireOp",EDGE,"E12.37.0.2"),sQuery(id+"F0.wireOp",EDGE,"E12.37.0.4"),sQuery(id+"F0.wireOp",EDGE,"E12.37.0.5"),sQuery(id+"F0.wireOp",EDGE,"E12.37.0.6"),sQuery(id+"F0.wireOp",EDGE,"E12.37.0.7"),sQuery(id+"F0.wireOp",EDGE,"E12.37.0.8"),sQuery(id+"F0.wireOp",EDGE,"E12.37.0.9"),sQuery(id+"F0.wireOp",EDGE,"E12.37.0.10"),sQuery(id+"F0.wireOp",EDGE,"E12.38.0.0"),sQuery(id+"F0.wireOp",EDGE,"E12.38.0.1"),sQuery(id+"F0.wireOp",EDGE,"E12.38.0.2"),sQuery(id+"F0.wireOp",EDGE,"E12.38.0.4"),sQuery(id+"F0.wireOp",EDGE,"E12.38.0.5"),sQuery(id+"F0.wireOp",EDGE,"E12.38.0.6"),sQuery(id+"F0.wireOp",EDGE,"E12.38.0.7"),sQuery(id+"F0.wireOp",EDGE,"E12.38.0.8"),sQuery(id+"F0.wireOp",EDGE,"E12.38.0.9"),sQuery(id+"F0.wireOp",EDGE,"E12.38.0.10"),sQuery(id+"F0.wireOp",EDGE,"E12.39.0.0"),sQuery(id+"F0.wireOp",EDGE,"E12.39.0.1"),sQuery(id+"F0.wireOp",EDGE,"E12.39.0.2"),sQuery(id+"F0.wireOp",EDGE,"E12.39.0.4"),sQuery(id+"F0.wireOp",EDGE,"E12.39.0.5"),sQuery(id+"F0.wireOp",EDGE,"E12.39.0.6"),sQuery(id+"F0.wireOp",EDGE,"E12.39.0.7"),sQuery(id+"F0.wireOp",EDGE,"E12.39.0.8"),sQuery(id+"F0.wireOp",EDGE,"E12.39.0.9"),sQuery(id+"F0.wireOp",EDGE,"E12.39.0.10"),sQuery(id+"F0.wireOp",EDGE,"E12.40.0.0"),sQuery(id+"F0.wireOp",EDGE,"E12.40.0.1"),sQuery(id+"F0.wireOp",EDGE,"E12.40.0.2"),sQuery(id+"F0.wireOp",EDGE,"E12.40.0.4"),sQuery(id+"F0.wireOp",EDGE,"E12.40.0.5"),sQuery(id+"F0.wireOp",EDGE,"E12.40.0.6"),sQuery(id+"F0.wireOp",EDGE,"E12.40.0.7"),sQuery(id+"F0.wireOp",EDGE,"E12.40.0.8"),sQuery(id+"F0.wireOp",EDGE,"E12.40.0.9"),sQuery(id+"F0.wireOp",EDGE,"E12.40.0.10"),sQuery(id+"F0.wireOp",EDGE,"E12.41.0.0"),sQuery(id+"F0.wireOp",EDGE,"E12.41.0.1"),sQuery(id+"F0.wireOp",EDGE,"E12.41.0.2"),sQuery(id+"F0.wireOp",EDGE,"E12.41.0.4"),sQuery(id+"F0.wireOp",EDGE,"E12.41.0.5"),sQuery(id+"F0.wireOp",EDGE,"E12.41.0.6"),sQuery(id+"F0.wireOp",EDGE,"E12.41.0.7"),sQuery(id+"F0.wireOp",EDGE,"E12.41.0.8"),sQuery(id+"F0.wireOp",EDGE,"E12.41.0.9"),sQuery(id+"F0.wireOp",EDGE,"E12.41.0.10"),sQuery(id+"F0.wireOp",EDGE,"E12.42.0.0"),sQuery(id+"F0.wireOp",EDGE,"E12.42.0.1"),sQuery(id+"F0.wireOp",EDGE,"E12.42.0.2"),sQuery(id+"F0.wireOp",EDGE,"E12.42.0.4"),sQuery(id+"F0.wireOp",EDGE,"E12.42.0.5"),sQuery(id+"F0.wireOp",EDGE,"E12.42.0.6"),sQuery(id+"F0.wireOp",EDGE,"E12.42.0.7"),sQuery(id+"F0.wireOp",EDGE,"E12.42.0.8"),sQuery(id+"F0.wireOp",EDGE,"E12.42.0.9"),sQuery(id+"F0.wireOp",EDGE,"E12.42.0.10"),sQuery(id+"F0.wireOp",EDGE,"E12.43.0.0"),sQuery(id+"F0.wireOp",EDGE,"E12.43.0.1"),sQuery(id+"F0.wireOp",EDGE,"E12.43.0.2"),sQuery(id+"F0.wireOp",EDGE,"E12.43.0.4"),sQuery(id+"F0.wireOp",EDGE,"E12.43.0.5"),sQuery(id+"F0.wireOp",EDGE,"E12.43.0.6"),sQuery(id+"F0.wireOp",EDGE,"E12.43.0.7"),sQuery(id+"F0.wireOp",EDGE,"E12.43.0.8"),sQuery(id+"F0.wireOp",EDGE,"E12.43.0.9"),sQuery(id+"F0.wireOp",EDGE,"E12.43.0.10"),sQuery(id+"F0.wireOp",EDGE,"E12.44.0.0"),sQuery(id+"F0.wireOp",EDGE,"E12.44.0.1"),sQuery(id+"F0.wireOp",EDGE,"E12.44.0.2"),sQuery(id+"F0.wireOp",EDGE,"E12.44.0.4"),sQuery(id+"F0.wireOp",EDGE,"E12.44.0.5"),sQuery(id+"F0.wireOp",EDGE,"E12.44.0.6"),sQuery(id+"F0.wireOp",EDGE,"E12.44.0.7"),sQuery(id+"F0.wireOp",EDGE,"E12.44.0.8"),sQuery(id+"F0.wireOp",EDGE,"E12.44.0.9"),sQuery(id+"F0.wireOp",EDGE,"E12.44.0.10"),sQuery(id+"F0.wireOp",EDGE,"E12.45.0.0"),sQuery(id+"F0.wireOp",EDGE,"E12.45.0.1"),sQuery(id+"F0.wireOp",EDGE,"E12.45.0.2"),sQuery(id+"F0.wireOp",EDGE,"E12.45.0.4"),sQuery(id+"F0.wireOp",EDGE,"E12.45.0.5"),sQuery(id+"F0.wireOp",EDGE,"E12.45.0.6"),sQuery(id+"F0.wireOp",EDGE,"E12.45.0.7"),sQuery(id+"F0.wireOp",EDGE,"E12.45.0.8"),sQuery(id+"F0.wireOp",EDGE,"E12.45.0.9"),sQuery(id+"F0.wireOp",EDGE,"E12.45.0.10"),sQuery(id+"F0.wireOp",EDGE,"E12.46.0.0"),sQuery(id+"F0.wireOp",EDGE,"E12.46.0.1"),sQuery(id+"F0.wireOp",EDGE,"E12.46.0.2"),sQuery(id+"F0.wireOp",EDGE,"E12.46.0.4"),sQuery(id+"F0.wireOp",EDGE,"E12.46.0.5"),sQuery(id+"F0.wireOp",EDGE,"E12.46.0.6"),sQuery(id+"F0.wireOp",EDGE,"E12.46.0.7"),sQuery(id+"F0.wireOp",EDGE,"E12.46.0.8"),sQuery(id+"F0.wireOp",EDGE,"E12.46.0.9"),sQuery(id+"F0.wireOp",EDGE,"E12.46.0.10"),sQuery(id+"F0.wireOp",EDGE,"E12.47.0.0"),sQuery(id+"F0.wireOp",EDGE,"E12.47.0.1"),sQuery(id+"F0.wireOp",EDGE,"E12.47.0.2"),sQuery(id+"F0.wireOp",EDGE,"E12.47.0.4"),sQuery(id+"F0.wireOp",EDGE,"E12.47.0.5"),sQuery(id+"F0.wireOp",EDGE,"E12.47.0.6"),sQuery(id+"F0.wireOp",EDGE,"E12.47.0.7"),sQuery(id+"F0.wireOp",EDGE,"E12.47.0.8"),sQuery(id+"F0.wireOp",EDGE,"E12.47.0.9"),sQuery(id+"F0.wireOp",EDGE,"E12.47.0.10"),sQuery(id+"F0.wireOp",EDGE,"E12.48.0.0"),sQuery(id+"F0.wireOp",EDGE,"E12.48.0.1"),sQuery(id+"F0.wireOp",EDGE,"E12.48.0.2"),sQuery(id+"F0.wireOp",EDGE,"E12.48.0.4"),sQuery(id+"F0.wireOp",EDGE,"E12.48.0.5"),sQuery(id+"F0.wireOp",EDGE,"E12.48.0.6"),sQuery(id+"F0.wireOp",EDGE,"E12.48.0.7"),sQuery(id+"F0.wireOp",EDGE,"E12.48.0.8"),sQuery(id+"F0.wireOp",EDGE,"E12.48.0.9"),sQuery(id+"F0.wireOp",EDGE,"E12.48.0.10"),sQuery(id+"F0.wireOp",EDGE,"E12.49.0.0"),sQuery(id+"F0.wireOp",EDGE,"E12.49.0.1"),sQuery(id+"F0.wireOp",EDGE,"E12.49.0.2"),sQuery(id+"F0.wireOp",EDGE,"E12.49.0.4"),sQuery(id+"F0.wireOp",EDGE,"E12.49.0.5"),sQuery(id+"F0.wireOp",EDGE,"E12.49.0.6"),sQuery(id+"F0.wireOp",EDGE,"E12.49.0.7"),sQuery(id+"F0.wireOp",EDGE,"E12.49.0.8"),sQuery(id+"F0.wireOp",EDGE,"E12.49.0.9"),sQuery(id+"F0.wireOp",EDGE,"E12.49.0.10")])],"isStart":true});
            var sketch = newSketch(context, id + "F16", { "sketchPlane" : qUnion([Q0])});
            skLineSegment(sketch, "E24.bottom", {"start": v(-762, 0) * mm, "end": v(-723.9, 0) * mm});
            skLineSegment(sketch, "E24.top", {"start": v(-762, 8.25) * mm, "end": v(-723.9, 8.25) * mm});
            skLineSegment(sketch, "E24.left", {"start": v(-762, 0) * mm, "end": v(-762, 8.25) * mm});
            skLineSegment(sketch, "E24.right", {"start": v(-723.9, 0) * mm, "end": v(-723.9, 8.25) * mm});
            skSolve(sketch);
        }
        {
            var Q0;
            Q0=makeQuery(id+"F16.imprint","IMPRINT",FACE,{"disambiguationData":[TD([[makeQuery(id+"F16.imprint","IMPRINT",EDGE,{"derivedFrom":sQuery(id+"F16.wireOp",EDGE,"E24.bottom")}),-1.0]])]});
            extrude(context, id + "F17", {"entities" : qUnion([Q0]), "operationType" : NewBodyOperationType.ADD, "depth" : 50.8 * mm});
        }
        {
            var Q0;
            Q0=makeQuery(id+"F17.opExtrude","SWEPT_FACE",FACE,{"disambiguationData":[OSD([sQuery(id+"F16.wireOp",EDGE,"E24.top")])]});
            var sketch = newSketch(context, id + "F18", { "sketchPlane" : qUnion([Q0])});
            skCircle(sketch, "E25", {"center": v(734.06, 40.64) * mm, "radius": 2.54 * mm});
            skCircle(sketch, "E26", {"center": v(751.84, 40.64) * mm, "radius": 2.54 * mm});
            skCircle(sketch, "E27", {"center": v(734.06, 40.64) * mm, "radius": 3.81 * mm});
            skCircle(sketch, "E28", {"center": v(751.84, 40.64) * mm, "radius": 3.81 * mm});
            skSolve(sketch);
        }
        {
            var Q0;
            Q0=makeQuery(id+"F18.imprint","IMPRINT",FACE,{"disambiguationData":[TD([[makeQuery(id+"F18.imprint","IMPRINT",EDGE,{"derivedFrom":sQuery(id+"F18.wireOp",EDGE,"E25")}),1.0]])]});
            var Q1;
            Q1=makeQuery(id+"F18.imprint","IMPRINT",FACE,{"disambiguationData":[TD([[makeQuery(id+"F18.imprint","IMPRINT",EDGE,{"derivedFrom":sQuery(id+"F18.wireOp",EDGE,"E26")}),1.0]])]});
            extrude(context, id + "F19", {"entities" : qUnion([Q0, Q1]), "operationType" : NewBodyOperationType.REMOVE, "endBound" : BoundingType.THROUGH_ALL, "oppositeDirection" : true, "depth" : 25.4 * mm});
        }
        {
            var Q0;
            Q0=makeQuery(id+"F17.opExtrude","SWEPT_FACE",FACE,{"disambiguationData":[OSD([sQuery(id+"F16.wireOp",EDGE,"E24.top")])]});
            var sketch = newSketch(context, id + "F20", { "sketchPlane" : qUnion([Q0])});
            skCircle(sketch, "E29", {"center": v(734.06, 40.64) * mm, "radius": 3.81 * mm});
            skCircle(sketch, "E30", {"center": v(751.84, 40.64) * mm, "radius": 3.81 * mm});
            skSolve(sketch);
        }
        {
            var Q0;
            Q0=makeQuery(id+"F20.imprint","IMPRINT",FACE,{"disambiguationData":[TD([[makeQuery(id+"F20.imprint","IMPRINT",EDGE,{"derivedFrom":sQuery(id+"F20.wireOp",EDGE,"E29")}),1.0]])]});
            var Q1;
            Q1=makeQuery(id+"F20.imprint","IMPRINT",FACE,{"disambiguationData":[TD([[makeQuery(id+"F20.imprint","IMPRINT",EDGE,{"derivedFrom":sQuery(id+"F20.wireOp",EDGE,"E30")}),1.0]])]});
            extrude(context, id + "F21", {"entities" : qUnion([Q0, Q1]), "operationType" : NewBodyOperationType.REMOVE, "oppositeDirection" : true, "depth" : 2.54 * mm});
        }
        {
            var Q0;
            Q0=makeQuery(id+"F17.opExtrude","CAP_EDGE",EDGE,{"disambiguationData":[OSD([sQuery(id+"F16.wireOp",EDGE,"E24.right")])],"isStart":false});
            var Q1;
            Q1=makeQuery(id+"F17.opExtrude","CAP_EDGE",EDGE,{"disambiguationData":[OSD([sQuery(id+"F16.wireOp",EDGE,"E24.left")])],"isStart":false});
            fillet(context, id + "F22", {"entities" : qUnion([Q0, Q1]), "radius" : 5.08 * mm, "tangentPropagation" : true, "allowEdgeOverflow" : false});
        }
        {
            var Q0;
            Q0=makeQuery(id+"F1.opExtrude","CAP_FACE",FACE,{"disambiguationData":[OSD([sQuery(id+"F0.wireOp",EDGE,"E0.bottom"),sQuery(id+"F0.wireOp",EDGE,"E0.top"),sQuery(id+"F0.wireOp",EDGE,"E0.left"),sQuery(id+"F0.wireOp",EDGE,"E0.right"),sQuery(id+"F0.wireOp",EDGE,"E1"),sQuery(id+"F0.wireOp",EDGE,"E2"),sQuery(id+"F0.wireOp",EDGE,"E4"),sQuery(id+"F0.wireOp",EDGE,"E5.MirrorCS"),sQuery(id+"F0.wireOp",EDGE,"E6.MirrorCS"),sQuery(id+"F0.wireOp",EDGE,"E7.MirrorCS"),sQuery(id+"F0.wireOp",EDGE,"E8.filletArc"),sQuery(id+"F0.wireOp",EDGE,"E9.filletArc"),sQuery(id+"F0.wireOp",EDGE,"E10.filletArc"),sQuery(id+"F0.wireOp",EDGE,"E11.filletArc"),sQuery(id+"F0.wireOp",EDGE,"E12.1.0.0"),sQuery(id+"F0.wireOp",EDGE,"E12.1.0.1"),sQuery(id+"F0.wireOp",EDGE,"E12.1.0.2"),sQuery(id+"F0.wireOp",EDGE,"E12.1.0.4"),sQuery(id+"F0.wireOp",EDGE,"E12.1.0.5"),sQuery(id+"F0.wireOp",EDGE,"E12.1.0.6"),sQuery(id+"F0.wireOp",EDGE,"E12.1.0.7"),sQuery(id+"F0.wireOp",EDGE,"E12.1.0.8"),sQuery(id+"F0.wireOp",EDGE,"E12.1.0.9"),sQuery(id+"F0.wireOp",EDGE,"E12.1.0.10"),sQuery(id+"F0.wireOp",EDGE,"E12.2.0.0"),sQuery(id+"F0.wireOp",EDGE,"E12.2.0.1"),sQuery(id+"F0.wireOp",EDGE,"E12.2.0.2"),sQuery(id+"F0.wireOp",EDGE,"E12.2.0.4"),sQuery(id+"F0.wireOp",EDGE,"E12.2.0.5"),sQuery(id+"F0.wireOp",EDGE,"E12.2.0.6"),sQuery(id+"F0.wireOp",EDGE,"E12.2.0.7"),sQuery(id+"F0.wireOp",EDGE,"E12.2.0.8"),sQuery(id+"F0.wireOp",EDGE,"E12.2.0.9"),sQuery(id+"F0.wireOp",EDGE,"E12.2.0.10"),sQuery(id+"F0.wireOp",EDGE,"E12.3.0.0"),sQuery(id+"F0.wireOp",EDGE,"E12.3.0.1"),sQuery(id+"F0.wireOp",EDGE,"E12.3.0.2"),sQuery(id+"F0.wireOp",EDGE,"E12.3.0.4"),sQuery(id+"F0.wireOp",EDGE,"E12.3.0.5"),sQuery(id+"F0.wireOp",EDGE,"E12.3.0.6"),sQuery(id+"F0.wireOp",EDGE,"E12.3.0.7"),sQuery(id+"F0.wireOp",EDGE,"E12.3.0.8"),sQuery(id+"F0.wireOp",EDGE,"E12.3.0.9"),sQuery(id+"F0.wireOp",EDGE,"E12.3.0.10"),sQuery(id+"F0.wireOp",EDGE,"E12.4.0.0"),sQuery(id+"F0.wireOp",EDGE,"E12.4.0.1"),sQuery(id+"F0.wireOp",EDGE,"E12.4.0.2"),sQuery(id+"F0.wireOp",EDGE,"E12.4.0.4"),sQuery(id+"F0.wireOp",EDGE,"E12.4.0.5"),sQuery(id+"F0.wireOp",EDGE,"E12.4.0.6"),sQuery(id+"F0.wireOp",EDGE,"E12.4.0.7"),sQuery(id+"F0.wireOp",EDGE,"E12.4.0.8"),sQuery(id+"F0.wireOp",EDGE,"E12.4.0.9"),sQuery(id+"F0.wireOp",EDGE,"E12.4.0.10"),sQuery(id+"F0.wireOp",EDGE,"E12.5.0.0"),sQuery(id+"F0.wireOp",EDGE,"E12.5.0.1"),sQuery(id+"F0.wireOp",EDGE,"E12.5.0.2"),sQuery(id+"F0.wireOp",EDGE,"E12.5.0.4"),sQuery(id+"F0.wireOp",EDGE,"E12.5.0.5"),sQuery(id+"F0.wireOp",EDGE,"E12.5.0.6"),sQuery(id+"F0.wireOp",EDGE,"E12.5.0.7"),sQuery(id+"F0.wireOp",EDGE,"E12.5.0.8"),sQuery(id+"F0.wireOp",EDGE,"E12.5.0.9"),sQuery(id+"F0.wireOp",EDGE,"E12.5.0.10"),sQuery(id+"F0.wireOp",EDGE,"E12.6.0.0"),sQuery(id+"F0.wireOp",EDGE,"E12.6.0.1"),sQuery(id+"F0.wireOp",EDGE,"E12.6.0.2"),sQuery(id+"F0.wireOp",EDGE,"E12.6.0.4"),sQuery(id+"F0.wireOp",EDGE,"E12.6.0.5"),sQuery(id+"F0.wireOp",EDGE,"E12.6.0.6"),sQuery(id+"F0.wireOp",EDGE,"E12.6.0.7"),sQuery(id+"F0.wireOp",EDGE,"E12.6.0.8"),sQuery(id+"F0.wireOp",EDGE,"E12.6.0.9"),sQuery(id+"F0.wireOp",EDGE,"E12.6.0.10"),sQuery(id+"F0.wireOp",EDGE,"E12.7.0.0"),sQuery(id+"F0.wireOp",EDGE,"E12.7.0.1"),sQuery(id+"F0.wireOp",EDGE,"E12.7.0.2"),sQuery(id+"F0.wireOp",EDGE,"E12.7.0.4"),sQuery(id+"F0.wireOp",EDGE,"E12.7.0.5"),sQuery(id+"F0.wireOp",EDGE,"E12.7.0.6"),sQuery(id+"F0.wireOp",EDGE,"E12.7.0.7"),sQuery(id+"F0.wireOp",EDGE,"E12.7.0.8"),sQuery(id+"F0.wireOp",EDGE,"E12.7.0.9"),sQuery(id+"F0.wireOp",EDGE,"E12.7.0.10"),sQuery(id+"F0.wireOp",EDGE,"E12.8.0.0"),sQuery(id+"F0.wireOp",EDGE,"E12.8.0.1"),sQuery(id+"F0.wireOp",EDGE,"E12.8.0.2"),sQuery(id+"F0.wireOp",EDGE,"E12.8.0.4"),sQuery(id+"F0.wireOp",EDGE,"E12.8.0.5"),sQuery(id+"F0.wireOp",EDGE,"E12.8.0.6"),sQuery(id+"F0.wireOp",EDGE,"E12.8.0.7"),sQuery(id+"F0.wireOp",EDGE,"E12.8.0.8"),sQuery(id+"F0.wireOp",EDGE,"E12.8.0.9"),sQuery(id+"F0.wireOp",EDGE,"E12.8.0.10"),sQuery(id+"F0.wireOp",EDGE,"E12.9.0.0"),sQuery(id+"F0.wireOp",EDGE,"E12.9.0.1"),sQuery(id+"F0.wireOp",EDGE,"E12.9.0.2"),sQuery(id+"F0.wireOp",EDGE,"E12.9.0.4"),sQuery(id+"F0.wireOp",EDGE,"E12.9.0.5"),sQuery(id+"F0.wireOp",EDGE,"E12.9.0.6"),sQuery(id+"F0.wireOp",EDGE,"E12.9.0.7"),sQuery(id+"F0.wireOp",EDGE,"E12.9.0.8"),sQuery(id+"F0.wireOp",EDGE,"E12.9.0.9"),sQuery(id+"F0.wireOp",EDGE,"E12.9.0.10"),sQuery(id+"F0.wireOp",EDGE,"E12.10.0.0"),sQuery(id+"F0.wireOp",EDGE,"E12.10.0.1"),sQuery(id+"F0.wireOp",EDGE,"E12.10.0.2"),sQuery(id+"F0.wireOp",EDGE,"E12.10.0.4"),sQuery(id+"F0.wireOp",EDGE,"E12.10.0.5"),sQuery(id+"F0.wireOp",EDGE,"E12.10.0.6"),sQuery(id+"F0.wireOp",EDGE,"E12.10.0.7"),sQuery(id+"F0.wireOp",EDGE,"E12.10.0.8"),sQuery(id+"F0.wireOp",EDGE,"E12.10.0.9"),sQuery(id+"F0.wireOp",EDGE,"E12.10.0.10"),sQuery(id+"F0.wireOp",EDGE,"E12.11.0.0"),sQuery(id+"F0.wireOp",EDGE,"E12.11.0.1"),sQuery(id+"F0.wireOp",EDGE,"E12.11.0.2"),sQuery(id+"F0.wireOp",EDGE,"E12.11.0.4"),sQuery(id+"F0.wireOp",EDGE,"E12.11.0.5"),sQuery(id+"F0.wireOp",EDGE,"E12.11.0.6"),sQuery(id+"F0.wireOp",EDGE,"E12.11.0.7"),sQuery(id+"F0.wireOp",EDGE,"E12.11.0.8"),sQuery(id+"F0.wireOp",EDGE,"E12.11.0.9"),sQuery(id+"F0.wireOp",EDGE,"E12.11.0.10"),sQuery(id+"F0.wireOp",EDGE,"E12.12.0.0"),sQuery(id+"F0.wireOp",EDGE,"E12.12.0.1"),sQuery(id+"F0.wireOp",EDGE,"E12.12.0.2"),sQuery(id+"F0.wireOp",EDGE,"E12.12.0.4"),sQuery(id+"F0.wireOp",EDGE,"E12.12.0.5"),sQuery(id+"F0.wireOp",EDGE,"E12.12.0.6"),sQuery(id+"F0.wireOp",EDGE,"E12.12.0.7"),sQuery(id+"F0.wireOp",EDGE,"E12.12.0.8"),sQuery(id+"F0.wireOp",EDGE,"E12.12.0.9"),sQuery(id+"F0.wireOp",EDGE,"E12.12.0.10"),sQuery(id+"F0.wireOp",EDGE,"E12.13.0.0"),sQuery(id+"F0.wireOp",EDGE,"E12.13.0.1"),sQuery(id+"F0.wireOp",EDGE,"E12.13.0.2"),sQuery(id+"F0.wireOp",EDGE,"E12.13.0.4"),sQuery(id+"F0.wireOp",EDGE,"E12.13.0.5"),sQuery(id+"F0.wireOp",EDGE,"E12.13.0.6"),sQuery(id+"F0.wireOp",EDGE,"E12.13.0.7"),sQuery(id+"F0.wireOp",EDGE,"E12.13.0.8"),sQuery(id+"F0.wireOp",EDGE,"E12.13.0.9"),sQuery(id+"F0.wireOp",EDGE,"E12.13.0.10"),sQuery(id+"F0.wireOp",EDGE,"E12.14.0.0"),sQuery(id+"F0.wireOp",EDGE,"E12.14.0.1"),sQuery(id+"F0.wireOp",EDGE,"E12.14.0.2"),sQuery(id+"F0.wireOp",EDGE,"E12.14.0.4"),sQuery(id+"F0.wireOp",EDGE,"E12.14.0.5"),sQuery(id+"F0.wireOp",EDGE,"E12.14.0.6"),sQuery(id+"F0.wireOp",EDGE,"E12.14.0.7"),sQuery(id+"F0.wireOp",EDGE,"E12.14.0.8"),sQuery(id+"F0.wireOp",EDGE,"E12.14.0.9"),sQuery(id+"F0.wireOp",EDGE,"E12.14.0.10"),sQuery(id+"F0.wireOp",EDGE,"E12.15.0.0"),sQuery(id+"F0.wireOp",EDGE,"E12.15.0.1"),sQuery(id+"F0.wireOp",EDGE,"E12.15.0.2"),sQuery(id+"F0.wireOp",EDGE,"E12.15.0.4"),sQuery(id+"F0.wireOp",EDGE,"E12.15.0.5"),sQuery(id+"F0.wireOp",EDGE,"E12.15.0.6"),sQuery(id+"F0.wireOp",EDGE,"E12.15.0.7"),sQuery(id+"F0.wireOp",EDGE,"E12.15.0.8"),sQuery(id+"F0.wireOp",EDGE,"E12.15.0.9"),sQuery(id+"F0.wireOp",EDGE,"E12.15.0.10"),sQuery(id+"F0.wireOp",EDGE,"E12.16.0.0"),sQuery(id+"F0.wireOp",EDGE,"E12.16.0.1"),sQuery(id+"F0.wireOp",EDGE,"E12.16.0.2"),sQuery(id+"F0.wireOp",EDGE,"E12.16.0.4"),sQuery(id+"F0.wireOp",EDGE,"E12.16.0.5"),sQuery(id+"F0.wireOp",EDGE,"E12.16.0.6"),sQuery(id+"F0.wireOp",EDGE,"E12.16.0.7"),sQuery(id+"F0.wireOp",EDGE,"E12.16.0.8"),sQuery(id+"F0.wireOp",EDGE,"E12.16.0.9"),sQuery(id+"F0.wireOp",EDGE,"E12.16.0.10"),sQuery(id+"F0.wireOp",EDGE,"E12.17.0.0"),sQuery(id+"F0.wireOp",EDGE,"E12.17.0.1"),sQuery(id+"F0.wireOp",EDGE,"E12.17.0.2"),sQuery(id+"F0.wireOp",EDGE,"E12.17.0.4"),sQuery(id+"F0.wireOp",EDGE,"E12.17.0.5"),sQuery(id+"F0.wireOp",EDGE,"E12.17.0.6"),sQuery(id+"F0.wireOp",EDGE,"E12.17.0.7"),sQuery(id+"F0.wireOp",EDGE,"E12.17.0.8"),sQuery(id+"F0.wireOp",EDGE,"E12.17.0.9"),sQuery(id+"F0.wireOp",EDGE,"E12.17.0.10"),sQuery(id+"F0.wireOp",EDGE,"E12.18.0.0"),sQuery(id+"F0.wireOp",EDGE,"E12.18.0.1"),sQuery(id+"F0.wireOp",EDGE,"E12.18.0.2"),sQuery(id+"F0.wireOp",EDGE,"E12.18.0.4"),sQuery(id+"F0.wireOp",EDGE,"E12.18.0.5"),sQuery(id+"F0.wireOp",EDGE,"E12.18.0.6"),sQuery(id+"F0.wireOp",EDGE,"E12.18.0.7"),sQuery(id+"F0.wireOp",EDGE,"E12.18.0.8"),sQuery(id+"F0.wireOp",EDGE,"E12.18.0.9"),sQuery(id+"F0.wireOp",EDGE,"E12.18.0.10"),sQuery(id+"F0.wireOp",EDGE,"E12.19.0.0"),sQuery(id+"F0.wireOp",EDGE,"E12.19.0.1"),sQuery(id+"F0.wireOp",EDGE,"E12.19.0.2"),sQuery(id+"F0.wireOp",EDGE,"E12.19.0.4"),sQuery(id+"F0.wireOp",EDGE,"E12.19.0.5"),sQuery(id+"F0.wireOp",EDGE,"E12.19.0.6"),sQuery(id+"F0.wireOp",EDGE,"E12.19.0.7"),sQuery(id+"F0.wireOp",EDGE,"E12.19.0.8"),sQuery(id+"F0.wireOp",EDGE,"E12.19.0.9"),sQuery(id+"F0.wireOp",EDGE,"E12.19.0.10"),sQuery(id+"F0.wireOp",EDGE,"E12.20.0.0"),sQuery(id+"F0.wireOp",EDGE,"E12.20.0.1"),sQuery(id+"F0.wireOp",EDGE,"E12.20.0.2"),sQuery(id+"F0.wireOp",EDGE,"E12.20.0.4"),sQuery(id+"F0.wireOp",EDGE,"E12.20.0.5"),sQuery(id+"F0.wireOp",EDGE,"E12.20.0.6"),sQuery(id+"F0.wireOp",EDGE,"E12.20.0.7"),sQuery(id+"F0.wireOp",EDGE,"E12.20.0.8"),sQuery(id+"F0.wireOp",EDGE,"E12.20.0.9"),sQuery(id+"F0.wireOp",EDGE,"E12.20.0.10"),sQuery(id+"F0.wireOp",EDGE,"E12.21.0.0"),sQuery(id+"F0.wireOp",EDGE,"E12.21.0.1"),sQuery(id+"F0.wireOp",EDGE,"E12.21.0.2"),sQuery(id+"F0.wireOp",EDGE,"E12.21.0.4"),sQuery(id+"F0.wireOp",EDGE,"E12.21.0.5"),sQuery(id+"F0.wireOp",EDGE,"E12.21.0.6"),sQuery(id+"F0.wireOp",EDGE,"E12.21.0.7"),sQuery(id+"F0.wireOp",EDGE,"E12.21.0.8"),sQuery(id+"F0.wireOp",EDGE,"E12.21.0.9"),sQuery(id+"F0.wireOp",EDGE,"E12.21.0.10"),sQuery(id+"F0.wireOp",EDGE,"E12.22.0.0"),sQuery(id+"F0.wireOp",EDGE,"E12.22.0.1"),sQuery(id+"F0.wireOp",EDGE,"E12.22.0.2"),sQuery(id+"F0.wireOp",EDGE,"E12.22.0.4"),sQuery(id+"F0.wireOp",EDGE,"E12.22.0.5"),sQuery(id+"F0.wireOp",EDGE,"E12.22.0.6"),sQuery(id+"F0.wireOp",EDGE,"E12.22.0.7"),sQuery(id+"F0.wireOp",EDGE,"E12.22.0.8"),sQuery(id+"F0.wireOp",EDGE,"E12.22.0.9"),sQuery(id+"F0.wireOp",EDGE,"E12.22.0.10"),sQuery(id+"F0.wireOp",EDGE,"E12.23.0.0"),sQuery(id+"F0.wireOp",EDGE,"E12.23.0.1"),sQuery(id+"F0.wireOp",EDGE,"E12.23.0.2"),sQuery(id+"F0.wireOp",EDGE,"E12.23.0.4"),sQuery(id+"F0.wireOp",EDGE,"E12.23.0.5"),sQuery(id+"F0.wireOp",EDGE,"E12.23.0.6"),sQuery(id+"F0.wireOp",EDGE,"E12.23.0.7"),sQuery(id+"F0.wireOp",EDGE,"E12.23.0.8"),sQuery(id+"F0.wireOp",EDGE,"E12.23.0.9"),sQuery(id+"F0.wireOp",EDGE,"E12.23.0.10"),sQuery(id+"F0.wireOp",EDGE,"E12.24.0.0"),sQuery(id+"F0.wireOp",EDGE,"E12.24.0.1"),sQuery(id+"F0.wireOp",EDGE,"E12.24.0.2"),sQuery(id+"F0.wireOp",EDGE,"E12.24.0.4"),sQuery(id+"F0.wireOp",EDGE,"E12.24.0.5"),sQuery(id+"F0.wireOp",EDGE,"E12.24.0.6"),sQuery(id+"F0.wireOp",EDGE,"E12.24.0.7"),sQuery(id+"F0.wireOp",EDGE,"E12.24.0.8"),sQuery(id+"F0.wireOp",EDGE,"E12.24.0.9"),sQuery(id+"F0.wireOp",EDGE,"E12.24.0.10"),sQuery(id+"F0.wireOp",EDGE,"E12.25.0.0"),sQuery(id+"F0.wireOp",EDGE,"E12.25.0.1"),sQuery(id+"F0.wireOp",EDGE,"E12.25.0.2"),sQuery(id+"F0.wireOp",EDGE,"E12.25.0.4"),sQuery(id+"F0.wireOp",EDGE,"E12.25.0.5"),sQuery(id+"F0.wireOp",EDGE,"E12.25.0.6"),sQuery(id+"F0.wireOp",EDGE,"E12.25.0.7"),sQuery(id+"F0.wireOp",EDGE,"E12.25.0.8"),sQuery(id+"F0.wireOp",EDGE,"E12.25.0.9"),sQuery(id+"F0.wireOp",EDGE,"E12.25.0.10"),sQuery(id+"F0.wireOp",EDGE,"E12.26.0.0"),sQuery(id+"F0.wireOp",EDGE,"E12.26.0.1"),sQuery(id+"F0.wireOp",EDGE,"E12.26.0.2"),sQuery(id+"F0.wireOp",EDGE,"E12.26.0.4"),sQuery(id+"F0.wireOp",EDGE,"E12.26.0.5"),sQuery(id+"F0.wireOp",EDGE,"E12.26.0.6"),sQuery(id+"F0.wireOp",EDGE,"E12.26.0.7"),sQuery(id+"F0.wireOp",EDGE,"E12.26.0.8"),sQuery(id+"F0.wireOp",EDGE,"E12.26.0.9"),sQuery(id+"F0.wireOp",EDGE,"E12.26.0.10"),sQuery(id+"F0.wireOp",EDGE,"E12.27.0.0"),sQuery(id+"F0.wireOp",EDGE,"E12.27.0.1"),sQuery(id+"F0.wireOp",EDGE,"E12.27.0.2"),sQuery(id+"F0.wireOp",EDGE,"E12.27.0.4"),sQuery(id+"F0.wireOp",EDGE,"E12.27.0.5"),sQuery(id+"F0.wireOp",EDGE,"E12.27.0.6"),sQuery(id+"F0.wireOp",EDGE,"E12.27.0.7"),sQuery(id+"F0.wireOp",EDGE,"E12.27.0.8"),sQuery(id+"F0.wireOp",EDGE,"E12.27.0.9"),sQuery(id+"F0.wireOp",EDGE,"E12.27.0.10"),sQuery(id+"F0.wireOp",EDGE,"E12.28.0.0"),sQuery(id+"F0.wireOp",EDGE,"E12.28.0.1"),sQuery(id+"F0.wireOp",EDGE,"E12.28.0.2"),sQuery(id+"F0.wireOp",EDGE,"E12.28.0.4"),sQuery(id+"F0.wireOp",EDGE,"E12.28.0.5"),sQuery(id+"F0.wireOp",EDGE,"E12.28.0.6"),sQuery(id+"F0.wireOp",EDGE,"E12.28.0.7"),sQuery(id+"F0.wireOp",EDGE,"E12.28.0.8"),sQuery(id+"F0.wireOp",EDGE,"E12.28.0.9"),sQuery(id+"F0.wireOp",EDGE,"E12.28.0.10"),sQuery(id+"F0.wireOp",EDGE,"E12.29.0.0"),sQuery(id+"F0.wireOp",EDGE,"E12.29.0.1"),sQuery(id+"F0.wireOp",EDGE,"E12.29.0.2"),sQuery(id+"F0.wireOp",EDGE,"E12.29.0.4"),sQuery(id+"F0.wireOp",EDGE,"E12.29.0.5"),sQuery(id+"F0.wireOp",EDGE,"E12.29.0.6"),sQuery(id+"F0.wireOp",EDGE,"E12.29.0.7"),sQuery(id+"F0.wireOp",EDGE,"E12.29.0.8"),sQuery(id+"F0.wireOp",EDGE,"E12.29.0.9"),sQuery(id+"F0.wireOp",EDGE,"E12.29.0.10"),sQuery(id+"F0.wireOp",EDGE,"E12.30.0.0"),sQuery(id+"F0.wireOp",EDGE,"E12.30.0.1"),sQuery(id+"F0.wireOp",EDGE,"E12.30.0.2"),sQuery(id+"F0.wireOp",EDGE,"E12.30.0.4"),sQuery(id+"F0.wireOp",EDGE,"E12.30.0.5"),sQuery(id+"F0.wireOp",EDGE,"E12.30.0.6"),sQuery(id+"F0.wireOp",EDGE,"E12.30.0.7"),sQuery(id+"F0.wireOp",EDGE,"E12.30.0.8"),sQuery(id+"F0.wireOp",EDGE,"E12.30.0.9"),sQuery(id+"F0.wireOp",EDGE,"E12.30.0.10"),sQuery(id+"F0.wireOp",EDGE,"E12.31.0.0"),sQuery(id+"F0.wireOp",EDGE,"E12.31.0.1"),sQuery(id+"F0.wireOp",EDGE,"E12.31.0.2"),sQuery(id+"F0.wireOp",EDGE,"E12.31.0.4"),sQuery(id+"F0.wireOp",EDGE,"E12.31.0.5"),sQuery(id+"F0.wireOp",EDGE,"E12.31.0.6"),sQuery(id+"F0.wireOp",EDGE,"E12.31.0.7"),sQuery(id+"F0.wireOp",EDGE,"E12.31.0.8"),sQuery(id+"F0.wireOp",EDGE,"E12.31.0.9"),sQuery(id+"F0.wireOp",EDGE,"E12.31.0.10"),sQuery(id+"F0.wireOp",EDGE,"E12.32.0.0"),sQuery(id+"F0.wireOp",EDGE,"E12.32.0.1"),sQuery(id+"F0.wireOp",EDGE,"E12.32.0.2"),sQuery(id+"F0.wireOp",EDGE,"E12.32.0.4"),sQuery(id+"F0.wireOp",EDGE,"E12.32.0.5"),sQuery(id+"F0.wireOp",EDGE,"E12.32.0.6"),sQuery(id+"F0.wireOp",EDGE,"E12.32.0.7"),sQuery(id+"F0.wireOp",EDGE,"E12.32.0.8"),sQuery(id+"F0.wireOp",EDGE,"E12.32.0.9"),sQuery(id+"F0.wireOp",EDGE,"E12.32.0.10"),sQuery(id+"F0.wireOp",EDGE,"E12.33.0.0"),sQuery(id+"F0.wireOp",EDGE,"E12.33.0.1"),sQuery(id+"F0.wireOp",EDGE,"E12.33.0.2"),sQuery(id+"F0.wireOp",EDGE,"E12.33.0.4"),sQuery(id+"F0.wireOp",EDGE,"E12.33.0.5"),sQuery(id+"F0.wireOp",EDGE,"E12.33.0.6"),sQuery(id+"F0.wireOp",EDGE,"E12.33.0.7"),sQuery(id+"F0.wireOp",EDGE,"E12.33.0.8"),sQuery(id+"F0.wireOp",EDGE,"E12.33.0.9"),sQuery(id+"F0.wireOp",EDGE,"E12.33.0.10"),sQuery(id+"F0.wireOp",EDGE,"E12.34.0.0"),sQuery(id+"F0.wireOp",EDGE,"E12.34.0.1"),sQuery(id+"F0.wireOp",EDGE,"E12.34.0.2"),sQuery(id+"F0.wireOp",EDGE,"E12.34.0.4"),sQuery(id+"F0.wireOp",EDGE,"E12.34.0.5"),sQuery(id+"F0.wireOp",EDGE,"E12.34.0.6"),sQuery(id+"F0.wireOp",EDGE,"E12.34.0.7"),sQuery(id+"F0.wireOp",EDGE,"E12.34.0.8"),sQuery(id+"F0.wireOp",EDGE,"E12.34.0.9"),sQuery(id+"F0.wireOp",EDGE,"E12.34.0.10"),sQuery(id+"F0.wireOp",EDGE,"E12.35.0.0"),sQuery(id+"F0.wireOp",EDGE,"E12.35.0.1"),sQuery(id+"F0.wireOp",EDGE,"E12.35.0.2"),sQuery(id+"F0.wireOp",EDGE,"E12.35.0.4"),sQuery(id+"F0.wireOp",EDGE,"E12.35.0.5"),sQuery(id+"F0.wireOp",EDGE,"E12.35.0.6"),sQuery(id+"F0.wireOp",EDGE,"E12.35.0.7"),sQuery(id+"F0.wireOp",EDGE,"E12.35.0.8"),sQuery(id+"F0.wireOp",EDGE,"E12.35.0.9"),sQuery(id+"F0.wireOp",EDGE,"E12.35.0.10"),sQuery(id+"F0.wireOp",EDGE,"E12.36.0.0"),sQuery(id+"F0.wireOp",EDGE,"E12.36.0.1"),sQuery(id+"F0.wireOp",EDGE,"E12.36.0.2"),sQuery(id+"F0.wireOp",EDGE,"E12.36.0.4"),sQuery(id+"F0.wireOp",EDGE,"E12.36.0.5"),sQuery(id+"F0.wireOp",EDGE,"E12.36.0.6"),sQuery(id+"F0.wireOp",EDGE,"E12.36.0.7"),sQuery(id+"F0.wireOp",EDGE,"E12.36.0.8"),sQuery(id+"F0.wireOp",EDGE,"E12.36.0.9"),sQuery(id+"F0.wireOp",EDGE,"E12.36.0.10"),sQuery(id+"F0.wireOp",EDGE,"E12.37.0.0"),sQuery(id+"F0.wireOp",EDGE,"E12.37.0.1"),sQuery(id+"F0.wireOp",EDGE,"E12.37.0.2"),sQuery(id+"F0.wireOp",EDGE,"E12.37.0.4"),sQuery(id+"F0.wireOp",EDGE,"E12.37.0.5"),sQuery(id+"F0.wireOp",EDGE,"E12.37.0.6"),sQuery(id+"F0.wireOp",EDGE,"E12.37.0.7"),sQuery(id+"F0.wireOp",EDGE,"E12.37.0.8"),sQuery(id+"F0.wireOp",EDGE,"E12.37.0.9"),sQuery(id+"F0.wireOp",EDGE,"E12.37.0.10"),sQuery(id+"F0.wireOp",EDGE,"E12.38.0.0"),sQuery(id+"F0.wireOp",EDGE,"E12.38.0.1"),sQuery(id+"F0.wireOp",EDGE,"E12.38.0.2"),sQuery(id+"F0.wireOp",EDGE,"E12.38.0.4"),sQuery(id+"F0.wireOp",EDGE,"E12.38.0.5"),sQuery(id+"F0.wireOp",EDGE,"E12.38.0.6"),sQuery(id+"F0.wireOp",EDGE,"E12.38.0.7"),sQuery(id+"F0.wireOp",EDGE,"E12.38.0.8"),sQuery(id+"F0.wireOp",EDGE,"E12.38.0.9"),sQuery(id+"F0.wireOp",EDGE,"E12.38.0.10"),sQuery(id+"F0.wireOp",EDGE,"E12.39.0.0"),sQuery(id+"F0.wireOp",EDGE,"E12.39.0.1"),sQuery(id+"F0.wireOp",EDGE,"E12.39.0.2"),sQuery(id+"F0.wireOp",EDGE,"E12.39.0.4"),sQuery(id+"F0.wireOp",EDGE,"E12.39.0.5"),sQuery(id+"F0.wireOp",EDGE,"E12.39.0.6"),sQuery(id+"F0.wireOp",EDGE,"E12.39.0.7"),sQuery(id+"F0.wireOp",EDGE,"E12.39.0.8"),sQuery(id+"F0.wireOp",EDGE,"E12.39.0.9"),sQuery(id+"F0.wireOp",EDGE,"E12.39.0.10"),sQuery(id+"F0.wireOp",EDGE,"E12.40.0.0"),sQuery(id+"F0.wireOp",EDGE,"E12.40.0.1"),sQuery(id+"F0.wireOp",EDGE,"E12.40.0.2"),sQuery(id+"F0.wireOp",EDGE,"E12.40.0.4"),sQuery(id+"F0.wireOp",EDGE,"E12.40.0.5"),sQuery(id+"F0.wireOp",EDGE,"E12.40.0.6"),sQuery(id+"F0.wireOp",EDGE,"E12.40.0.7"),sQuery(id+"F0.wireOp",EDGE,"E12.40.0.8"),sQuery(id+"F0.wireOp",EDGE,"E12.40.0.9"),sQuery(id+"F0.wireOp",EDGE,"E12.40.0.10"),sQuery(id+"F0.wireOp",EDGE,"E12.41.0.0"),sQuery(id+"F0.wireOp",EDGE,"E12.41.0.1"),sQuery(id+"F0.wireOp",EDGE,"E12.41.0.2"),sQuery(id+"F0.wireOp",EDGE,"E12.41.0.4"),sQuery(id+"F0.wireOp",EDGE,"E12.41.0.5"),sQuery(id+"F0.wireOp",EDGE,"E12.41.0.6"),sQuery(id+"F0.wireOp",EDGE,"E12.41.0.7"),sQuery(id+"F0.wireOp",EDGE,"E12.41.0.8"),sQuery(id+"F0.wireOp",EDGE,"E12.41.0.9"),sQuery(id+"F0.wireOp",EDGE,"E12.41.0.10"),sQuery(id+"F0.wireOp",EDGE,"E12.42.0.0"),sQuery(id+"F0.wireOp",EDGE,"E12.42.0.1"),sQuery(id+"F0.wireOp",EDGE,"E12.42.0.2"),sQuery(id+"F0.wireOp",EDGE,"E12.42.0.4"),sQuery(id+"F0.wireOp",EDGE,"E12.42.0.5"),sQuery(id+"F0.wireOp",EDGE,"E12.42.0.6"),sQuery(id+"F0.wireOp",EDGE,"E12.42.0.7"),sQuery(id+"F0.wireOp",EDGE,"E12.42.0.8"),sQuery(id+"F0.wireOp",EDGE,"E12.42.0.9"),sQuery(id+"F0.wireOp",EDGE,"E12.42.0.10"),sQuery(id+"F0.wireOp",EDGE,"E12.43.0.0"),sQuery(id+"F0.wireOp",EDGE,"E12.43.0.1"),sQuery(id+"F0.wireOp",EDGE,"E12.43.0.2"),sQuery(id+"F0.wireOp",EDGE,"E12.43.0.4"),sQuery(id+"F0.wireOp",EDGE,"E12.43.0.5"),sQuery(id+"F0.wireOp",EDGE,"E12.43.0.6"),sQuery(id+"F0.wireOp",EDGE,"E12.43.0.7"),sQuery(id+"F0.wireOp",EDGE,"E12.43.0.8"),sQuery(id+"F0.wireOp",EDGE,"E12.43.0.9"),sQuery(id+"F0.wireOp",EDGE,"E12.43.0.10"),sQuery(id+"F0.wireOp",EDGE,"E12.44.0.0"),sQuery(id+"F0.wireOp",EDGE,"E12.44.0.1"),sQuery(id+"F0.wireOp",EDGE,"E12.44.0.2"),sQuery(id+"F0.wireOp",EDGE,"E12.44.0.4"),sQuery(id+"F0.wireOp",EDGE,"E12.44.0.5"),sQuery(id+"F0.wireOp",EDGE,"E12.44.0.6"),sQuery(id+"F0.wireOp",EDGE,"E12.44.0.7"),sQuery(id+"F0.wireOp",EDGE,"E12.44.0.8"),sQuery(id+"F0.wireOp",EDGE,"E12.44.0.9"),sQuery(id+"F0.wireOp",EDGE,"E12.44.0.10"),sQuery(id+"F0.wireOp",EDGE,"E12.45.0.0"),sQuery(id+"F0.wireOp",EDGE,"E12.45.0.1"),sQuery(id+"F0.wireOp",EDGE,"E12.45.0.2"),sQuery(id+"F0.wireOp",EDGE,"E12.45.0.4"),sQuery(id+"F0.wireOp",EDGE,"E12.45.0.5"),sQuery(id+"F0.wireOp",EDGE,"E12.45.0.6"),sQuery(id+"F0.wireOp",EDGE,"E12.45.0.7"),sQuery(id+"F0.wireOp",EDGE,"E12.45.0.8"),sQuery(id+"F0.wireOp",EDGE,"E12.45.0.9"),sQuery(id+"F0.wireOp",EDGE,"E12.45.0.10"),sQuery(id+"F0.wireOp",EDGE,"E12.46.0.0"),sQuery(id+"F0.wireOp",EDGE,"E12.46.0.1"),sQuery(id+"F0.wireOp",EDGE,"E12.46.0.2"),sQuery(id+"F0.wireOp",EDGE,"E12.46.0.4"),sQuery(id+"F0.wireOp",EDGE,"E12.46.0.5"),sQuery(id+"F0.wireOp",EDGE,"E12.46.0.6"),sQuery(id+"F0.wireOp",EDGE,"E12.46.0.7"),sQuery(id+"F0.wireOp",EDGE,"E12.46.0.8"),sQuery(id+"F0.wireOp",EDGE,"E12.46.0.9"),sQuery(id+"F0.wireOp",EDGE,"E12.46.0.10"),sQuery(id+"F0.wireOp",EDGE,"E12.47.0.0"),sQuery(id+"F0.wireOp",EDGE,"E12.47.0.1"),sQuery(id+"F0.wireOp",EDGE,"E12.47.0.2"),sQuery(id+"F0.wireOp",EDGE,"E12.47.0.4"),sQuery(id+"F0.wireOp",EDGE,"E12.47.0.5"),sQuery(id+"F0.wireOp",EDGE,"E12.47.0.6"),sQuery(id+"F0.wireOp",EDGE,"E12.47.0.7"),sQuery(id+"F0.wireOp",EDGE,"E12.47.0.8"),sQuery(id+"F0.wireOp",EDGE,"E12.47.0.9"),sQuery(id+"F0.wireOp",EDGE,"E12.47.0.10"),sQuery(id+"F0.wireOp",EDGE,"E12.48.0.0"),sQuery(id+"F0.wireOp",EDGE,"E12.48.0.1"),sQuery(id+"F0.wireOp",EDGE,"E12.48.0.2"),sQuery(id+"F0.wireOp",EDGE,"E12.48.0.4"),sQuery(id+"F0.wireOp",EDGE,"E12.48.0.5"),sQuery(id+"F0.wireOp",EDGE,"E12.48.0.6"),sQuery(id+"F0.wireOp",EDGE,"E12.48.0.7"),sQuery(id+"F0.wireOp",EDGE,"E12.48.0.8"),sQuery(id+"F0.wireOp",EDGE,"E12.48.0.9"),sQuery(id+"F0.wireOp",EDGE,"E12.48.0.10"),sQuery(id+"F0.wireOp",EDGE,"E12.49.0.0"),sQuery(id+"F0.wireOp",EDGE,"E12.49.0.1"),sQuery(id+"F0.wireOp",EDGE,"E12.49.0.2"),sQuery(id+"F0.wireOp",EDGE,"E12.49.0.4"),sQuery(id+"F0.wireOp",EDGE,"E12.49.0.5"),sQuery(id+"F0.wireOp",EDGE,"E12.49.0.6"),sQuery(id+"F0.wireOp",EDGE,"E12.49.0.7"),sQuery(id+"F0.wireOp",EDGE,"E12.49.0.8"),sQuery(id+"F0.wireOp",EDGE,"E12.49.0.9"),sQuery(id+"F0.wireOp",EDGE,"E12.49.0.10")])],"isStart":false});
            var sketch = newSketch(context, id + "F23", { "sketchPlane" : qUnion([Q0])});
            skLineSegment(sketch, "E31.bottom", {"start": v(762, 0) * mm, "end": v(723.9, 0) * mm});
            skLineSegment(sketch, "E31.top", {"start": v(762, 8.26) * mm, "end": v(723.9, 8.26) * mm});
            skLineSegment(sketch, "E31.left", {"start": v(762, 0) * mm, "end": v(762, 8.26) * mm});
            skLineSegment(sketch, "E31.right", {"start": v(723.9, 0) * mm, "end": v(723.9, 8.26) * mm});
            skSolve(sketch);
        }
        {
            var Q0;
            Q0 = qSketchRegion(id + "F23", true);
            extrude(context, id + "F24", {"entities" : qUnion([Q0]), "operationType" : NewBodyOperationType.ADD, "depth" : 50.8 * mm});
        }
        {
            var Q0;
            Q0=makeQuery(id+"F24.opExtrude","SWEPT_FACE",FACE,{"disambiguationData":[OSD([sQuery(id+"F23.wireOp",EDGE,"E31.top")])]});
            var sketch = newSketch(context, id + "F25", { "sketchPlane" : qUnion([Q0])});
            skCircle(sketch, "E32", {"center": v(734.06, -167.64) * mm, "radius": 2.54 * mm});
            skCircle(sketch, "E33", {"center": v(751.84, -167.64) * mm, "radius": 2.54 * mm});
            skSolve(sketch);
        }
        {
            var Q0;
            Q0 = qSketchRegion(id + "F25", true);
            extrude(context, id + "F26", {"entities" : qUnion([Q0]), "operationType" : NewBodyOperationType.REMOVE, "endBound" : BoundingType.THROUGH_ALL, "oppositeDirection" : true, "depth" : 25.4 * mm});
        }
        {
            var Q0;
            Q0=makeQuery(id+"F24.opExtrude","SWEPT_FACE",FACE,{"disambiguationData":[OSD([sQuery(id+"F23.wireOp",EDGE,"E31.top")])]});
            var sketch = newSketch(context, id + "F27", { "sketchPlane" : qUnion([Q0])});
            skCircle(sketch, "E34", {"center": v(734.06, -167.64) * mm, "radius": 3.81 * mm});
            skCircle(sketch, "E35", {"center": v(751.84, -167.64) * mm, "radius": 3.81 * mm});
            skSolve(sketch);
        }
        {
            var Q0;
            Q0 = qSketchRegion(id + "F27", true);
            extrude(context, id + "F28", {"entities" : qUnion([Q0]), "operationType" : NewBodyOperationType.REMOVE, "oppositeDirection" : true, "depth" : 2.54 * mm});
        }
        {
            var Q0;
            Q0=makeQuery(id+"F24.opExtrude","CAP_EDGE",EDGE,{"disambiguationData":[OSD([sQuery(id+"F23.wireOp",EDGE,"E31.right")])],"isStart":false});
            var Q1;
            Q1=makeQuery(id+"F24.opExtrude","CAP_EDGE",EDGE,{"disambiguationData":[OSD([sQuery(id+"F23.wireOp",EDGE,"E31.left")])],"isStart":false});
            fillet(context, id + "F29", {"entities" : qUnion([Q0, Q1]), "radius" : 5.08 * mm, "tangentPropagation" : true, "allowEdgeOverflow" : false});
        }
    });
